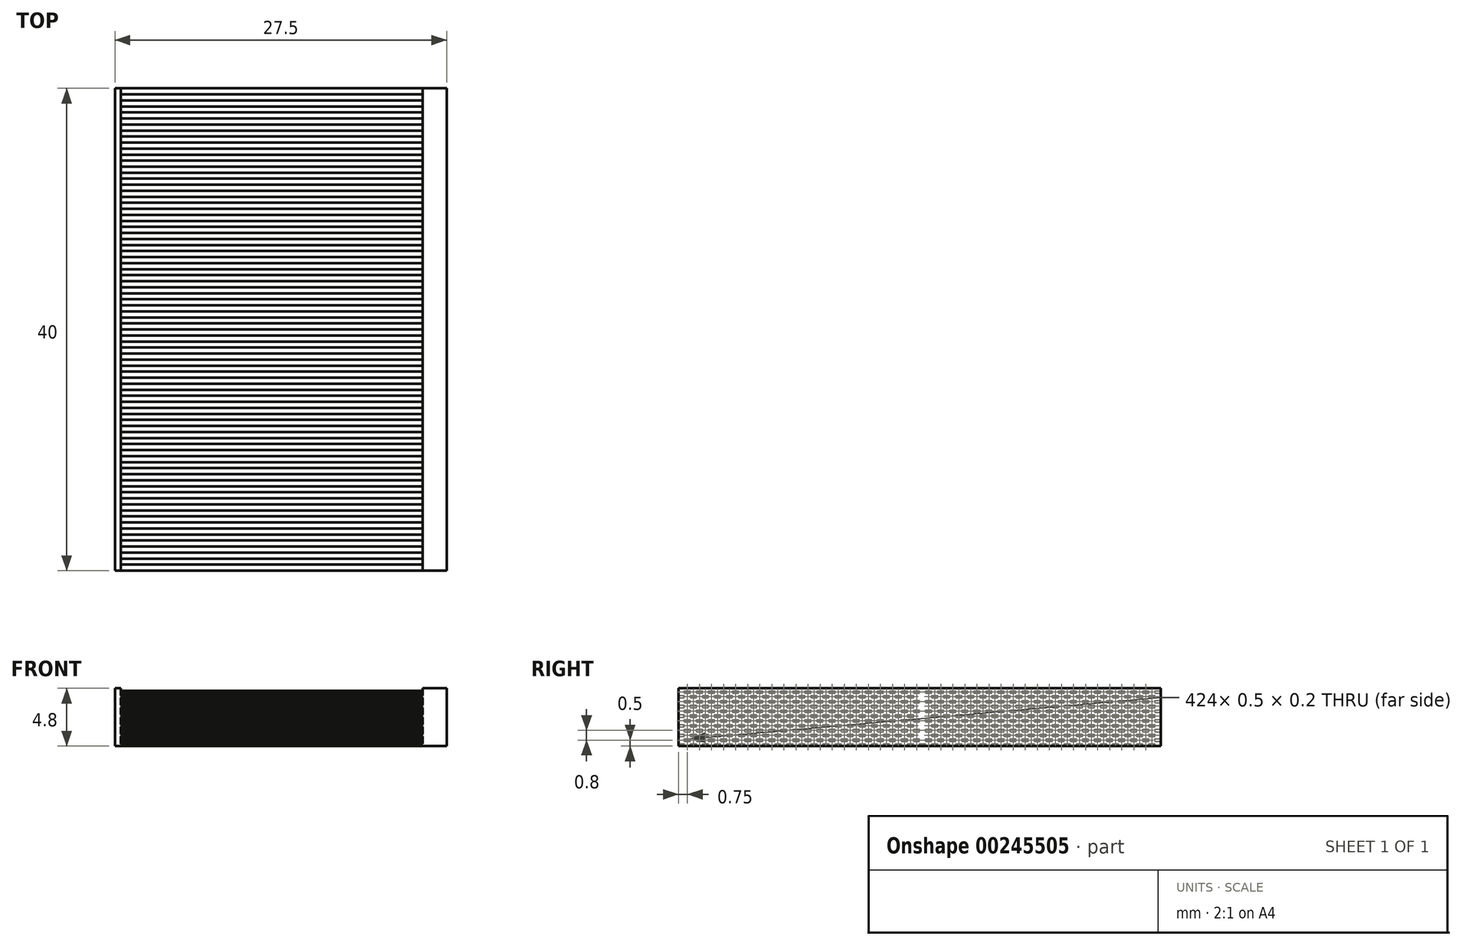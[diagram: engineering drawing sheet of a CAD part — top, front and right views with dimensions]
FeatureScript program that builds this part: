
annotation { "Feature Type Name" : "Feature", "Feature Type Description" : "" }
export const myFeature = defineFeature(function(context is Context, id is Id, definition is map)
    precondition{}
    {
        {
            var Q0;
            Q0=qCreatedBy(makeId("Right.planeOp"),FACE);
            var sketch = newSketch(context, id + "F0", { "sketchPlane" : qUnion([Q0])});
            skLineSegment(sketch, "E0.bottom", {"start": v(-20, 0) * mm, "end": v(20, 0) * mm});
            skLineSegment(sketch, "E0.top", {"start": v(-20, 4.8) * mm, "end": v(20, 4.8) * mm});
            skLineSegment(sketch, "E0.left", {"start": v(-20, 0) * mm, "end": v(-20, 4.8) * mm});
            skLineSegment(sketch, "E0.right", {"start": v(20, 0) * mm, "end": v(20, 4.8) * mm});
            skPoint(sketch, "E0.middle", {"position": v(0, 2.4) * mm});
            skSolve(sketch);
        }
        {
            var Q0;
            Q0 = qSketchRegion(id + "F0", true);
            extrude(context, id + "F1", {"entities" : qUnion([Q0]), "depth" : 0.5 * mm});
        }
        {
            var Q0;
            Q0=makeQuery(id+"F1.opExtrude","CAP_FACE",FACE,{"disambiguationData":[OSD([sQuery(id+"F0.wireOp",EDGE,"E0.bottom"),sQuery(id+"F0.wireOp",EDGE,"E0.top"),sQuery(id+"F0.wireOp",EDGE,"E0.left"),sQuery(id+"F0.wireOp",EDGE,"E0.right")])],"isStart":false});
            var sketch = newSketch(context, id + "F2", { "sketchPlane" : qUnion([Q0])});
            skLineSegment(sketch, "E1.bottom", {"start": v(-20, 0) * mm, "end": v(-19.5, 0) * mm});
            skLineSegment(sketch, "E1.top", {"start": v(-20, 0.2) * mm, "end": v(-19.5, 0.2) * mm});
            skLineSegment(sketch, "E1.left", {"start": v(-20, 0) * mm, "end": v(-20, 0.2) * mm});
            skLineSegment(sketch, "E1.right", {"start": v(-19.5, 0) * mm, "end": v(-19.5, 0.2) * mm});
            skLineSegment(sketch, "E2.1.0.0", {"start": v(-19, 0) * mm, "end": v(-19, 0.2) * mm});
            skLineSegment(sketch, "E2.1.0.1", {"start": v(-18.5, 0) * mm, "end": v(-18.5, 0.2) * mm});
            skLineSegment(sketch, "E2.1.0.2", {"start": v(-19, 0.2) * mm, "end": v(-18.5, 0.2) * mm});
            skLineSegment(sketch, "E2.1.0.3", {"start": v(-19, 0) * mm, "end": v(-18.5, 0) * mm});
            skLineSegment(sketch, "E2.2.0.0", {"start": v(-18, 0) * mm, "end": v(-18, 0.2) * mm});
            skLineSegment(sketch, "E2.2.0.1", {"start": v(-17.5, 0) * mm, "end": v(-17.5, 0.2) * mm});
            skLineSegment(sketch, "E2.2.0.2", {"start": v(-18, 0.2) * mm, "end": v(-17.5, 0.2) * mm});
            skLineSegment(sketch, "E2.2.0.3", {"start": v(-18, 0) * mm, "end": v(-17.5, 0) * mm});
            skLineSegment(sketch, "E2.3.0.0", {"start": v(-17, 0) * mm, "end": v(-17, 0.2) * mm});
            skLineSegment(sketch, "E2.3.0.1", {"start": v(-16.5, 0) * mm, "end": v(-16.5, 0.2) * mm});
            skLineSegment(sketch, "E2.3.0.2", {"start": v(-17, 0.2) * mm, "end": v(-16.5, 0.2) * mm});
            skLineSegment(sketch, "E2.3.0.3", {"start": v(-17, 0) * mm, "end": v(-16.5, 0) * mm});
            skLineSegment(sketch, "E2.4.0.0", {"start": v(-16, 0) * mm, "end": v(-16, 0.2) * mm});
            skLineSegment(sketch, "E2.4.0.1", {"start": v(-15.5, 0) * mm, "end": v(-15.5, 0.2) * mm});
            skLineSegment(sketch, "E2.4.0.2", {"start": v(-16, 0.2) * mm, "end": v(-15.5, 0.2) * mm});
            skLineSegment(sketch, "E2.4.0.3", {"start": v(-16, 0) * mm, "end": v(-15.5, 0) * mm});
            skLineSegment(sketch, "E2.5.0.0", {"start": v(-15, 0) * mm, "end": v(-15, 0.2) * mm});
            skLineSegment(sketch, "E2.5.0.1", {"start": v(-14.5, 0) * mm, "end": v(-14.5, 0.2) * mm});
            skLineSegment(sketch, "E2.5.0.2", {"start": v(-15, 0.2) * mm, "end": v(-14.5, 0.2) * mm});
            skLineSegment(sketch, "E2.5.0.3", {"start": v(-15, 0) * mm, "end": v(-14.5, 0) * mm});
            skLineSegment(sketch, "E2.6.0.0", {"start": v(-14, 0) * mm, "end": v(-14, 0.2) * mm});
            skLineSegment(sketch, "E2.6.0.1", {"start": v(-13.5, 0) * mm, "end": v(-13.5, 0.2) * mm});
            skLineSegment(sketch, "E2.6.0.2", {"start": v(-14, 0.2) * mm, "end": v(-13.5, 0.2) * mm});
            skLineSegment(sketch, "E2.6.0.3", {"start": v(-14, 0) * mm, "end": v(-13.5, 0) * mm});
            skLineSegment(sketch, "E2.7.0.0", {"start": v(-13, 0) * mm, "end": v(-13, 0.2) * mm});
            skLineSegment(sketch, "E2.7.0.1", {"start": v(-12.5, 0) * mm, "end": v(-12.5, 0.2) * mm});
            skLineSegment(sketch, "E2.7.0.2", {"start": v(-13, 0.2) * mm, "end": v(-12.5, 0.2) * mm});
            skLineSegment(sketch, "E2.7.0.3", {"start": v(-13, 0) * mm, "end": v(-12.5, 0) * mm});
            skLineSegment(sketch, "E2.8.0.0", {"start": v(-12, 0) * mm, "end": v(-12, 0.2) * mm});
            skLineSegment(sketch, "E2.8.0.1", {"start": v(-11.5, 0) * mm, "end": v(-11.5, 0.2) * mm});
            skLineSegment(sketch, "E2.8.0.2", {"start": v(-12, 0.2) * mm, "end": v(-11.5, 0.2) * mm});
            skLineSegment(sketch, "E2.8.0.3", {"start": v(-12, 0) * mm, "end": v(-11.5, 0) * mm});
            skLineSegment(sketch, "E2.9.0.0", {"start": v(-11, 0) * mm, "end": v(-11, 0.2) * mm});
            skLineSegment(sketch, "E2.9.0.1", {"start": v(-10.5, 0) * mm, "end": v(-10.5, 0.2) * mm});
            skLineSegment(sketch, "E2.9.0.2", {"start": v(-11, 0.2) * mm, "end": v(-10.5, 0.2) * mm});
            skLineSegment(sketch, "E2.9.0.3", {"start": v(-11, 0) * mm, "end": v(-10.5, 0) * mm});
            skLineSegment(sketch, "E2.10.0.0", {"start": v(-10, 0) * mm, "end": v(-10, 0.2) * mm});
            skLineSegment(sketch, "E2.10.0.1", {"start": v(-9.5, 0) * mm, "end": v(-9.5, 0.2) * mm});
            skLineSegment(sketch, "E2.10.0.2", {"start": v(-10, 0.2) * mm, "end": v(-9.5, 0.2) * mm});
            skLineSegment(sketch, "E2.10.0.3", {"start": v(-10, 0) * mm, "end": v(-9.5, 0) * mm});
            skLineSegment(sketch, "E2.11.0.0", {"start": v(-9, 0) * mm, "end": v(-9, 0.2) * mm});
            skLineSegment(sketch, "E2.11.0.1", {"start": v(-8.5, 0) * mm, "end": v(-8.5, 0.2) * mm});
            skLineSegment(sketch, "E2.11.0.2", {"start": v(-9, 0.2) * mm, "end": v(-8.5, 0.2) * mm});
            skLineSegment(sketch, "E2.11.0.3", {"start": v(-9, 0) * mm, "end": v(-8.5, 0) * mm});
            skLineSegment(sketch, "E2.12.0.0", {"start": v(-8, 0) * mm, "end": v(-8, 0.2) * mm});
            skLineSegment(sketch, "E2.12.0.1", {"start": v(-7.5, 0) * mm, "end": v(-7.5, 0.2) * mm});
            skLineSegment(sketch, "E2.12.0.2", {"start": v(-8, 0.2) * mm, "end": v(-7.5, 0.2) * mm});
            skLineSegment(sketch, "E2.12.0.3", {"start": v(-8, 0) * mm, "end": v(-7.5, 0) * mm});
            skLineSegment(sketch, "E2.13.0.0", {"start": v(-7, 0) * mm, "end": v(-7, 0.2) * mm});
            skLineSegment(sketch, "E2.13.0.1", {"start": v(-6.5, 0) * mm, "end": v(-6.5, 0.2) * mm});
            skLineSegment(sketch, "E2.13.0.2", {"start": v(-7, 0.2) * mm, "end": v(-6.5, 0.2) * mm});
            skLineSegment(sketch, "E2.13.0.3", {"start": v(-7, 0) * mm, "end": v(-6.5, 0) * mm});
            skLineSegment(sketch, "E2.14.0.0", {"start": v(-6, 0) * mm, "end": v(-6, 0.2) * mm});
            skLineSegment(sketch, "E2.14.0.1", {"start": v(-5.5, 0) * mm, "end": v(-5.5, 0.2) * mm});
            skLineSegment(sketch, "E2.14.0.2", {"start": v(-6, 0.2) * mm, "end": v(-5.5, 0.2) * mm});
            skLineSegment(sketch, "E2.14.0.3", {"start": v(-6, 0) * mm, "end": v(-5.5, 0) * mm});
            skLineSegment(sketch, "E2.15.0.0", {"start": v(-5, 0) * mm, "end": v(-5, 0.2) * mm});
            skLineSegment(sketch, "E2.15.0.1", {"start": v(-4.5, 0) * mm, "end": v(-4.5, 0.2) * mm});
            skLineSegment(sketch, "E2.15.0.2", {"start": v(-5, 0.2) * mm, "end": v(-4.5, 0.2) * mm});
            skLineSegment(sketch, "E2.15.0.3", {"start": v(-5, 0) * mm, "end": v(-4.5, 0) * mm});
            skLineSegment(sketch, "E2.16.0.0", {"start": v(-4, 0) * mm, "end": v(-4, 0.2) * mm});
            skLineSegment(sketch, "E2.16.0.1", {"start": v(-3.5, 0) * mm, "end": v(-3.5, 0.2) * mm});
            skLineSegment(sketch, "E2.16.0.2", {"start": v(-4, 0.2) * mm, "end": v(-3.5, 0.2) * mm});
            skLineSegment(sketch, "E2.16.0.3", {"start": v(-4, 0) * mm, "end": v(-3.5, 0) * mm});
            skLineSegment(sketch, "E2.17.0.0", {"start": v(-3, 0) * mm, "end": v(-3, 0.2) * mm});
            skLineSegment(sketch, "E2.17.0.1", {"start": v(-2.5, 0) * mm, "end": v(-2.5, 0.2) * mm});
            skLineSegment(sketch, "E2.17.0.2", {"start": v(-3, 0.2) * mm, "end": v(-2.5, 0.2) * mm});
            skLineSegment(sketch, "E2.17.0.3", {"start": v(-3, 0) * mm, "end": v(-2.5, 0) * mm});
            skLineSegment(sketch, "E2.18.0.0", {"start": v(-2, 0) * mm, "end": v(-2, 0.2) * mm});
            skLineSegment(sketch, "E2.18.0.1", {"start": v(-1.5, 0) * mm, "end": v(-1.5, 0.2) * mm});
            skLineSegment(sketch, "E2.18.0.2", {"start": v(-2, 0.2) * mm, "end": v(-1.5, 0.2) * mm});
            skLineSegment(sketch, "E2.18.0.3", {"start": v(-2, 0) * mm, "end": v(-1.5, 0) * mm});
            skLineSegment(sketch, "E2.19.0.0", {"start": v(-1, 0) * mm, "end": v(-1, 0.2) * mm});
            skLineSegment(sketch, "E2.19.0.1", {"start": v(-0.5, 0) * mm, "end": v(-0.5, 0.2) * mm});
            skLineSegment(sketch, "E2.19.0.2", {"start": v(-1, 0.2) * mm, "end": v(-0.5, 0.2) * mm});
            skLineSegment(sketch, "E2.19.0.3", {"start": v(-1, 0) * mm, "end": v(-0.5, 0) * mm});
            skLineSegment(sketch, "E2.direction1", {"start": v(-20, 0) * mm, "end": v(-19, 0) * mm, "construction": true});
            skLineSegment(sketch, "E3.bottom", {"start": v(-19.5, 0.4) * mm, "end": v(-19, 0.4) * mm});
            skLineSegment(sketch, "E3.top", {"start": v(-19.5, 0.6) * mm, "end": v(-19, 0.6) * mm});
            skLineSegment(sketch, "E3.left", {"start": v(-19.5, 0.4) * mm, "end": v(-19.5, 0.6) * mm});
            skLineSegment(sketch, "E3.right", {"start": v(-19, 0.4) * mm, "end": v(-19, 0.6) * mm});
            skLineSegment(sketch, "E4.1.0.0", {"start": v(-18, 0.4) * mm, "end": v(-18, 0.6) * mm});
            skLineSegment(sketch, "E4.1.0.1", {"start": v(-18.5, 0.4) * mm, "end": v(-18, 0.4) * mm});
            skLineSegment(sketch, "E4.1.0.2", {"start": v(-18.5, 0.6) * mm, "end": v(-18, 0.6) * mm});
            skLineSegment(sketch, "E4.1.0.3", {"start": v(-18.5, 0.4) * mm, "end": v(-18.5, 0.6) * mm});
            skLineSegment(sketch, "E4.2.0.0", {"start": v(-17, 0.4) * mm, "end": v(-17, 0.6) * mm});
            skLineSegment(sketch, "E4.2.0.1", {"start": v(-17.5, 0.4) * mm, "end": v(-17, 0.4) * mm});
            skLineSegment(sketch, "E4.2.0.2", {"start": v(-17.5, 0.6) * mm, "end": v(-17, 0.6) * mm});
            skLineSegment(sketch, "E4.2.0.3", {"start": v(-17.5, 0.4) * mm, "end": v(-17.5, 0.6) * mm});
            skLineSegment(sketch, "E4.3.0.0", {"start": v(-16, 0.4) * mm, "end": v(-16, 0.6) * mm});
            skLineSegment(sketch, "E4.3.0.1", {"start": v(-16.5, 0.4) * mm, "end": v(-16, 0.4) * mm});
            skLineSegment(sketch, "E4.3.0.2", {"start": v(-16.5, 0.6) * mm, "end": v(-16, 0.6) * mm});
            skLineSegment(sketch, "E4.3.0.3", {"start": v(-16.5, 0.4) * mm, "end": v(-16.5, 0.6) * mm});
            skLineSegment(sketch, "E4.4.0.0", {"start": v(-15, 0.4) * mm, "end": v(-15, 0.6) * mm});
            skLineSegment(sketch, "E4.4.0.1", {"start": v(-15.5, 0.4) * mm, "end": v(-15, 0.4) * mm});
            skLineSegment(sketch, "E4.4.0.2", {"start": v(-15.5, 0.6) * mm, "end": v(-15, 0.6) * mm});
            skLineSegment(sketch, "E4.4.0.3", {"start": v(-15.5, 0.4) * mm, "end": v(-15.5, 0.6) * mm});
            skLineSegment(sketch, "E4.5.0.0", {"start": v(-14, 0.4) * mm, "end": v(-14, 0.6) * mm});
            skLineSegment(sketch, "E4.5.0.1", {"start": v(-14.5, 0.4) * mm, "end": v(-14, 0.4) * mm});
            skLineSegment(sketch, "E4.5.0.2", {"start": v(-14.5, 0.6) * mm, "end": v(-14, 0.6) * mm});
            skLineSegment(sketch, "E4.5.0.3", {"start": v(-14.5, 0.4) * mm, "end": v(-14.5, 0.6) * mm});
            skLineSegment(sketch, "E4.6.0.0", {"start": v(-13, 0.4) * mm, "end": v(-13, 0.6) * mm});
            skLineSegment(sketch, "E4.6.0.1", {"start": v(-13.5, 0.4) * mm, "end": v(-13, 0.4) * mm});
            skLineSegment(sketch, "E4.6.0.2", {"start": v(-13.5, 0.6) * mm, "end": v(-13, 0.6) * mm});
            skLineSegment(sketch, "E4.6.0.3", {"start": v(-13.5, 0.4) * mm, "end": v(-13.5, 0.6) * mm});
            skLineSegment(sketch, "E4.7.0.0", {"start": v(-12, 0.4) * mm, "end": v(-12, 0.6) * mm});
            skLineSegment(sketch, "E4.7.0.1", {"start": v(-12.5, 0.4) * mm, "end": v(-12, 0.4) * mm});
            skLineSegment(sketch, "E4.7.0.2", {"start": v(-12.5, 0.6) * mm, "end": v(-12, 0.6) * mm});
            skLineSegment(sketch, "E4.7.0.3", {"start": v(-12.5, 0.4) * mm, "end": v(-12.5, 0.6) * mm});
            skLineSegment(sketch, "E4.8.0.0", {"start": v(-11, 0.4) * mm, "end": v(-11, 0.6) * mm});
            skLineSegment(sketch, "E4.8.0.1", {"start": v(-11.5, 0.4) * mm, "end": v(-11, 0.4) * mm});
            skLineSegment(sketch, "E4.8.0.2", {"start": v(-11.5, 0.6) * mm, "end": v(-11, 0.6) * mm});
            skLineSegment(sketch, "E4.8.0.3", {"start": v(-11.5, 0.4) * mm, "end": v(-11.5, 0.6) * mm});
            skLineSegment(sketch, "E4.9.0.0", {"start": v(-10, 0.4) * mm, "end": v(-10, 0.6) * mm});
            skLineSegment(sketch, "E4.9.0.1", {"start": v(-10.5, 0.4) * mm, "end": v(-10, 0.4) * mm});
            skLineSegment(sketch, "E4.9.0.2", {"start": v(-10.5, 0.6) * mm, "end": v(-10, 0.6) * mm});
            skLineSegment(sketch, "E4.9.0.3", {"start": v(-10.5, 0.4) * mm, "end": v(-10.5, 0.6) * mm});
            skLineSegment(sketch, "E4.10.0.0", {"start": v(-9, 0.4) * mm, "end": v(-9, 0.6) * mm});
            skLineSegment(sketch, "E4.10.0.1", {"start": v(-9.5, 0.4) * mm, "end": v(-9, 0.4) * mm});
            skLineSegment(sketch, "E4.10.0.2", {"start": v(-9.5, 0.6) * mm, "end": v(-9, 0.6) * mm});
            skLineSegment(sketch, "E4.10.0.3", {"start": v(-9.5, 0.4) * mm, "end": v(-9.5, 0.6) * mm});
            skLineSegment(sketch, "E4.11.0.0", {"start": v(-8, 0.4) * mm, "end": v(-8, 0.6) * mm});
            skLineSegment(sketch, "E4.11.0.1", {"start": v(-8.5, 0.4) * mm, "end": v(-8, 0.4) * mm});
            skLineSegment(sketch, "E4.11.0.2", {"start": v(-8.5, 0.6) * mm, "end": v(-8, 0.6) * mm});
            skLineSegment(sketch, "E4.11.0.3", {"start": v(-8.5, 0.4) * mm, "end": v(-8.5, 0.6) * mm});
            skLineSegment(sketch, "E4.12.0.0", {"start": v(-7, 0.4) * mm, "end": v(-7, 0.6) * mm});
            skLineSegment(sketch, "E4.12.0.1", {"start": v(-7.5, 0.4) * mm, "end": v(-7, 0.4) * mm});
            skLineSegment(sketch, "E4.12.0.2", {"start": v(-7.5, 0.6) * mm, "end": v(-7, 0.6) * mm});
            skLineSegment(sketch, "E4.12.0.3", {"start": v(-7.5, 0.4) * mm, "end": v(-7.5, 0.6) * mm});
            skLineSegment(sketch, "E4.13.0.0", {"start": v(-6, 0.4) * mm, "end": v(-6, 0.6) * mm});
            skLineSegment(sketch, "E4.13.0.1", {"start": v(-6.5, 0.4) * mm, "end": v(-6, 0.4) * mm});
            skLineSegment(sketch, "E4.13.0.2", {"start": v(-6.5, 0.6) * mm, "end": v(-6, 0.6) * mm});
            skLineSegment(sketch, "E4.13.0.3", {"start": v(-6.5, 0.4) * mm, "end": v(-6.5, 0.6) * mm});
            skLineSegment(sketch, "E4.14.0.0", {"start": v(-5, 0.4) * mm, "end": v(-5, 0.6) * mm});
            skLineSegment(sketch, "E4.14.0.1", {"start": v(-5.5, 0.4) * mm, "end": v(-5, 0.4) * mm});
            skLineSegment(sketch, "E4.14.0.2", {"start": v(-5.5, 0.6) * mm, "end": v(-5, 0.6) * mm});
            skLineSegment(sketch, "E4.14.0.3", {"start": v(-5.5, 0.4) * mm, "end": v(-5.5, 0.6) * mm});
            skLineSegment(sketch, "E4.15.0.0", {"start": v(-4, 0.4) * mm, "end": v(-4, 0.6) * mm});
            skLineSegment(sketch, "E4.15.0.1", {"start": v(-4.5, 0.4) * mm, "end": v(-4, 0.4) * mm});
            skLineSegment(sketch, "E4.15.0.2", {"start": v(-4.5, 0.6) * mm, "end": v(-4, 0.6) * mm});
            skLineSegment(sketch, "E4.15.0.3", {"start": v(-4.5, 0.4) * mm, "end": v(-4.5, 0.6) * mm});
            skLineSegment(sketch, "E4.16.0.0", {"start": v(-3, 0.4) * mm, "end": v(-3, 0.6) * mm});
            skLineSegment(sketch, "E4.16.0.1", {"start": v(-3.5, 0.4) * mm, "end": v(-3, 0.4) * mm});
            skLineSegment(sketch, "E4.16.0.2", {"start": v(-3.5, 0.6) * mm, "end": v(-3, 0.6) * mm});
            skLineSegment(sketch, "E4.16.0.3", {"start": v(-3.5, 0.4) * mm, "end": v(-3.5, 0.6) * mm});
            skLineSegment(sketch, "E4.17.0.0", {"start": v(-2, 0.4) * mm, "end": v(-2, 0.6) * mm});
            skLineSegment(sketch, "E4.17.0.1", {"start": v(-2.5, 0.4) * mm, "end": v(-2, 0.4) * mm});
            skLineSegment(sketch, "E4.17.0.2", {"start": v(-2.5, 0.6) * mm, "end": v(-2, 0.6) * mm});
            skLineSegment(sketch, "E4.17.0.3", {"start": v(-2.5, 0.4) * mm, "end": v(-2.5, 0.6) * mm});
            skLineSegment(sketch, "E4.18.0.0", {"start": v(-1, 0.4) * mm, "end": v(-1, 0.6) * mm});
            skLineSegment(sketch, "E4.18.0.1", {"start": v(-1.5, 0.4) * mm, "end": v(-1, 0.4) * mm});
            skLineSegment(sketch, "E4.18.0.2", {"start": v(-1.5, 0.6) * mm, "end": v(-1, 0.6) * mm});
            skLineSegment(sketch, "E4.18.0.3", {"start": v(-1.5, 0.4) * mm, "end": v(-1.5, 0.6) * mm});
            skLineSegment(sketch, "E4.19.0.0", {"start": v(0, 0.4) * mm, "end": v(0, 0.6) * mm});
            skLineSegment(sketch, "E4.19.0.1", {"start": v(-0.5, 0.4) * mm, "end": v(0, 0.4) * mm});
            skLineSegment(sketch, "E4.19.0.2", {"start": v(-0.5, 0.6) * mm, "end": v(0, 0.6) * mm});
            skLineSegment(sketch, "E4.19.0.3", {"start": v(-0.5, 0.4) * mm, "end": v(-0.5, 0.6) * mm});
            skLineSegment(sketch, "E4.direction1", {"start": v(-19.5, 0.4) * mm, "end": v(-18.5, 0.4) * mm, "construction": true});
            skLineSegment(sketch, "E5.0.1.0", {"start": v(-5, 1) * mm, "end": v(-4.5, 1) * mm});
            skLineSegment(sketch, "E5.0.1.1", {"start": v(-13.5, 1.4) * mm, "end": v(-13, 1.4) * mm});
            skLineSegment(sketch, "E5.0.1.2", {"start": v(-17, 0.8) * mm, "end": v(-16.5, 0.8) * mm});
            skLineSegment(sketch, "E5.0.1.3", {"start": v(-19.5, 1.4) * mm, "end": v(-19, 1.4) * mm});
            skLineSegment(sketch, "E5.0.1.4", {"start": v(-16.5, 1.4) * mm, "end": v(-16, 1.4) * mm});
            skLineSegment(sketch, "E5.0.1.5", {"start": v(-14.5, 1.4) * mm, "end": v(-14, 1.4) * mm});
            skLineSegment(sketch, "E5.0.1.6", {"start": v(-19, 0.8) * mm, "end": v(-18.5, 0.8) * mm});
            skLineSegment(sketch, "E5.0.1.7", {"start": v(-15, 0.8) * mm, "end": v(-14.5, 0.8) * mm});
            skLineSegment(sketch, "E5.0.1.8", {"start": v(-4.5, 1.4) * mm, "end": v(-4, 1.4) * mm});
            skLineSegment(sketch, "E5.0.1.9", {"start": v(-7.5, 1.4) * mm, "end": v(-7, 1.4) * mm});
            skLineSegment(sketch, "E5.0.1.10", {"start": v(-12.5, 1.4) * mm, "end": v(-12, 1.4) * mm});
            skLineSegment(sketch, "E5.0.1.11", {"start": v(-0.5, 1.2) * mm, "end": v(0, 1.2) * mm});
            skLineSegment(sketch, "E5.0.1.12", {"start": v(-1.5, 1.4) * mm, "end": v(-1, 1.4) * mm});
            skLineSegment(sketch, "E5.0.1.13", {"start": v(-16, 0.8) * mm, "end": v(-15.5, 0.8) * mm});
            skLineSegment(sketch, "E5.0.1.14", {"start": v(-12, 0.8) * mm, "end": v(-11.5, 0.8) * mm});
            skLineSegment(sketch, "E5.0.1.15", {"start": v(-18.5, 1.4) * mm, "end": v(-18, 1.4) * mm});
            skLineSegment(sketch, "E5.0.1.16", {"start": v(-18.5, 1.2) * mm, "end": v(-18, 1.2) * mm});
            skLineSegment(sketch, "E5.0.1.17", {"start": v(-0.5, 1.4) * mm, "end": v(0, 1.4) * mm});
            skLineSegment(sketch, "E5.0.1.18", {"start": v(-13, 0.8) * mm, "end": v(-13, 1) * mm});
            skLineSegment(sketch, "E5.0.1.19", {"start": v(-10, 1.2) * mm, "end": v(-10, 1.4) * mm});
            skLineSegment(sketch, "E5.0.1.20", {"start": v(-1, 1) * mm, "end": v(-0.5, 1) * mm});
            skLineSegment(sketch, "E5.0.1.21", {"start": v(-11, 0.8) * mm, "end": v(-11, 1) * mm});
            skLineSegment(sketch, "E5.0.1.22", {"start": v(-18.5, 0.8) * mm, "end": v(-18.5, 1) * mm});
            skLineSegment(sketch, "E5.0.1.23", {"start": v(-7, 1) * mm, "end": v(-6.5, 1) * mm});
            skLineSegment(sketch, "E5.0.1.24", {"start": v(-17.5, 1.4) * mm, "end": v(-17, 1.4) * mm});
            skLineSegment(sketch, "E5.0.1.25", {"start": v(-13, 1) * mm, "end": v(-12.5, 1) * mm});
            skLineSegment(sketch, "E5.0.1.26", {"start": v(-20, 1) * mm, "end": v(-19.5, 1) * mm});
            skLineSegment(sketch, "E5.0.1.27", {"start": v(-16.5, 1.2) * mm, "end": v(-16, 1.2) * mm});
            skLineSegment(sketch, "E5.0.1.28", {"start": v(-8.5, 1.4) * mm, "end": v(-8, 1.4) * mm});
            skLineSegment(sketch, "E5.0.1.29", {"start": v(-15, 0.8) * mm, "end": v(-15, 1) * mm});
            skLineSegment(sketch, "E5.0.1.30", {"start": v(-8.5, 1.2) * mm, "end": v(-8, 1.2) * mm});
            skLineSegment(sketch, "E5.0.1.31", {"start": v(-9.5, 1.4) * mm, "end": v(-9, 1.4) * mm});
            skLineSegment(sketch, "E5.0.1.32", {"start": v(-6.5, 1.2) * mm, "end": v(-6, 1.2) * mm});
            skLineSegment(sketch, "E5.0.1.33", {"start": v(-8, 1.2) * mm, "end": v(-8, 1.4) * mm});
            skLineSegment(sketch, "E5.0.1.34", {"start": v(-16, 1.2) * mm, "end": v(-16, 1.4) * mm});
            skLineSegment(sketch, "E5.0.1.35", {"start": v(-11.5, 1.4) * mm, "end": v(-11, 1.4) * mm});
            skLineSegment(sketch, "E5.0.1.36", {"start": v(-12.5, 1.2) * mm, "end": v(-12, 1.2) * mm});
            skLineSegment(sketch, "E5.0.1.37", {"start": v(-10, 0.8) * mm, "end": v(-9.5, 0.8) * mm});
            skLineSegment(sketch, "E5.0.1.38", {"start": v(-8, 0.8) * mm, "end": v(-7.5, 0.8) * mm});
            skLineSegment(sketch, "E5.0.1.39", {"start": v(-6, 0.8) * mm, "end": v(-5.5, 0.8) * mm});
            skLineSegment(sketch, "E5.0.1.40", {"start": v(-2, 0.8) * mm, "end": v(-1.5, 0.8) * mm});
            skLineSegment(sketch, "E5.0.1.41", {"start": v(-3.5, 1.4) * mm, "end": v(-3, 1.4) * mm});
            skLineSegment(sketch, "E5.0.1.42", {"start": v(-1, 0.8) * mm, "end": v(-1, 1) * mm});
            skLineSegment(sketch, "E5.0.1.43", {"start": v(-4, 0.8) * mm, "end": v(-3.5, 0.8) * mm});
            skLineSegment(sketch, "E5.0.1.44", {"start": v(-5, 0.8) * mm, "end": v(-5, 1) * mm});
            skLineSegment(sketch, "E5.0.1.45", {"start": v(-9, 0.8) * mm, "end": v(-9, 1) * mm});
            skLineSegment(sketch, "E5.0.1.46", {"start": v(-15.5, 1.4) * mm, "end": v(-15, 1.4) * mm});
            skLineSegment(sketch, "E5.0.1.47", {"start": v(-20, 0.8) * mm, "end": v(-20, 1) * mm});
            skLineSegment(sketch, "E5.0.1.48", {"start": v(-18, 0.8) * mm, "end": v(-17.5, 0.8) * mm});
            skLineSegment(sketch, "E5.0.1.49", {"start": v(-17, 0.8) * mm, "end": v(-17, 1) * mm});
            skLineSegment(sketch, "E5.0.1.50", {"start": v(-19, 1) * mm, "end": v(-18.5, 1) * mm});
            skLineSegment(sketch, "E5.0.1.51", {"start": v(-7, 0.8) * mm, "end": v(-7, 1) * mm});
            skLineSegment(sketch, "E5.0.1.52", {"start": v(-19.5, 0.8) * mm, "end": v(-19.5, 1) * mm});
            skLineSegment(sketch, "E5.0.1.53", {"start": v(-6, 1.2) * mm, "end": v(-6, 1.4) * mm});
            skLineSegment(sketch, "E5.0.1.54", {"start": v(-14, 1.2) * mm, "end": v(-14, 1.4) * mm});
            skLineSegment(sketch, "E5.0.1.55", {"start": v(-18, 1.2) * mm, "end": v(-18, 1.4) * mm});
            skLineSegment(sketch, "E5.0.1.56", {"start": v(-1, 0.8) * mm, "end": v(-0.5, 0.8) * mm});
            skLineSegment(sketch, "E5.0.1.57", {"start": v(-9, 0.8) * mm, "end": v(-8.5, 0.8) * mm});
            skLineSegment(sketch, "E5.0.1.58", {"start": v(-11, 1) * mm, "end": v(-10.5, 1) * mm});
            skLineSegment(sketch, "E5.0.1.59", {"start": v(-2.5, 1.4) * mm, "end": v(-2, 1.4) * mm});
            skLineSegment(sketch, "E5.0.1.60", {"start": v(-9, 1) * mm, "end": v(-8.5, 1) * mm});
            skLineSegment(sketch, "E5.0.1.61", {"start": v(-11, 0.8) * mm, "end": v(-10.5, 0.8) * mm});
            skLineSegment(sketch, "E5.0.1.62", {"start": v(-3, 0.8) * mm, "end": v(-3, 1) * mm});
            skLineSegment(sketch, "E5.0.1.63", {"start": v(0, 1.2) * mm, "end": v(0, 1.4) * mm});
            skLineSegment(sketch, "E5.0.1.64", {"start": v(-10.5, 1.4) * mm, "end": v(-10, 1.4) * mm});
            skLineSegment(sketch, "E5.0.1.65", {"start": v(-14.5, 1.2) * mm, "end": v(-14, 1.2) * mm});
            skLineSegment(sketch, "E5.0.1.66", {"start": v(-10.5, 1.2) * mm, "end": v(-10, 1.2) * mm});
            skLineSegment(sketch, "E5.0.1.67", {"start": v(-5, 0.8) * mm, "end": v(-4.5, 0.8) * mm});
            skLineSegment(sketch, "E5.0.1.68", {"start": v(-3, 1) * mm, "end": v(-2.5, 1) * mm});
            skLineSegment(sketch, "E5.0.1.69", {"start": v(-14, 0.8) * mm, "end": v(-13.5, 0.8) * mm});
            skLineSegment(sketch, "E5.0.1.70", {"start": v(-6.5, 1.4) * mm, "end": v(-6, 1.4) * mm});
            skLineSegment(sketch, "E5.0.1.71", {"start": v(-13, 0.8) * mm, "end": v(-12.5, 0.8) * mm});
            skLineSegment(sketch, "E5.0.1.72", {"start": v(-15, 1) * mm, "end": v(-14.5, 1) * mm});
            skLineSegment(sketch, "E5.0.1.73", {"start": v(-12, 1.2) * mm, "end": v(-12, 1.4) * mm});
            skLineSegment(sketch, "E5.0.1.74", {"start": v(-7, 0.8) * mm, "end": v(-6.5, 0.8) * mm});
            skLineSegment(sketch, "E5.0.1.75", {"start": v(-5.5, 1.4) * mm, "end": v(-5, 1.4) * mm});
            skLineSegment(sketch, "E5.0.1.76", {"start": v(-3, 0.8) * mm, "end": v(-2.5, 0.8) * mm});
            skLineSegment(sketch, "E5.0.1.77", {"start": v(-3.5, 1.2) * mm, "end": v(-3.5, 1.4) * mm});
            skLineSegment(sketch, "E5.0.1.78", {"start": v(-5, 1.2) * mm, "end": v(-5, 1.4) * mm});
            skLineSegment(sketch, "E5.0.1.79", {"start": v(-6, 1) * mm, "end": v(-5.5, 1) * mm});
            skLineSegment(sketch, "E5.0.1.80", {"start": v(-6.5, 1.2) * mm, "end": v(-6.5, 1.4) * mm});
            skLineSegment(sketch, "E5.0.1.81", {"start": v(-2, 1.2) * mm, "end": v(-2, 1.4) * mm});
            skLineSegment(sketch, "E5.0.1.82", {"start": v(-15, 1.2) * mm, "end": v(-15, 1.4) * mm});
            skLineSegment(sketch, "E5.0.1.83", {"start": v(-7.5, 0.8) * mm, "end": v(-7.5, 1) * mm});
            skLineSegment(sketch, "E5.0.1.84", {"start": v(-10.5, 1.2) * mm, "end": v(-10.5, 1.4) * mm});
            skLineSegment(sketch, "E5.0.1.85", {"start": v(-11.5, 1.2) * mm, "end": v(-11, 1.2) * mm});
            skLineSegment(sketch, "E5.0.1.86", {"start": v(-1.5, 1.2) * mm, "end": v(-1, 1.2) * mm});
            skLineSegment(sketch, "E5.0.1.87", {"start": v(-17.5, 0.8) * mm, "end": v(-17.5, 1) * mm});
            skLineSegment(sketch, "E5.0.1.88", {"start": v(-7.5, 1.2) * mm, "end": v(-7.5, 1.4) * mm});
            skLineSegment(sketch, "E5.0.1.89", {"start": v(-17.5, 1.2) * mm, "end": v(-17, 1.2) * mm});
            skLineSegment(sketch, "E5.0.1.90", {"start": v(-3.5, 0.8) * mm, "end": v(-3.5, 1) * mm});
            skLineSegment(sketch, "E5.0.1.91", {"start": v(-13.5, 1.2) * mm, "end": v(-13.5, 1.4) * mm});
            skLineSegment(sketch, "E5.0.1.92", {"start": v(-4, 1) * mm, "end": v(-3.5, 1) * mm});
            skLineSegment(sketch, "E5.0.1.93", {"start": v(-4.5, 0.8) * mm, "end": v(-4.5, 1) * mm});
            skLineSegment(sketch, "E5.0.1.94", {"start": v(-11.5, 0.8) * mm, "end": v(-11.5, 1) * mm});
            skLineSegment(sketch, "E5.0.1.95", {"start": v(-17.5, 1.2) * mm, "end": v(-17.5, 1.4) * mm});
            skLineSegment(sketch, "E5.0.1.96", {"start": v(-16, 0.8) * mm, "end": v(-16, 1) * mm});
            skLineSegment(sketch, "E5.0.1.97", {"start": v(-3.5, 1.2) * mm, "end": v(-3, 1.2) * mm});
            skLineSegment(sketch, "E5.0.1.98", {"start": v(-1.5, 0.8) * mm, "end": v(-1.5, 1) * mm});
            skLineSegment(sketch, "E5.0.1.99", {"start": v(-18, 0.8) * mm, "end": v(-18, 1) * mm});
            skLineSegment(sketch, "E5.0.1.100", {"start": v(-10, 0.8) * mm, "end": v(-10, 1) * mm});
            skLineSegment(sketch, "E5.0.1.101", {"start": v(-4.5, 1.2) * mm, "end": v(-4, 1.2) * mm});
            skLineSegment(sketch, "E5.0.1.102", {"start": v(-19, 0.8) * mm, "end": v(-19, 1) * mm});
            skLineSegment(sketch, "E5.0.1.103", {"start": v(-14, 1) * mm, "end": v(-13.5, 1) * mm});
            skLineSegment(sketch, "E5.0.1.104", {"start": v(-12.5, 0.8) * mm, "end": v(-12.5, 1) * mm});
            skLineSegment(sketch, "E5.0.1.105", {"start": v(-12.5, 1.2) * mm, "end": v(-12.5, 1.4) * mm});
            skLineSegment(sketch, "E5.0.1.106", {"start": v(-2, 1) * mm, "end": v(-1.5, 1) * mm});
            skLineSegment(sketch, "E5.0.1.107", {"start": v(-12, 1) * mm, "end": v(-11.5, 1) * mm});
            skLineSegment(sketch, "E5.0.1.108", {"start": v(-8.5, 0.8) * mm, "end": v(-8.5, 1) * mm});
            skLineSegment(sketch, "E5.0.1.109", {"start": v(-0.5, 0.8) * mm, "end": v(-0.5, 1) * mm});
            skLineSegment(sketch, "E5.0.1.110", {"start": v(-9.5, 1.2) * mm, "end": v(-9, 1.2) * mm});
            skLineSegment(sketch, "E5.0.1.111", {"start": v(-17, 1.2) * mm, "end": v(-17, 1.4) * mm});
            skLineSegment(sketch, "E5.0.1.112", {"start": v(-13.5, 1.2) * mm, "end": v(-13, 1.2) * mm});
            skLineSegment(sketch, "E5.0.1.113", {"start": v(-4, 0.8) * mm, "end": v(-4, 1) * mm});
            skLineSegment(sketch, "E5.0.1.114", {"start": v(-9.5, 1.2) * mm, "end": v(-9.5, 1.4) * mm});
            skLineSegment(sketch, "E5.0.1.115", {"start": v(-1.5, 1.2) * mm, "end": v(-1.5, 1.4) * mm});
            skLineSegment(sketch, "E5.0.1.116", {"start": v(-8, 1) * mm, "end": v(-7.5, 1) * mm});
            skLineSegment(sketch, "E5.0.1.117", {"start": v(-18, 1) * mm, "end": v(-17.5, 1) * mm});
            skLineSegment(sketch, "E5.0.1.118", {"start": v(-7.5, 1.2) * mm, "end": v(-7, 1.2) * mm});
            skLineSegment(sketch, "E5.0.1.119", {"start": v(-13.5, 0.8) * mm, "end": v(-13.5, 1) * mm});
            skLineSegment(sketch, "E5.0.1.120", {"start": v(-5.5, 0.8) * mm, "end": v(-5.5, 1) * mm});
            skLineSegment(sketch, "E5.0.1.121", {"start": v(-0.5, 1.2) * mm, "end": v(-0.5, 1.4) * mm});
            skLineSegment(sketch, "E5.0.1.122", {"start": v(-8.5, 1.2) * mm, "end": v(-8.5, 1.4) * mm});
            skLineSegment(sketch, "E5.0.1.123", {"start": v(-4.5, 1.2) * mm, "end": v(-4.5, 1.4) * mm});
            skLineSegment(sketch, "E5.0.1.124", {"start": v(-8, 0.8) * mm, "end": v(-8, 1) * mm});
            skLineSegment(sketch, "E5.0.1.125", {"start": v(-2.5, 1.2) * mm, "end": v(-2.5, 1.4) * mm});
            skLineSegment(sketch, "E5.0.1.126", {"start": v(-9, 1.2) * mm, "end": v(-9, 1.4) * mm});
            skLineSegment(sketch, "E5.0.1.127", {"start": v(-5.5, 1.2) * mm, "end": v(-5, 1.2) * mm});
            skLineSegment(sketch, "E5.0.1.128", {"start": v(-13, 1.2) * mm, "end": v(-13, 1.4) * mm});
            skLineSegment(sketch, "E5.0.1.129", {"start": v(-1, 1.2) * mm, "end": v(-1, 1.4) * mm});
            skLineSegment(sketch, "E5.0.1.130", {"start": v(-14, 0.8) * mm, "end": v(-14, 1) * mm});
            skLineSegment(sketch, "E5.0.1.131", {"start": v(-6.5, 0.8) * mm, "end": v(-6.5, 1) * mm});
            skLineSegment(sketch, "E5.0.1.132", {"start": v(-10.5, 0.8) * mm, "end": v(-10.5, 1) * mm});
            skLineSegment(sketch, "E5.0.1.133", {"start": v(-18.5, 1.2) * mm, "end": v(-18.5, 1.4) * mm});
            skLineSegment(sketch, "E5.0.1.134", {"start": v(-14.5, 0.8) * mm, "end": v(-14.5, 1) * mm});
            skLineSegment(sketch, "E5.0.1.135", {"start": v(-4, 1.2) * mm, "end": v(-4, 1.4) * mm});
            skLineSegment(sketch, "E5.0.1.136", {"start": v(-6, 0.8) * mm, "end": v(-6, 1) * mm});
            skLineSegment(sketch, "E5.0.1.137", {"start": v(-16.5, 0.8) * mm, "end": v(-16.5, 1) * mm});
            skLineSegment(sketch, "E5.0.1.138", {"start": v(-17, 1) * mm, "end": v(-16.5, 1) * mm});
            skLineSegment(sketch, "E5.0.1.139", {"start": v(-19, 1.2) * mm, "end": v(-19, 1.4) * mm});
            skLineSegment(sketch, "E5.0.1.140", {"start": v(-10, 1) * mm, "end": v(-9.5, 1) * mm});
            skLineSegment(sketch, "E5.0.1.141", {"start": v(-5.5, 1.2) * mm, "end": v(-5.5, 1.4) * mm});
            skLineSegment(sketch, "E5.0.1.142", {"start": v(-15.5, 1.2) * mm, "end": v(-15.5, 1.4) * mm});
            skLineSegment(sketch, "E5.0.1.143", {"start": v(-9.5, 0.8) * mm, "end": v(-9.5, 1) * mm});
            skLineSegment(sketch, "E5.0.1.144", {"start": v(-20, 0.8) * mm, "end": v(-19.5, 0.8) * mm});
            skLineSegment(sketch, "E5.0.1.145", {"start": v(-3, 1.2) * mm, "end": v(-3, 1.4) * mm});
            skLineSegment(sketch, "E5.0.1.146", {"start": v(-12, 0.8) * mm, "end": v(-12, 1) * mm});
            skLineSegment(sketch, "E5.0.1.147", {"start": v(-2, 0.8) * mm, "end": v(-2, 1) * mm});
            skLineSegment(sketch, "E5.0.1.148", {"start": v(-16, 1) * mm, "end": v(-15.5, 1) * mm});
            skLineSegment(sketch, "E5.0.1.149", {"start": v(-11, 1.2) * mm, "end": v(-11, 1.4) * mm});
            skLineSegment(sketch, "E5.0.1.150", {"start": v(-2.5, 0.8) * mm, "end": v(-2.5, 1) * mm});
            skLineSegment(sketch, "E5.0.1.151", {"start": v(-14.5, 1.2) * mm, "end": v(-14.5, 1.4) * mm});
            skLineSegment(sketch, "E5.0.1.152", {"start": v(-15.5, 1.2) * mm, "end": v(-15, 1.2) * mm});
            skLineSegment(sketch, "E5.0.1.153", {"start": v(-11.5, 1.2) * mm, "end": v(-11.5, 1.4) * mm});
            skLineSegment(sketch, "E5.0.1.154", {"start": v(-7, 1.2) * mm, "end": v(-7, 1.4) * mm});
            skLineSegment(sketch, "E5.0.1.155", {"start": v(-15.5, 0.8) * mm, "end": v(-15.5, 1) * mm});
            skLineSegment(sketch, "E5.0.1.156", {"start": v(-2.5, 1.2) * mm, "end": v(-2, 1.2) * mm});
            skLineSegment(sketch, "E5.0.1.157", {"start": v(-16.5, 1.2) * mm, "end": v(-16.5, 1.4) * mm});
            skLineSegment(sketch, "E5.0.1.158", {"start": v(-19.5, 1.2) * mm, "end": v(-19.5, 1.4) * mm});
            skLineSegment(sketch, "E5.0.1.159", {"start": v(-19.5, 1.2) * mm, "end": v(-19, 1.2) * mm});
            skLineSegment(sketch, "E5.0.2.0", {"start": v(-5, 1.8) * mm, "end": v(-4.5, 1.8) * mm});
            skLineSegment(sketch, "E5.0.2.1", {"start": v(-13.5, 2.2) * mm, "end": v(-13, 2.2) * mm});
            skLineSegment(sketch, "E5.0.2.2", {"start": v(-17, 1.6) * mm, "end": v(-16.5, 1.6) * mm});
            skLineSegment(sketch, "E5.0.2.3", {"start": v(-19.5, 2.2) * mm, "end": v(-19, 2.2) * mm});
            skLineSegment(sketch, "E5.0.2.4", {"start": v(-16.5, 2.2) * mm, "end": v(-16, 2.2) * mm});
            skLineSegment(sketch, "E5.0.2.5", {"start": v(-14.5, 2.2) * mm, "end": v(-14, 2.2) * mm});
            skLineSegment(sketch, "E5.0.2.6", {"start": v(-19, 1.6) * mm, "end": v(-18.5, 1.6) * mm});
            skLineSegment(sketch, "E5.0.2.7", {"start": v(-15, 1.6) * mm, "end": v(-14.5, 1.6) * mm});
            skLineSegment(sketch, "E5.0.2.8", {"start": v(-4.5, 2.2) * mm, "end": v(-4, 2.2) * mm});
            skLineSegment(sketch, "E5.0.2.9", {"start": v(-7.5, 2.2) * mm, "end": v(-7, 2.2) * mm});
            skLineSegment(sketch, "E5.0.2.10", {"start": v(-12.5, 2.2) * mm, "end": v(-12, 2.2) * mm});
            skLineSegment(sketch, "E5.0.2.11", {"start": v(-0.5, 2) * mm, "end": v(0, 2) * mm});
            skLineSegment(sketch, "E5.0.2.12", {"start": v(-1.5, 2.2) * mm, "end": v(-1, 2.2) * mm});
            skLineSegment(sketch, "E5.0.2.13", {"start": v(-16, 1.6) * mm, "end": v(-15.5, 1.6) * mm});
            skLineSegment(sketch, "E5.0.2.14", {"start": v(-12, 1.6) * mm, "end": v(-11.5, 1.6) * mm});
            skLineSegment(sketch, "E5.0.2.15", {"start": v(-18.5, 2.2) * mm, "end": v(-18, 2.2) * mm});
            skLineSegment(sketch, "E5.0.2.16", {"start": v(-18.5, 2) * mm, "end": v(-18, 2) * mm});
            skLineSegment(sketch, "E5.0.2.17", {"start": v(-0.5, 2.2) * mm, "end": v(0, 2.2) * mm});
            skLineSegment(sketch, "E5.0.2.18", {"start": v(-13, 1.6) * mm, "end": v(-13, 1.8) * mm});
            skLineSegment(sketch, "E5.0.2.19", {"start": v(-10, 2) * mm, "end": v(-10, 2.2) * mm});
            skLineSegment(sketch, "E5.0.2.20", {"start": v(-1, 1.8) * mm, "end": v(-0.5, 1.8) * mm});
            skLineSegment(sketch, "E5.0.2.21", {"start": v(-11, 1.6) * mm, "end": v(-11, 1.8) * mm});
            skLineSegment(sketch, "E5.0.2.22", {"start": v(-18.5, 1.6) * mm, "end": v(-18.5, 1.8) * mm});
            skLineSegment(sketch, "E5.0.2.23", {"start": v(-7, 1.8) * mm, "end": v(-6.5, 1.8) * mm});
            skLineSegment(sketch, "E5.0.2.24", {"start": v(-17.5, 2.2) * mm, "end": v(-17, 2.2) * mm});
            skLineSegment(sketch, "E5.0.2.25", {"start": v(-13, 1.8) * mm, "end": v(-12.5, 1.8) * mm});
            skLineSegment(sketch, "E5.0.2.26", {"start": v(-20, 1.8) * mm, "end": v(-19.5, 1.8) * mm});
            skLineSegment(sketch, "E5.0.2.27", {"start": v(-16.5, 2) * mm, "end": v(-16, 2) * mm});
            skLineSegment(sketch, "E5.0.2.28", {"start": v(-8.5, 2.2) * mm, "end": v(-8, 2.2) * mm});
            skLineSegment(sketch, "E5.0.2.29", {"start": v(-15, 1.6) * mm, "end": v(-15, 1.8) * mm});
            skLineSegment(sketch, "E5.0.2.30", {"start": v(-8.5, 2) * mm, "end": v(-8, 2) * mm});
            skLineSegment(sketch, "E5.0.2.31", {"start": v(-9.5, 2.2) * mm, "end": v(-9, 2.2) * mm});
            skLineSegment(sketch, "E5.0.2.32", {"start": v(-6.5, 2) * mm, "end": v(-6, 2) * mm});
            skLineSegment(sketch, "E5.0.2.33", {"start": v(-8, 2) * mm, "end": v(-8, 2.2) * mm});
            skLineSegment(sketch, "E5.0.2.34", {"start": v(-16, 2) * mm, "end": v(-16, 2.2) * mm});
            skLineSegment(sketch, "E5.0.2.35", {"start": v(-11.5, 2.2) * mm, "end": v(-11, 2.2) * mm});
            skLineSegment(sketch, "E5.0.2.36", {"start": v(-12.5, 2) * mm, "end": v(-12, 2) * mm});
            skLineSegment(sketch, "E5.0.2.37", {"start": v(-10, 1.6) * mm, "end": v(-9.5, 1.6) * mm});
            skLineSegment(sketch, "E5.0.2.38", {"start": v(-8, 1.6) * mm, "end": v(-7.5, 1.6) * mm});
            skLineSegment(sketch, "E5.0.2.39", {"start": v(-6, 1.6) * mm, "end": v(-5.5, 1.6) * mm});
            skLineSegment(sketch, "E5.0.2.40", {"start": v(-2, 1.6) * mm, "end": v(-1.5, 1.6) * mm});
            skLineSegment(sketch, "E5.0.2.41", {"start": v(-3.5, 2.2) * mm, "end": v(-3, 2.2) * mm});
            skLineSegment(sketch, "E5.0.2.42", {"start": v(-1, 1.6) * mm, "end": v(-1, 1.8) * mm});
            skLineSegment(sketch, "E5.0.2.43", {"start": v(-4, 1.6) * mm, "end": v(-3.5, 1.6) * mm});
            skLineSegment(sketch, "E5.0.2.44", {"start": v(-5, 1.6) * mm, "end": v(-5, 1.8) * mm});
            skLineSegment(sketch, "E5.0.2.45", {"start": v(-9, 1.6) * mm, "end": v(-9, 1.8) * mm});
            skLineSegment(sketch, "E5.0.2.46", {"start": v(-15.5, 2.2) * mm, "end": v(-15, 2.2) * mm});
            skLineSegment(sketch, "E5.0.2.47", {"start": v(-20, 1.6) * mm, "end": v(-20, 1.8) * mm});
            skLineSegment(sketch, "E5.0.2.48", {"start": v(-18, 1.6) * mm, "end": v(-17.5, 1.6) * mm});
            skLineSegment(sketch, "E5.0.2.49", {"start": v(-17, 1.6) * mm, "end": v(-17, 1.8) * mm});
            skLineSegment(sketch, "E5.0.2.50", {"start": v(-19, 1.8) * mm, "end": v(-18.5, 1.8) * mm});
            skLineSegment(sketch, "E5.0.2.51", {"start": v(-7, 1.6) * mm, "end": v(-7, 1.8) * mm});
            skLineSegment(sketch, "E5.0.2.52", {"start": v(-19.5, 1.6) * mm, "end": v(-19.5, 1.8) * mm});
            skLineSegment(sketch, "E5.0.2.53", {"start": v(-6, 2) * mm, "end": v(-6, 2.2) * mm});
            skLineSegment(sketch, "E5.0.2.54", {"start": v(-14, 2) * mm, "end": v(-14, 2.2) * mm});
            skLineSegment(sketch, "E5.0.2.55", {"start": v(-18, 2) * mm, "end": v(-18, 2.2) * mm});
            skLineSegment(sketch, "E5.0.2.56", {"start": v(-1, 1.6) * mm, "end": v(-0.5, 1.6) * mm});
            skLineSegment(sketch, "E5.0.2.57", {"start": v(-9, 1.6) * mm, "end": v(-8.5, 1.6) * mm});
            skLineSegment(sketch, "E5.0.2.58", {"start": v(-11, 1.8) * mm, "end": v(-10.5, 1.8) * mm});
            skLineSegment(sketch, "E5.0.2.59", {"start": v(-2.5, 2.2) * mm, "end": v(-2, 2.2) * mm});
            skLineSegment(sketch, "E5.0.2.60", {"start": v(-9, 1.8) * mm, "end": v(-8.5, 1.8) * mm});
            skLineSegment(sketch, "E5.0.2.61", {"start": v(-11, 1.6) * mm, "end": v(-10.5, 1.6) * mm});
            skLineSegment(sketch, "E5.0.2.62", {"start": v(-3, 1.6) * mm, "end": v(-3, 1.8) * mm});
            skLineSegment(sketch, "E5.0.2.63", {"start": v(0, 2) * mm, "end": v(0, 2.2) * mm});
            skLineSegment(sketch, "E5.0.2.64", {"start": v(-10.5, 2.2) * mm, "end": v(-10, 2.2) * mm});
            skLineSegment(sketch, "E5.0.2.65", {"start": v(-14.5, 2) * mm, "end": v(-14, 2) * mm});
            skLineSegment(sketch, "E5.0.2.66", {"start": v(-10.5, 2) * mm, "end": v(-10, 2) * mm});
            skLineSegment(sketch, "E5.0.2.67", {"start": v(-5, 1.6) * mm, "end": v(-4.5, 1.6) * mm});
            skLineSegment(sketch, "E5.0.2.68", {"start": v(-3, 1.8) * mm, "end": v(-2.5, 1.8) * mm});
            skLineSegment(sketch, "E5.0.2.69", {"start": v(-14, 1.6) * mm, "end": v(-13.5, 1.6) * mm});
            skLineSegment(sketch, "E5.0.2.70", {"start": v(-6.5, 2.2) * mm, "end": v(-6, 2.2) * mm});
            skLineSegment(sketch, "E5.0.2.71", {"start": v(-13, 1.6) * mm, "end": v(-12.5, 1.6) * mm});
            skLineSegment(sketch, "E5.0.2.72", {"start": v(-15, 1.8) * mm, "end": v(-14.5, 1.8) * mm});
            skLineSegment(sketch, "E5.0.2.73", {"start": v(-12, 2) * mm, "end": v(-12, 2.2) * mm});
            skLineSegment(sketch, "E5.0.2.74", {"start": v(-7, 1.6) * mm, "end": v(-6.5, 1.6) * mm});
            skLineSegment(sketch, "E5.0.2.75", {"start": v(-5.5, 2.2) * mm, "end": v(-5, 2.2) * mm});
            skLineSegment(sketch, "E5.0.2.76", {"start": v(-3, 1.6) * mm, "end": v(-2.5, 1.6) * mm});
            skLineSegment(sketch, "E5.0.2.77", {"start": v(-3.5, 2) * mm, "end": v(-3.5, 2.2) * mm});
            skLineSegment(sketch, "E5.0.2.78", {"start": v(-5, 2) * mm, "end": v(-5, 2.2) * mm});
            skLineSegment(sketch, "E5.0.2.79", {"start": v(-6, 1.8) * mm, "end": v(-5.5, 1.8) * mm});
            skLineSegment(sketch, "E5.0.2.80", {"start": v(-6.5, 2) * mm, "end": v(-6.5, 2.2) * mm});
            skLineSegment(sketch, "E5.0.2.81", {"start": v(-2, 2) * mm, "end": v(-2, 2.2) * mm});
            skLineSegment(sketch, "E5.0.2.82", {"start": v(-15, 2) * mm, "end": v(-15, 2.2) * mm});
            skLineSegment(sketch, "E5.0.2.83", {"start": v(-7.5, 1.6) * mm, "end": v(-7.5, 1.8) * mm});
            skLineSegment(sketch, "E5.0.2.84", {"start": v(-10.5, 2) * mm, "end": v(-10.5, 2.2) * mm});
            skLineSegment(sketch, "E5.0.2.85", {"start": v(-11.5, 2) * mm, "end": v(-11, 2) * mm});
            skLineSegment(sketch, "E5.0.2.86", {"start": v(-1.5, 2) * mm, "end": v(-1, 2) * mm});
            skLineSegment(sketch, "E5.0.2.87", {"start": v(-17.5, 1.6) * mm, "end": v(-17.5, 1.8) * mm});
            skLineSegment(sketch, "E5.0.2.88", {"start": v(-7.5, 2) * mm, "end": v(-7.5, 2.2) * mm});
            skLineSegment(sketch, "E5.0.2.89", {"start": v(-17.5, 2) * mm, "end": v(-17, 2) * mm});
            skLineSegment(sketch, "E5.0.2.90", {"start": v(-3.5, 1.6) * mm, "end": v(-3.5, 1.8) * mm});
            skLineSegment(sketch, "E5.0.2.91", {"start": v(-13.5, 2) * mm, "end": v(-13.5, 2.2) * mm});
            skLineSegment(sketch, "E5.0.2.92", {"start": v(-4, 1.8) * mm, "end": v(-3.5, 1.8) * mm});
            skLineSegment(sketch, "E5.0.2.93", {"start": v(-4.5, 1.6) * mm, "end": v(-4.5, 1.8) * mm});
            skLineSegment(sketch, "E5.0.2.94", {"start": v(-11.5, 1.6) * mm, "end": v(-11.5, 1.8) * mm});
            skLineSegment(sketch, "E5.0.2.95", {"start": v(-17.5, 2) * mm, "end": v(-17.5, 2.2) * mm});
            skLineSegment(sketch, "E5.0.2.96", {"start": v(-16, 1.6) * mm, "end": v(-16, 1.8) * mm});
            skLineSegment(sketch, "E5.0.2.97", {"start": v(-3.5, 2) * mm, "end": v(-3, 2) * mm});
            skLineSegment(sketch, "E5.0.2.98", {"start": v(-1.5, 1.6) * mm, "end": v(-1.5, 1.8) * mm});
            skLineSegment(sketch, "E5.0.2.99", {"start": v(-18, 1.6) * mm, "end": v(-18, 1.8) * mm});
            skLineSegment(sketch, "E5.0.2.100", {"start": v(-10, 1.6) * mm, "end": v(-10, 1.8) * mm});
            skLineSegment(sketch, "E5.0.2.101", {"start": v(-4.5, 2) * mm, "end": v(-4, 2) * mm});
            skLineSegment(sketch, "E5.0.2.102", {"start": v(-19, 1.6) * mm, "end": v(-19, 1.8) * mm});
            skLineSegment(sketch, "E5.0.2.103", {"start": v(-14, 1.8) * mm, "end": v(-13.5, 1.8) * mm});
            skLineSegment(sketch, "E5.0.2.104", {"start": v(-12.5, 1.6) * mm, "end": v(-12.5, 1.8) * mm});
            skLineSegment(sketch, "E5.0.2.105", {"start": v(-12.5, 2) * mm, "end": v(-12.5, 2.2) * mm});
            skLineSegment(sketch, "E5.0.2.106", {"start": v(-2, 1.8) * mm, "end": v(-1.5, 1.8) * mm});
            skLineSegment(sketch, "E5.0.2.107", {"start": v(-12, 1.8) * mm, "end": v(-11.5, 1.8) * mm});
            skLineSegment(sketch, "E5.0.2.108", {"start": v(-8.5, 1.6) * mm, "end": v(-8.5, 1.8) * mm});
            skLineSegment(sketch, "E5.0.2.109", {"start": v(-0.5, 1.6) * mm, "end": v(-0.5, 1.8) * mm});
            skLineSegment(sketch, "E5.0.2.110", {"start": v(-9.5, 2) * mm, "end": v(-9, 2) * mm});
            skLineSegment(sketch, "E5.0.2.111", {"start": v(-17, 2) * mm, "end": v(-17, 2.2) * mm});
            skLineSegment(sketch, "E5.0.2.112", {"start": v(-13.5, 2) * mm, "end": v(-13, 2) * mm});
            skLineSegment(sketch, "E5.0.2.113", {"start": v(-4, 1.6) * mm, "end": v(-4, 1.8) * mm});
            skLineSegment(sketch, "E5.0.2.114", {"start": v(-9.5, 2) * mm, "end": v(-9.5, 2.2) * mm});
            skLineSegment(sketch, "E5.0.2.115", {"start": v(-1.5, 2) * mm, "end": v(-1.5, 2.2) * mm});
            skLineSegment(sketch, "E5.0.2.116", {"start": v(-8, 1.8) * mm, "end": v(-7.5, 1.8) * mm});
            skLineSegment(sketch, "E5.0.2.117", {"start": v(-18, 1.8) * mm, "end": v(-17.5, 1.8) * mm});
            skLineSegment(sketch, "E5.0.2.118", {"start": v(-7.5, 2) * mm, "end": v(-7, 2) * mm});
            skLineSegment(sketch, "E5.0.2.119", {"start": v(-13.5, 1.6) * mm, "end": v(-13.5, 1.8) * mm});
            skLineSegment(sketch, "E5.0.2.120", {"start": v(-5.5, 1.6) * mm, "end": v(-5.5, 1.8) * mm});
            skLineSegment(sketch, "E5.0.2.121", {"start": v(-0.5, 2) * mm, "end": v(-0.5, 2.2) * mm});
            skLineSegment(sketch, "E5.0.2.122", {"start": v(-8.5, 2) * mm, "end": v(-8.5, 2.2) * mm});
            skLineSegment(sketch, "E5.0.2.123", {"start": v(-4.5, 2) * mm, "end": v(-4.5, 2.2) * mm});
            skLineSegment(sketch, "E5.0.2.124", {"start": v(-8, 1.6) * mm, "end": v(-8, 1.8) * mm});
            skLineSegment(sketch, "E5.0.2.125", {"start": v(-2.5, 2) * mm, "end": v(-2.5, 2.2) * mm});
            skLineSegment(sketch, "E5.0.2.126", {"start": v(-9, 2) * mm, "end": v(-9, 2.2) * mm});
            skLineSegment(sketch, "E5.0.2.127", {"start": v(-5.5, 2) * mm, "end": v(-5, 2) * mm});
            skLineSegment(sketch, "E5.0.2.128", {"start": v(-13, 2) * mm, "end": v(-13, 2.2) * mm});
            skLineSegment(sketch, "E5.0.2.129", {"start": v(-1, 2) * mm, "end": v(-1, 2.2) * mm});
            skLineSegment(sketch, "E5.0.2.130", {"start": v(-14, 1.6) * mm, "end": v(-14, 1.8) * mm});
            skLineSegment(sketch, "E5.0.2.131", {"start": v(-6.5, 1.6) * mm, "end": v(-6.5, 1.8) * mm});
            skLineSegment(sketch, "E5.0.2.132", {"start": v(-10.5, 1.6) * mm, "end": v(-10.5, 1.8) * mm});
            skLineSegment(sketch, "E5.0.2.133", {"start": v(-18.5, 2) * mm, "end": v(-18.5, 2.2) * mm});
            skLineSegment(sketch, "E5.0.2.134", {"start": v(-14.5, 1.6) * mm, "end": v(-14.5, 1.8) * mm});
            skLineSegment(sketch, "E5.0.2.135", {"start": v(-4, 2) * mm, "end": v(-4, 2.2) * mm});
            skLineSegment(sketch, "E5.0.2.136", {"start": v(-6, 1.6) * mm, "end": v(-6, 1.8) * mm});
            skLineSegment(sketch, "E5.0.2.137", {"start": v(-16.5, 1.6) * mm, "end": v(-16.5, 1.8) * mm});
            skLineSegment(sketch, "E5.0.2.138", {"start": v(-17, 1.8) * mm, "end": v(-16.5, 1.8) * mm});
            skLineSegment(sketch, "E5.0.2.139", {"start": v(-19, 2) * mm, "end": v(-19, 2.2) * mm});
            skLineSegment(sketch, "E5.0.2.140", {"start": v(-10, 1.8) * mm, "end": v(-9.5, 1.8) * mm});
            skLineSegment(sketch, "E5.0.2.141", {"start": v(-5.5, 2) * mm, "end": v(-5.5, 2.2) * mm});
            skLineSegment(sketch, "E5.0.2.142", {"start": v(-15.5, 2) * mm, "end": v(-15.5, 2.2) * mm});
            skLineSegment(sketch, "E5.0.2.143", {"start": v(-9.5, 1.6) * mm, "end": v(-9.5, 1.8) * mm});
            skLineSegment(sketch, "E5.0.2.144", {"start": v(-20, 1.6) * mm, "end": v(-19.5, 1.6) * mm});
            skLineSegment(sketch, "E5.0.2.145", {"start": v(-3, 2) * mm, "end": v(-3, 2.2) * mm});
            skLineSegment(sketch, "E5.0.2.146", {"start": v(-12, 1.6) * mm, "end": v(-12, 1.8) * mm});
            skLineSegment(sketch, "E5.0.2.147", {"start": v(-2, 1.6) * mm, "end": v(-2, 1.8) * mm});
            skLineSegment(sketch, "E5.0.2.148", {"start": v(-16, 1.8) * mm, "end": v(-15.5, 1.8) * mm});
            skLineSegment(sketch, "E5.0.2.149", {"start": v(-11, 2) * mm, "end": v(-11, 2.2) * mm});
            skLineSegment(sketch, "E5.0.2.150", {"start": v(-2.5, 1.6) * mm, "end": v(-2.5, 1.8) * mm});
            skLineSegment(sketch, "E5.0.2.151", {"start": v(-14.5, 2) * mm, "end": v(-14.5, 2.2) * mm});
            skLineSegment(sketch, "E5.0.2.152", {"start": v(-15.5, 2) * mm, "end": v(-15, 2) * mm});
            skLineSegment(sketch, "E5.0.2.153", {"start": v(-11.5, 2) * mm, "end": v(-11.5, 2.2) * mm});
            skLineSegment(sketch, "E5.0.2.154", {"start": v(-7, 2) * mm, "end": v(-7, 2.2) * mm});
            skLineSegment(sketch, "E5.0.2.155", {"start": v(-15.5, 1.6) * mm, "end": v(-15.5, 1.8) * mm});
            skLineSegment(sketch, "E5.0.2.156", {"start": v(-2.5, 2) * mm, "end": v(-2, 2) * mm});
            skLineSegment(sketch, "E5.0.2.157", {"start": v(-16.5, 2) * mm, "end": v(-16.5, 2.2) * mm});
            skLineSegment(sketch, "E5.0.2.158", {"start": v(-19.5, 2) * mm, "end": v(-19.5, 2.2) * mm});
            skLineSegment(sketch, "E5.0.2.159", {"start": v(-19.5, 2) * mm, "end": v(-19, 2) * mm});
            skLineSegment(sketch, "E5.0.3.0", {"start": v(-5, 2.6) * mm, "end": v(-4.5, 2.6) * mm});
            skLineSegment(sketch, "E5.0.3.1", {"start": v(-13.5, 3) * mm, "end": v(-13, 3) * mm});
            skLineSegment(sketch, "E5.0.3.2", {"start": v(-17, 2.4) * mm, "end": v(-16.5, 2.4) * mm});
            skLineSegment(sketch, "E5.0.3.3", {"start": v(-19.5, 3) * mm, "end": v(-19, 3) * mm});
            skLineSegment(sketch, "E5.0.3.4", {"start": v(-16.5, 3) * mm, "end": v(-16, 3) * mm});
            skLineSegment(sketch, "E5.0.3.5", {"start": v(-14.5, 3) * mm, "end": v(-14, 3) * mm});
            skLineSegment(sketch, "E5.0.3.6", {"start": v(-19, 2.4) * mm, "end": v(-18.5, 2.4) * mm});
            skLineSegment(sketch, "E5.0.3.7", {"start": v(-15, 2.4) * mm, "end": v(-14.5, 2.4) * mm});
            skLineSegment(sketch, "E5.0.3.8", {"start": v(-4.5, 3) * mm, "end": v(-4, 3) * mm});
            skLineSegment(sketch, "E5.0.3.9", {"start": v(-7.5, 3) * mm, "end": v(-7, 3) * mm});
            skLineSegment(sketch, "E5.0.3.10", {"start": v(-12.5, 3) * mm, "end": v(-12, 3) * mm});
            skLineSegment(sketch, "E5.0.3.11", {"start": v(-0.5, 2.8) * mm, "end": v(0, 2.8) * mm});
            skLineSegment(sketch, "E5.0.3.12", {"start": v(-1.5, 3) * mm, "end": v(-1, 3) * mm});
            skLineSegment(sketch, "E5.0.3.13", {"start": v(-16, 2.4) * mm, "end": v(-15.5, 2.4) * mm});
            skLineSegment(sketch, "E5.0.3.14", {"start": v(-12, 2.4) * mm, "end": v(-11.5, 2.4) * mm});
            skLineSegment(sketch, "E5.0.3.15", {"start": v(-18.5, 3) * mm, "end": v(-18, 3) * mm});
            skLineSegment(sketch, "E5.0.3.16", {"start": v(-18.5, 2.8) * mm, "end": v(-18, 2.8) * mm});
            skLineSegment(sketch, "E5.0.3.17", {"start": v(-0.5, 3) * mm, "end": v(0, 3) * mm});
            skLineSegment(sketch, "E5.0.3.18", {"start": v(-13, 2.4) * mm, "end": v(-13, 2.6) * mm});
            skLineSegment(sketch, "E5.0.3.19", {"start": v(-10, 2.8) * mm, "end": v(-10, 3) * mm});
            skLineSegment(sketch, "E5.0.3.20", {"start": v(-1, 2.6) * mm, "end": v(-0.5, 2.6) * mm});
            skLineSegment(sketch, "E5.0.3.21", {"start": v(-11, 2.4) * mm, "end": v(-11, 2.6) * mm});
            skLineSegment(sketch, "E5.0.3.22", {"start": v(-18.5, 2.4) * mm, "end": v(-18.5, 2.6) * mm});
            skLineSegment(sketch, "E5.0.3.23", {"start": v(-7, 2.6) * mm, "end": v(-6.5, 2.6) * mm});
            skLineSegment(sketch, "E5.0.3.24", {"start": v(-17.5, 3) * mm, "end": v(-17, 3) * mm});
            skLineSegment(sketch, "E5.0.3.25", {"start": v(-13, 2.6) * mm, "end": v(-12.5, 2.6) * mm});
            skLineSegment(sketch, "E5.0.3.26", {"start": v(-20, 2.6) * mm, "end": v(-19.5, 2.6) * mm});
            skLineSegment(sketch, "E5.0.3.27", {"start": v(-16.5, 2.8) * mm, "end": v(-16, 2.8) * mm});
            skLineSegment(sketch, "E5.0.3.28", {"start": v(-8.5, 3) * mm, "end": v(-8, 3) * mm});
            skLineSegment(sketch, "E5.0.3.29", {"start": v(-15, 2.4) * mm, "end": v(-15, 2.6) * mm});
            skLineSegment(sketch, "E5.0.3.30", {"start": v(-8.5, 2.8) * mm, "end": v(-8, 2.8) * mm});
            skLineSegment(sketch, "E5.0.3.31", {"start": v(-9.5, 3) * mm, "end": v(-9, 3) * mm});
            skLineSegment(sketch, "E5.0.3.32", {"start": v(-6.5, 2.8) * mm, "end": v(-6, 2.8) * mm});
            skLineSegment(sketch, "E5.0.3.33", {"start": v(-8, 2.8) * mm, "end": v(-8, 3) * mm});
            skLineSegment(sketch, "E5.0.3.34", {"start": v(-16, 2.8) * mm, "end": v(-16, 3) * mm});
            skLineSegment(sketch, "E5.0.3.35", {"start": v(-11.5, 3) * mm, "end": v(-11, 3) * mm});
            skLineSegment(sketch, "E5.0.3.36", {"start": v(-12.5, 2.8) * mm, "end": v(-12, 2.8) * mm});
            skLineSegment(sketch, "E5.0.3.37", {"start": v(-10, 2.4) * mm, "end": v(-9.5, 2.4) * mm});
            skLineSegment(sketch, "E5.0.3.38", {"start": v(-8, 2.4) * mm, "end": v(-7.5, 2.4) * mm});
            skLineSegment(sketch, "E5.0.3.39", {"start": v(-6, 2.4) * mm, "end": v(-5.5, 2.4) * mm});
            skLineSegment(sketch, "E5.0.3.40", {"start": v(-2, 2.4) * mm, "end": v(-1.5, 2.4) * mm});
            skLineSegment(sketch, "E5.0.3.41", {"start": v(-3.5, 3) * mm, "end": v(-3, 3) * mm});
            skLineSegment(sketch, "E5.0.3.42", {"start": v(-1, 2.4) * mm, "end": v(-1, 2.6) * mm});
            skLineSegment(sketch, "E5.0.3.43", {"start": v(-4, 2.4) * mm, "end": v(-3.5, 2.4) * mm});
            skLineSegment(sketch, "E5.0.3.44", {"start": v(-5, 2.4) * mm, "end": v(-5, 2.6) * mm});
            skLineSegment(sketch, "E5.0.3.45", {"start": v(-9, 2.4) * mm, "end": v(-9, 2.6) * mm});
            skLineSegment(sketch, "E5.0.3.46", {"start": v(-15.5, 3) * mm, "end": v(-15, 3) * mm});
            skLineSegment(sketch, "E5.0.3.47", {"start": v(-20, 2.4) * mm, "end": v(-20, 2.6) * mm});
            skLineSegment(sketch, "E5.0.3.48", {"start": v(-18, 2.4) * mm, "end": v(-17.5, 2.4) * mm});
            skLineSegment(sketch, "E5.0.3.49", {"start": v(-17, 2.4) * mm, "end": v(-17, 2.6) * mm});
            skLineSegment(sketch, "E5.0.3.50", {"start": v(-19, 2.6) * mm, "end": v(-18.5, 2.6) * mm});
            skLineSegment(sketch, "E5.0.3.51", {"start": v(-7, 2.4) * mm, "end": v(-7, 2.6) * mm});
            skLineSegment(sketch, "E5.0.3.52", {"start": v(-19.5, 2.4) * mm, "end": v(-19.5, 2.6) * mm});
            skLineSegment(sketch, "E5.0.3.53", {"start": v(-6, 2.8) * mm, "end": v(-6, 3) * mm});
            skLineSegment(sketch, "E5.0.3.54", {"start": v(-14, 2.8) * mm, "end": v(-14, 3) * mm});
            skLineSegment(sketch, "E5.0.3.55", {"start": v(-18, 2.8) * mm, "end": v(-18, 3) * mm});
            skLineSegment(sketch, "E5.0.3.56", {"start": v(-1, 2.4) * mm, "end": v(-0.5, 2.4) * mm});
            skLineSegment(sketch, "E5.0.3.57", {"start": v(-9, 2.4) * mm, "end": v(-8.5, 2.4) * mm});
            skLineSegment(sketch, "E5.0.3.58", {"start": v(-11, 2.6) * mm, "end": v(-10.5, 2.6) * mm});
            skLineSegment(sketch, "E5.0.3.59", {"start": v(-2.5, 3) * mm, "end": v(-2, 3) * mm});
            skLineSegment(sketch, "E5.0.3.60", {"start": v(-9, 2.6) * mm, "end": v(-8.5, 2.6) * mm});
            skLineSegment(sketch, "E5.0.3.61", {"start": v(-11, 2.4) * mm, "end": v(-10.5, 2.4) * mm});
            skLineSegment(sketch, "E5.0.3.62", {"start": v(-3, 2.4) * mm, "end": v(-3, 2.6) * mm});
            skLineSegment(sketch, "E5.0.3.63", {"start": v(0, 2.8) * mm, "end": v(0, 3) * mm});
            skLineSegment(sketch, "E5.0.3.64", {"start": v(-10.5, 3) * mm, "end": v(-10, 3) * mm});
            skLineSegment(sketch, "E5.0.3.65", {"start": v(-14.5, 2.8) * mm, "end": v(-14, 2.8) * mm});
            skLineSegment(sketch, "E5.0.3.66", {"start": v(-10.5, 2.8) * mm, "end": v(-10, 2.8) * mm});
            skLineSegment(sketch, "E5.0.3.67", {"start": v(-5, 2.4) * mm, "end": v(-4.5, 2.4) * mm});
            skLineSegment(sketch, "E5.0.3.68", {"start": v(-3, 2.6) * mm, "end": v(-2.5, 2.6) * mm});
            skLineSegment(sketch, "E5.0.3.69", {"start": v(-14, 2.4) * mm, "end": v(-13.5, 2.4) * mm});
            skLineSegment(sketch, "E5.0.3.70", {"start": v(-6.5, 3) * mm, "end": v(-6, 3) * mm});
            skLineSegment(sketch, "E5.0.3.71", {"start": v(-13, 2.4) * mm, "end": v(-12.5, 2.4) * mm});
            skLineSegment(sketch, "E5.0.3.72", {"start": v(-15, 2.6) * mm, "end": v(-14.5, 2.6) * mm});
            skLineSegment(sketch, "E5.0.3.73", {"start": v(-12, 2.8) * mm, "end": v(-12, 3) * mm});
            skLineSegment(sketch, "E5.0.3.74", {"start": v(-7, 2.4) * mm, "end": v(-6.5, 2.4) * mm});
            skLineSegment(sketch, "E5.0.3.75", {"start": v(-5.5, 3) * mm, "end": v(-5, 3) * mm});
            skLineSegment(sketch, "E5.0.3.76", {"start": v(-3, 2.4) * mm, "end": v(-2.5, 2.4) * mm});
            skLineSegment(sketch, "E5.0.3.77", {"start": v(-3.5, 2.8) * mm, "end": v(-3.5, 3) * mm});
            skLineSegment(sketch, "E5.0.3.78", {"start": v(-5, 2.8) * mm, "end": v(-5, 3) * mm});
            skLineSegment(sketch, "E5.0.3.79", {"start": v(-6, 2.6) * mm, "end": v(-5.5, 2.6) * mm});
            skLineSegment(sketch, "E5.0.3.80", {"start": v(-6.5, 2.8) * mm, "end": v(-6.5, 3) * mm});
            skLineSegment(sketch, "E5.0.3.81", {"start": v(-2, 2.8) * mm, "end": v(-2, 3) * mm});
            skLineSegment(sketch, "E5.0.3.82", {"start": v(-15, 2.8) * mm, "end": v(-15, 3) * mm});
            skLineSegment(sketch, "E5.0.3.83", {"start": v(-7.5, 2.4) * mm, "end": v(-7.5, 2.6) * mm});
            skLineSegment(sketch, "E5.0.3.84", {"start": v(-10.5, 2.8) * mm, "end": v(-10.5, 3) * mm});
            skLineSegment(sketch, "E5.0.3.85", {"start": v(-11.5, 2.8) * mm, "end": v(-11, 2.8) * mm});
            skLineSegment(sketch, "E5.0.3.86", {"start": v(-1.5, 2.8) * mm, "end": v(-1, 2.8) * mm});
            skLineSegment(sketch, "E5.0.3.87", {"start": v(-17.5, 2.4) * mm, "end": v(-17.5, 2.6) * mm});
            skLineSegment(sketch, "E5.0.3.88", {"start": v(-7.5, 2.8) * mm, "end": v(-7.5, 3) * mm});
            skLineSegment(sketch, "E5.0.3.89", {"start": v(-17.5, 2.8) * mm, "end": v(-17, 2.8) * mm});
            skLineSegment(sketch, "E5.0.3.90", {"start": v(-3.5, 2.4) * mm, "end": v(-3.5, 2.6) * mm});
            skLineSegment(sketch, "E5.0.3.91", {"start": v(-13.5, 2.8) * mm, "end": v(-13.5, 3) * mm});
            skLineSegment(sketch, "E5.0.3.92", {"start": v(-4, 2.6) * mm, "end": v(-3.5, 2.6) * mm});
            skLineSegment(sketch, "E5.0.3.93", {"start": v(-4.5, 2.4) * mm, "end": v(-4.5, 2.6) * mm});
            skLineSegment(sketch, "E5.0.3.94", {"start": v(-11.5, 2.4) * mm, "end": v(-11.5, 2.6) * mm});
            skLineSegment(sketch, "E5.0.3.95", {"start": v(-17.5, 2.8) * mm, "end": v(-17.5, 3) * mm});
            skLineSegment(sketch, "E5.0.3.96", {"start": v(-16, 2.4) * mm, "end": v(-16, 2.6) * mm});
            skLineSegment(sketch, "E5.0.3.97", {"start": v(-3.5, 2.8) * mm, "end": v(-3, 2.8) * mm});
            skLineSegment(sketch, "E5.0.3.98", {"start": v(-1.5, 2.4) * mm, "end": v(-1.5, 2.6) * mm});
            skLineSegment(sketch, "E5.0.3.99", {"start": v(-18, 2.4) * mm, "end": v(-18, 2.6) * mm});
            skLineSegment(sketch, "E5.0.3.100", {"start": v(-10, 2.4) * mm, "end": v(-10, 2.6) * mm});
            skLineSegment(sketch, "E5.0.3.101", {"start": v(-4.5, 2.8) * mm, "end": v(-4, 2.8) * mm});
            skLineSegment(sketch, "E5.0.3.102", {"start": v(-19, 2.4) * mm, "end": v(-19, 2.6) * mm});
            skLineSegment(sketch, "E5.0.3.103", {"start": v(-14, 2.6) * mm, "end": v(-13.5, 2.6) * mm});
            skLineSegment(sketch, "E5.0.3.104", {"start": v(-12.5, 2.4) * mm, "end": v(-12.5, 2.6) * mm});
            skLineSegment(sketch, "E5.0.3.105", {"start": v(-12.5, 2.8) * mm, "end": v(-12.5, 3) * mm});
            skLineSegment(sketch, "E5.0.3.106", {"start": v(-2, 2.6) * mm, "end": v(-1.5, 2.6) * mm});
            skLineSegment(sketch, "E5.0.3.107", {"start": v(-12, 2.6) * mm, "end": v(-11.5, 2.6) * mm});
            skLineSegment(sketch, "E5.0.3.108", {"start": v(-8.5, 2.4) * mm, "end": v(-8.5, 2.6) * mm});
            skLineSegment(sketch, "E5.0.3.109", {"start": v(-0.5, 2.4) * mm, "end": v(-0.5, 2.6) * mm});
            skLineSegment(sketch, "E5.0.3.110", {"start": v(-9.5, 2.8) * mm, "end": v(-9, 2.8) * mm});
            skLineSegment(sketch, "E5.0.3.111", {"start": v(-17, 2.8) * mm, "end": v(-17, 3) * mm});
            skLineSegment(sketch, "E5.0.3.112", {"start": v(-13.5, 2.8) * mm, "end": v(-13, 2.8) * mm});
            skLineSegment(sketch, "E5.0.3.113", {"start": v(-4, 2.4) * mm, "end": v(-4, 2.6) * mm});
            skLineSegment(sketch, "E5.0.3.114", {"start": v(-9.5, 2.8) * mm, "end": v(-9.5, 3) * mm});
            skLineSegment(sketch, "E5.0.3.115", {"start": v(-1.5, 2.8) * mm, "end": v(-1.5, 3) * mm});
            skLineSegment(sketch, "E5.0.3.116", {"start": v(-8, 2.6) * mm, "end": v(-7.5, 2.6) * mm});
            skLineSegment(sketch, "E5.0.3.117", {"start": v(-18, 2.6) * mm, "end": v(-17.5, 2.6) * mm});
            skLineSegment(sketch, "E5.0.3.118", {"start": v(-7.5, 2.8) * mm, "end": v(-7, 2.8) * mm});
            skLineSegment(sketch, "E5.0.3.119", {"start": v(-13.5, 2.4) * mm, "end": v(-13.5, 2.6) * mm});
            skLineSegment(sketch, "E5.0.3.120", {"start": v(-5.5, 2.4) * mm, "end": v(-5.5, 2.6) * mm});
            skLineSegment(sketch, "E5.0.3.121", {"start": v(-0.5, 2.8) * mm, "end": v(-0.5, 3) * mm});
            skLineSegment(sketch, "E5.0.3.122", {"start": v(-8.5, 2.8) * mm, "end": v(-8.5, 3) * mm});
            skLineSegment(sketch, "E5.0.3.123", {"start": v(-4.5, 2.8) * mm, "end": v(-4.5, 3) * mm});
            skLineSegment(sketch, "E5.0.3.124", {"start": v(-8, 2.4) * mm, "end": v(-8, 2.6) * mm});
            skLineSegment(sketch, "E5.0.3.125", {"start": v(-2.5, 2.8) * mm, "end": v(-2.5, 3) * mm});
            skLineSegment(sketch, "E5.0.3.126", {"start": v(-9, 2.8) * mm, "end": v(-9, 3) * mm});
            skLineSegment(sketch, "E5.0.3.127", {"start": v(-5.5, 2.8) * mm, "end": v(-5, 2.8) * mm});
            skLineSegment(sketch, "E5.0.3.128", {"start": v(-13, 2.8) * mm, "end": v(-13, 3) * mm});
            skLineSegment(sketch, "E5.0.3.129", {"start": v(-1, 2.8) * mm, "end": v(-1, 3) * mm});
            skLineSegment(sketch, "E5.0.3.130", {"start": v(-14, 2.4) * mm, "end": v(-14, 2.6) * mm});
            skLineSegment(sketch, "E5.0.3.131", {"start": v(-6.5, 2.4) * mm, "end": v(-6.5, 2.6) * mm});
            skLineSegment(sketch, "E5.0.3.132", {"start": v(-10.5, 2.4) * mm, "end": v(-10.5, 2.6) * mm});
            skLineSegment(sketch, "E5.0.3.133", {"start": v(-18.5, 2.8) * mm, "end": v(-18.5, 3) * mm});
            skLineSegment(sketch, "E5.0.3.134", {"start": v(-14.5, 2.4) * mm, "end": v(-14.5, 2.6) * mm});
            skLineSegment(sketch, "E5.0.3.135", {"start": v(-4, 2.8) * mm, "end": v(-4, 3) * mm});
            skLineSegment(sketch, "E5.0.3.136", {"start": v(-6, 2.4) * mm, "end": v(-6, 2.6) * mm});
            skLineSegment(sketch, "E5.0.3.137", {"start": v(-16.5, 2.4) * mm, "end": v(-16.5, 2.6) * mm});
            skLineSegment(sketch, "E5.0.3.138", {"start": v(-17, 2.6) * mm, "end": v(-16.5, 2.6) * mm});
            skLineSegment(sketch, "E5.0.3.139", {"start": v(-19, 2.8) * mm, "end": v(-19, 3) * mm});
            skLineSegment(sketch, "E5.0.3.140", {"start": v(-10, 2.6) * mm, "end": v(-9.5, 2.6) * mm});
            skLineSegment(sketch, "E5.0.3.141", {"start": v(-5.5, 2.8) * mm, "end": v(-5.5, 3) * mm});
            skLineSegment(sketch, "E5.0.3.142", {"start": v(-15.5, 2.8) * mm, "end": v(-15.5, 3) * mm});
            skLineSegment(sketch, "E5.0.3.143", {"start": v(-9.5, 2.4) * mm, "end": v(-9.5, 2.6) * mm});
            skLineSegment(sketch, "E5.0.3.144", {"start": v(-20, 2.4) * mm, "end": v(-19.5, 2.4) * mm});
            skLineSegment(sketch, "E5.0.3.145", {"start": v(-3, 2.8) * mm, "end": v(-3, 3) * mm});
            skLineSegment(sketch, "E5.0.3.146", {"start": v(-12, 2.4) * mm, "end": v(-12, 2.6) * mm});
            skLineSegment(sketch, "E5.0.3.147", {"start": v(-2, 2.4) * mm, "end": v(-2, 2.6) * mm});
            skLineSegment(sketch, "E5.0.3.148", {"start": v(-16, 2.6) * mm, "end": v(-15.5, 2.6) * mm});
            skLineSegment(sketch, "E5.0.3.149", {"start": v(-11, 2.8) * mm, "end": v(-11, 3) * mm});
            skLineSegment(sketch, "E5.0.3.150", {"start": v(-2.5, 2.4) * mm, "end": v(-2.5, 2.6) * mm});
            skLineSegment(sketch, "E5.0.3.151", {"start": v(-14.5, 2.8) * mm, "end": v(-14.5, 3) * mm});
            skLineSegment(sketch, "E5.0.3.152", {"start": v(-15.5, 2.8) * mm, "end": v(-15, 2.8) * mm});
            skLineSegment(sketch, "E5.0.3.153", {"start": v(-11.5, 2.8) * mm, "end": v(-11.5, 3) * mm});
            skLineSegment(sketch, "E5.0.3.154", {"start": v(-7, 2.8) * mm, "end": v(-7, 3) * mm});
            skLineSegment(sketch, "E5.0.3.155", {"start": v(-15.5, 2.4) * mm, "end": v(-15.5, 2.6) * mm});
            skLineSegment(sketch, "E5.0.3.156", {"start": v(-2.5, 2.8) * mm, "end": v(-2, 2.8) * mm});
            skLineSegment(sketch, "E5.0.3.157", {"start": v(-16.5, 2.8) * mm, "end": v(-16.5, 3) * mm});
            skLineSegment(sketch, "E5.0.3.158", {"start": v(-19.5, 2.8) * mm, "end": v(-19.5, 3) * mm});
            skLineSegment(sketch, "E5.0.3.159", {"start": v(-19.5, 2.8) * mm, "end": v(-19, 2.8) * mm});
            skLineSegment(sketch, "E5.0.4.0", {"start": v(-5, 3.4) * mm, "end": v(-4.5, 3.4) * mm});
            skLineSegment(sketch, "E5.0.4.1", {"start": v(-13.5, 3.8) * mm, "end": v(-13, 3.8) * mm});
            skLineSegment(sketch, "E5.0.4.2", {"start": v(-17, 3.2) * mm, "end": v(-16.5, 3.2) * mm});
            skLineSegment(sketch, "E5.0.4.3", {"start": v(-19.5, 3.8) * mm, "end": v(-19, 3.8) * mm});
            skLineSegment(sketch, "E5.0.4.4", {"start": v(-16.5, 3.8) * mm, "end": v(-16, 3.8) * mm});
            skLineSegment(sketch, "E5.0.4.5", {"start": v(-14.5, 3.8) * mm, "end": v(-14, 3.8) * mm});
            skLineSegment(sketch, "E5.0.4.6", {"start": v(-19, 3.2) * mm, "end": v(-18.5, 3.2) * mm});
            skLineSegment(sketch, "E5.0.4.7", {"start": v(-15, 3.2) * mm, "end": v(-14.5, 3.2) * mm});
            skLineSegment(sketch, "E5.0.4.8", {"start": v(-4.5, 3.8) * mm, "end": v(-4, 3.8) * mm});
            skLineSegment(sketch, "E5.0.4.9", {"start": v(-7.5, 3.8) * mm, "end": v(-7, 3.8) * mm});
            skLineSegment(sketch, "E5.0.4.10", {"start": v(-12.5, 3.8) * mm, "end": v(-12, 3.8) * mm});
            skLineSegment(sketch, "E5.0.4.11", {"start": v(-0.5, 3.6) * mm, "end": v(0, 3.6) * mm});
            skLineSegment(sketch, "E5.0.4.12", {"start": v(-1.5, 3.8) * mm, "end": v(-1, 3.8) * mm});
            skLineSegment(sketch, "E5.0.4.13", {"start": v(-16, 3.2) * mm, "end": v(-15.5, 3.2) * mm});
            skLineSegment(sketch, "E5.0.4.14", {"start": v(-12, 3.2) * mm, "end": v(-11.5, 3.2) * mm});
            skLineSegment(sketch, "E5.0.4.15", {"start": v(-18.5, 3.8) * mm, "end": v(-18, 3.8) * mm});
            skLineSegment(sketch, "E5.0.4.16", {"start": v(-18.5, 3.6) * mm, "end": v(-18, 3.6) * mm});
            skLineSegment(sketch, "E5.0.4.17", {"start": v(-0.5, 3.8) * mm, "end": v(0, 3.8) * mm});
            skLineSegment(sketch, "E5.0.4.18", {"start": v(-13, 3.2) * mm, "end": v(-13, 3.4) * mm});
            skLineSegment(sketch, "E5.0.4.19", {"start": v(-10, 3.6) * mm, "end": v(-10, 3.8) * mm});
            skLineSegment(sketch, "E5.0.4.20", {"start": v(-1, 3.4) * mm, "end": v(-0.5, 3.4) * mm});
            skLineSegment(sketch, "E5.0.4.21", {"start": v(-11, 3.2) * mm, "end": v(-11, 3.4) * mm});
            skLineSegment(sketch, "E5.0.4.22", {"start": v(-18.5, 3.2) * mm, "end": v(-18.5, 3.4) * mm});
            skLineSegment(sketch, "E5.0.4.23", {"start": v(-7, 3.4) * mm, "end": v(-6.5, 3.4) * mm});
            skLineSegment(sketch, "E5.0.4.24", {"start": v(-17.5, 3.8) * mm, "end": v(-17, 3.8) * mm});
            skLineSegment(sketch, "E5.0.4.25", {"start": v(-13, 3.4) * mm, "end": v(-12.5, 3.4) * mm});
            skLineSegment(sketch, "E5.0.4.26", {"start": v(-20, 3.4) * mm, "end": v(-19.5, 3.4) * mm});
            skLineSegment(sketch, "E5.0.4.27", {"start": v(-16.5, 3.6) * mm, "end": v(-16, 3.6) * mm});
            skLineSegment(sketch, "E5.0.4.28", {"start": v(-8.5, 3.8) * mm, "end": v(-8, 3.8) * mm});
            skLineSegment(sketch, "E5.0.4.29", {"start": v(-15, 3.2) * mm, "end": v(-15, 3.4) * mm});
            skLineSegment(sketch, "E5.0.4.30", {"start": v(-8.5, 3.6) * mm, "end": v(-8, 3.6) * mm});
            skLineSegment(sketch, "E5.0.4.31", {"start": v(-9.5, 3.8) * mm, "end": v(-9, 3.8) * mm});
            skLineSegment(sketch, "E5.0.4.32", {"start": v(-6.5, 3.6) * mm, "end": v(-6, 3.6) * mm});
            skLineSegment(sketch, "E5.0.4.33", {"start": v(-8, 3.6) * mm, "end": v(-8, 3.8) * mm});
            skLineSegment(sketch, "E5.0.4.34", {"start": v(-16, 3.6) * mm, "end": v(-16, 3.8) * mm});
            skLineSegment(sketch, "E5.0.4.35", {"start": v(-11.5, 3.8) * mm, "end": v(-11, 3.8) * mm});
            skLineSegment(sketch, "E5.0.4.36", {"start": v(-12.5, 3.6) * mm, "end": v(-12, 3.6) * mm});
            skLineSegment(sketch, "E5.0.4.37", {"start": v(-10, 3.2) * mm, "end": v(-9.5, 3.2) * mm});
            skLineSegment(sketch, "E5.0.4.38", {"start": v(-8, 3.2) * mm, "end": v(-7.5, 3.2) * mm});
            skLineSegment(sketch, "E5.0.4.39", {"start": v(-6, 3.2) * mm, "end": v(-5.5, 3.2) * mm});
            skLineSegment(sketch, "E5.0.4.40", {"start": v(-2, 3.2) * mm, "end": v(-1.5, 3.2) * mm});
            skLineSegment(sketch, "E5.0.4.41", {"start": v(-3.5, 3.8) * mm, "end": v(-3, 3.8) * mm});
            skLineSegment(sketch, "E5.0.4.42", {"start": v(-1, 3.2) * mm, "end": v(-1, 3.4) * mm});
            skLineSegment(sketch, "E5.0.4.43", {"start": v(-4, 3.2) * mm, "end": v(-3.5, 3.2) * mm});
            skLineSegment(sketch, "E5.0.4.44", {"start": v(-5, 3.2) * mm, "end": v(-5, 3.4) * mm});
            skLineSegment(sketch, "E5.0.4.45", {"start": v(-9, 3.2) * mm, "end": v(-9, 3.4) * mm});
            skLineSegment(sketch, "E5.0.4.46", {"start": v(-15.5, 3.8) * mm, "end": v(-15, 3.8) * mm});
            skLineSegment(sketch, "E5.0.4.47", {"start": v(-20, 3.2) * mm, "end": v(-20, 3.4) * mm});
            skLineSegment(sketch, "E5.0.4.48", {"start": v(-18, 3.2) * mm, "end": v(-17.5, 3.2) * mm});
            skLineSegment(sketch, "E5.0.4.49", {"start": v(-17, 3.2) * mm, "end": v(-17, 3.4) * mm});
            skLineSegment(sketch, "E5.0.4.50", {"start": v(-19, 3.4) * mm, "end": v(-18.5, 3.4) * mm});
            skLineSegment(sketch, "E5.0.4.51", {"start": v(-7, 3.2) * mm, "end": v(-7, 3.4) * mm});
            skLineSegment(sketch, "E5.0.4.52", {"start": v(-19.5, 3.2) * mm, "end": v(-19.5, 3.4) * mm});
            skLineSegment(sketch, "E5.0.4.53", {"start": v(-6, 3.6) * mm, "end": v(-6, 3.8) * mm});
            skLineSegment(sketch, "E5.0.4.54", {"start": v(-14, 3.6) * mm, "end": v(-14, 3.8) * mm});
            skLineSegment(sketch, "E5.0.4.55", {"start": v(-18, 3.6) * mm, "end": v(-18, 3.8) * mm});
            skLineSegment(sketch, "E5.0.4.56", {"start": v(-1, 3.2) * mm, "end": v(-0.5, 3.2) * mm});
            skLineSegment(sketch, "E5.0.4.57", {"start": v(-9, 3.2) * mm, "end": v(-8.5, 3.2) * mm});
            skLineSegment(sketch, "E5.0.4.58", {"start": v(-11, 3.4) * mm, "end": v(-10.5, 3.4) * mm});
            skLineSegment(sketch, "E5.0.4.59", {"start": v(-2.5, 3.8) * mm, "end": v(-2, 3.8) * mm});
            skLineSegment(sketch, "E5.0.4.60", {"start": v(-9, 3.4) * mm, "end": v(-8.5, 3.4) * mm});
            skLineSegment(sketch, "E5.0.4.61", {"start": v(-11, 3.2) * mm, "end": v(-10.5, 3.2) * mm});
            skLineSegment(sketch, "E5.0.4.62", {"start": v(-3, 3.2) * mm, "end": v(-3, 3.4) * mm});
            skLineSegment(sketch, "E5.0.4.63", {"start": v(0, 3.6) * mm, "end": v(0, 3.8) * mm});
            skLineSegment(sketch, "E5.0.4.64", {"start": v(-10.5, 3.8) * mm, "end": v(-10, 3.8) * mm});
            skLineSegment(sketch, "E5.0.4.65", {"start": v(-14.5, 3.6) * mm, "end": v(-14, 3.6) * mm});
            skLineSegment(sketch, "E5.0.4.66", {"start": v(-10.5, 3.6) * mm, "end": v(-10, 3.6) * mm});
            skLineSegment(sketch, "E5.0.4.67", {"start": v(-5, 3.2) * mm, "end": v(-4.5, 3.2) * mm});
            skLineSegment(sketch, "E5.0.4.68", {"start": v(-3, 3.4) * mm, "end": v(-2.5, 3.4) * mm});
            skLineSegment(sketch, "E5.0.4.69", {"start": v(-14, 3.2) * mm, "end": v(-13.5, 3.2) * mm});
            skLineSegment(sketch, "E5.0.4.70", {"start": v(-6.5, 3.8) * mm, "end": v(-6, 3.8) * mm});
            skLineSegment(sketch, "E5.0.4.71", {"start": v(-13, 3.2) * mm, "end": v(-12.5, 3.2) * mm});
            skLineSegment(sketch, "E5.0.4.72", {"start": v(-15, 3.4) * mm, "end": v(-14.5, 3.4) * mm});
            skLineSegment(sketch, "E5.0.4.73", {"start": v(-12, 3.6) * mm, "end": v(-12, 3.8) * mm});
            skLineSegment(sketch, "E5.0.4.74", {"start": v(-7, 3.2) * mm, "end": v(-6.5, 3.2) * mm});
            skLineSegment(sketch, "E5.0.4.75", {"start": v(-5.5, 3.8) * mm, "end": v(-5, 3.8) * mm});
            skLineSegment(sketch, "E5.0.4.76", {"start": v(-3, 3.2) * mm, "end": v(-2.5, 3.2) * mm});
            skLineSegment(sketch, "E5.0.4.77", {"start": v(-3.5, 3.6) * mm, "end": v(-3.5, 3.8) * mm});
            skLineSegment(sketch, "E5.0.4.78", {"start": v(-5, 3.6) * mm, "end": v(-5, 3.8) * mm});
            skLineSegment(sketch, "E5.0.4.79", {"start": v(-6, 3.4) * mm, "end": v(-5.5, 3.4) * mm});
            skLineSegment(sketch, "E5.0.4.80", {"start": v(-6.5, 3.6) * mm, "end": v(-6.5, 3.8) * mm});
            skLineSegment(sketch, "E5.0.4.81", {"start": v(-2, 3.6) * mm, "end": v(-2, 3.8) * mm});
            skLineSegment(sketch, "E5.0.4.82", {"start": v(-15, 3.6) * mm, "end": v(-15, 3.8) * mm});
            skLineSegment(sketch, "E5.0.4.83", {"start": v(-7.5, 3.2) * mm, "end": v(-7.5, 3.4) * mm});
            skLineSegment(sketch, "E5.0.4.84", {"start": v(-10.5, 3.6) * mm, "end": v(-10.5, 3.8) * mm});
            skLineSegment(sketch, "E5.0.4.85", {"start": v(-11.5, 3.6) * mm, "end": v(-11, 3.6) * mm});
            skLineSegment(sketch, "E5.0.4.86", {"start": v(-1.5, 3.6) * mm, "end": v(-1, 3.6) * mm});
            skLineSegment(sketch, "E5.0.4.87", {"start": v(-17.5, 3.2) * mm, "end": v(-17.5, 3.4) * mm});
            skLineSegment(sketch, "E5.0.4.88", {"start": v(-7.5, 3.6) * mm, "end": v(-7.5, 3.8) * mm});
            skLineSegment(sketch, "E5.0.4.89", {"start": v(-17.5, 3.6) * mm, "end": v(-17, 3.6) * mm});
            skLineSegment(sketch, "E5.0.4.90", {"start": v(-3.5, 3.2) * mm, "end": v(-3.5, 3.4) * mm});
            skLineSegment(sketch, "E5.0.4.91", {"start": v(-13.5, 3.6) * mm, "end": v(-13.5, 3.8) * mm});
            skLineSegment(sketch, "E5.0.4.92", {"start": v(-4, 3.4) * mm, "end": v(-3.5, 3.4) * mm});
            skLineSegment(sketch, "E5.0.4.93", {"start": v(-4.5, 3.2) * mm, "end": v(-4.5, 3.4) * mm});
            skLineSegment(sketch, "E5.0.4.94", {"start": v(-11.5, 3.2) * mm, "end": v(-11.5, 3.4) * mm});
            skLineSegment(sketch, "E5.0.4.95", {"start": v(-17.5, 3.6) * mm, "end": v(-17.5, 3.8) * mm});
            skLineSegment(sketch, "E5.0.4.96", {"start": v(-16, 3.2) * mm, "end": v(-16, 3.4) * mm});
            skLineSegment(sketch, "E5.0.4.97", {"start": v(-3.5, 3.6) * mm, "end": v(-3, 3.6) * mm});
            skLineSegment(sketch, "E5.0.4.98", {"start": v(-1.5, 3.2) * mm, "end": v(-1.5, 3.4) * mm});
            skLineSegment(sketch, "E5.0.4.99", {"start": v(-18, 3.2) * mm, "end": v(-18, 3.4) * mm});
            skLineSegment(sketch, "E5.0.4.100", {"start": v(-10, 3.2) * mm, "end": v(-10, 3.4) * mm});
            skLineSegment(sketch, "E5.0.4.101", {"start": v(-4.5, 3.6) * mm, "end": v(-4, 3.6) * mm});
            skLineSegment(sketch, "E5.0.4.102", {"start": v(-19, 3.2) * mm, "end": v(-19, 3.4) * mm});
            skLineSegment(sketch, "E5.0.4.103", {"start": v(-14, 3.4) * mm, "end": v(-13.5, 3.4) * mm});
            skLineSegment(sketch, "E5.0.4.104", {"start": v(-12.5, 3.2) * mm, "end": v(-12.5, 3.4) * mm});
            skLineSegment(sketch, "E5.0.4.105", {"start": v(-12.5, 3.6) * mm, "end": v(-12.5, 3.8) * mm});
            skLineSegment(sketch, "E5.0.4.106", {"start": v(-2, 3.4) * mm, "end": v(-1.5, 3.4) * mm});
            skLineSegment(sketch, "E5.0.4.107", {"start": v(-12, 3.4) * mm, "end": v(-11.5, 3.4) * mm});
            skLineSegment(sketch, "E5.0.4.108", {"start": v(-8.5, 3.2) * mm, "end": v(-8.5, 3.4) * mm});
            skLineSegment(sketch, "E5.0.4.109", {"start": v(-0.5, 3.2) * mm, "end": v(-0.5, 3.4) * mm});
            skLineSegment(sketch, "E5.0.4.110", {"start": v(-9.5, 3.6) * mm, "end": v(-9, 3.6) * mm});
            skLineSegment(sketch, "E5.0.4.111", {"start": v(-17, 3.6) * mm, "end": v(-17, 3.8) * mm});
            skLineSegment(sketch, "E5.0.4.112", {"start": v(-13.5, 3.6) * mm, "end": v(-13, 3.6) * mm});
            skLineSegment(sketch, "E5.0.4.113", {"start": v(-4, 3.2) * mm, "end": v(-4, 3.4) * mm});
            skLineSegment(sketch, "E5.0.4.114", {"start": v(-9.5, 3.6) * mm, "end": v(-9.5, 3.8) * mm});
            skLineSegment(sketch, "E5.0.4.115", {"start": v(-1.5, 3.6) * mm, "end": v(-1.5, 3.8) * mm});
            skLineSegment(sketch, "E5.0.4.116", {"start": v(-8, 3.4) * mm, "end": v(-7.5, 3.4) * mm});
            skLineSegment(sketch, "E5.0.4.117", {"start": v(-18, 3.4) * mm, "end": v(-17.5, 3.4) * mm});
            skLineSegment(sketch, "E5.0.4.118", {"start": v(-7.5, 3.6) * mm, "end": v(-7, 3.6) * mm});
            skLineSegment(sketch, "E5.0.4.119", {"start": v(-13.5, 3.2) * mm, "end": v(-13.5, 3.4) * mm});
            skLineSegment(sketch, "E5.0.4.120", {"start": v(-5.5, 3.2) * mm, "end": v(-5.5, 3.4) * mm});
            skLineSegment(sketch, "E5.0.4.121", {"start": v(-0.5, 3.6) * mm, "end": v(-0.5, 3.8) * mm});
            skLineSegment(sketch, "E5.0.4.122", {"start": v(-8.5, 3.6) * mm, "end": v(-8.5, 3.8) * mm});
            skLineSegment(sketch, "E5.0.4.123", {"start": v(-4.5, 3.6) * mm, "end": v(-4.5, 3.8) * mm});
            skLineSegment(sketch, "E5.0.4.124", {"start": v(-8, 3.2) * mm, "end": v(-8, 3.4) * mm});
            skLineSegment(sketch, "E5.0.4.125", {"start": v(-2.5, 3.6) * mm, "end": v(-2.5, 3.8) * mm});
            skLineSegment(sketch, "E5.0.4.126", {"start": v(-9, 3.6) * mm, "end": v(-9, 3.8) * mm});
            skLineSegment(sketch, "E5.0.4.127", {"start": v(-5.5, 3.6) * mm, "end": v(-5, 3.6) * mm});
            skLineSegment(sketch, "E5.0.4.128", {"start": v(-13, 3.6) * mm, "end": v(-13, 3.8) * mm});
            skLineSegment(sketch, "E5.0.4.129", {"start": v(-1, 3.6) * mm, "end": v(-1, 3.8) * mm});
            skLineSegment(sketch, "E5.0.4.130", {"start": v(-14, 3.2) * mm, "end": v(-14, 3.4) * mm});
            skLineSegment(sketch, "E5.0.4.131", {"start": v(-6.5, 3.2) * mm, "end": v(-6.5, 3.4) * mm});
            skLineSegment(sketch, "E5.0.4.132", {"start": v(-10.5, 3.2) * mm, "end": v(-10.5, 3.4) * mm});
            skLineSegment(sketch, "E5.0.4.133", {"start": v(-18.5, 3.6) * mm, "end": v(-18.5, 3.8) * mm});
            skLineSegment(sketch, "E5.0.4.134", {"start": v(-14.5, 3.2) * mm, "end": v(-14.5, 3.4) * mm});
            skLineSegment(sketch, "E5.0.4.135", {"start": v(-4, 3.6) * mm, "end": v(-4, 3.8) * mm});
            skLineSegment(sketch, "E5.0.4.136", {"start": v(-6, 3.2) * mm, "end": v(-6, 3.4) * mm});
            skLineSegment(sketch, "E5.0.4.137", {"start": v(-16.5, 3.2) * mm, "end": v(-16.5, 3.4) * mm});
            skLineSegment(sketch, "E5.0.4.138", {"start": v(-17, 3.4) * mm, "end": v(-16.5, 3.4) * mm});
            skLineSegment(sketch, "E5.0.4.139", {"start": v(-19, 3.6) * mm, "end": v(-19, 3.8) * mm});
            skLineSegment(sketch, "E5.0.4.140", {"start": v(-10, 3.4) * mm, "end": v(-9.5, 3.4) * mm});
            skLineSegment(sketch, "E5.0.4.141", {"start": v(-5.5, 3.6) * mm, "end": v(-5.5, 3.8) * mm});
            skLineSegment(sketch, "E5.0.4.142", {"start": v(-15.5, 3.6) * mm, "end": v(-15.5, 3.8) * mm});
            skLineSegment(sketch, "E5.0.4.143", {"start": v(-9.5, 3.2) * mm, "end": v(-9.5, 3.4) * mm});
            skLineSegment(sketch, "E5.0.4.144", {"start": v(-20, 3.2) * mm, "end": v(-19.5, 3.2) * mm});
            skLineSegment(sketch, "E5.0.4.145", {"start": v(-3, 3.6) * mm, "end": v(-3, 3.8) * mm});
            skLineSegment(sketch, "E5.0.4.146", {"start": v(-12, 3.2) * mm, "end": v(-12, 3.4) * mm});
            skLineSegment(sketch, "E5.0.4.147", {"start": v(-2, 3.2) * mm, "end": v(-2, 3.4) * mm});
            skLineSegment(sketch, "E5.0.4.148", {"start": v(-16, 3.4) * mm, "end": v(-15.5, 3.4) * mm});
            skLineSegment(sketch, "E5.0.4.149", {"start": v(-11, 3.6) * mm, "end": v(-11, 3.8) * mm});
            skLineSegment(sketch, "E5.0.4.150", {"start": v(-2.5, 3.2) * mm, "end": v(-2.5, 3.4) * mm});
            skLineSegment(sketch, "E5.0.4.151", {"start": v(-14.5, 3.6) * mm, "end": v(-14.5, 3.8) * mm});
            skLineSegment(sketch, "E5.0.4.152", {"start": v(-15.5, 3.6) * mm, "end": v(-15, 3.6) * mm});
            skLineSegment(sketch, "E5.0.4.153", {"start": v(-11.5, 3.6) * mm, "end": v(-11.5, 3.8) * mm});
            skLineSegment(sketch, "E5.0.4.154", {"start": v(-7, 3.6) * mm, "end": v(-7, 3.8) * mm});
            skLineSegment(sketch, "E5.0.4.155", {"start": v(-15.5, 3.2) * mm, "end": v(-15.5, 3.4) * mm});
            skLineSegment(sketch, "E5.0.4.156", {"start": v(-2.5, 3.6) * mm, "end": v(-2, 3.6) * mm});
            skLineSegment(sketch, "E5.0.4.157", {"start": v(-16.5, 3.6) * mm, "end": v(-16.5, 3.8) * mm});
            skLineSegment(sketch, "E5.0.4.158", {"start": v(-19.5, 3.6) * mm, "end": v(-19.5, 3.8) * mm});
            skLineSegment(sketch, "E5.0.4.159", {"start": v(-19.5, 3.6) * mm, "end": v(-19, 3.6) * mm});
            skLineSegment(sketch, "E5.0.5.0", {"start": v(-5, 4.2) * mm, "end": v(-4.5, 4.2) * mm});
            skLineSegment(sketch, "E5.0.5.1", {"start": v(-13.5, 4.6) * mm, "end": v(-13, 4.6) * mm});
            skLineSegment(sketch, "E5.0.5.2", {"start": v(-17, 4) * mm, "end": v(-16.5, 4) * mm});
            skLineSegment(sketch, "E5.0.5.3", {"start": v(-19.5, 4.6) * mm, "end": v(-19, 4.6) * mm});
            skLineSegment(sketch, "E5.0.5.4", {"start": v(-16.5, 4.6) * mm, "end": v(-16, 4.6) * mm});
            skLineSegment(sketch, "E5.0.5.5", {"start": v(-14.5, 4.6) * mm, "end": v(-14, 4.6) * mm});
            skLineSegment(sketch, "E5.0.5.6", {"start": v(-19, 4) * mm, "end": v(-18.5, 4) * mm});
            skLineSegment(sketch, "E5.0.5.7", {"start": v(-15, 4) * mm, "end": v(-14.5, 4) * mm});
            skLineSegment(sketch, "E5.0.5.8", {"start": v(-4.5, 4.6) * mm, "end": v(-4, 4.6) * mm});
            skLineSegment(sketch, "E5.0.5.9", {"start": v(-7.5, 4.6) * mm, "end": v(-7, 4.6) * mm});
            skLineSegment(sketch, "E5.0.5.10", {"start": v(-12.5, 4.6) * mm, "end": v(-12, 4.6) * mm});
            skLineSegment(sketch, "E5.0.5.11", {"start": v(-0.5, 4.4) * mm, "end": v(0, 4.4) * mm});
            skLineSegment(sketch, "E5.0.5.12", {"start": v(-1.5, 4.6) * mm, "end": v(-1, 4.6) * mm});
            skLineSegment(sketch, "E5.0.5.13", {"start": v(-16, 4) * mm, "end": v(-15.5, 4) * mm});
            skLineSegment(sketch, "E5.0.5.14", {"start": v(-12, 4) * mm, "end": v(-11.5, 4) * mm});
            skLineSegment(sketch, "E5.0.5.15", {"start": v(-18.5, 4.6) * mm, "end": v(-18, 4.6) * mm});
            skLineSegment(sketch, "E5.0.5.16", {"start": v(-18.5, 4.4) * mm, "end": v(-18, 4.4) * mm});
            skLineSegment(sketch, "E5.0.5.17", {"start": v(-0.5, 4.6) * mm, "end": v(0, 4.6) * mm});
            skLineSegment(sketch, "E5.0.5.18", {"start": v(-13, 4) * mm, "end": v(-13, 4.2) * mm});
            skLineSegment(sketch, "E5.0.5.19", {"start": v(-10, 4.4) * mm, "end": v(-10, 4.6) * mm});
            skLineSegment(sketch, "E5.0.5.20", {"start": v(-1, 4.2) * mm, "end": v(-0.5, 4.2) * mm});
            skLineSegment(sketch, "E5.0.5.21", {"start": v(-11, 4) * mm, "end": v(-11, 4.2) * mm});
            skLineSegment(sketch, "E5.0.5.22", {"start": v(-18.5, 4) * mm, "end": v(-18.5, 4.2) * mm});
            skLineSegment(sketch, "E5.0.5.23", {"start": v(-7, 4.2) * mm, "end": v(-6.5, 4.2) * mm});
            skLineSegment(sketch, "E5.0.5.24", {"start": v(-17.5, 4.6) * mm, "end": v(-17, 4.6) * mm});
            skLineSegment(sketch, "E5.0.5.25", {"start": v(-13, 4.2) * mm, "end": v(-12.5, 4.2) * mm});
            skLineSegment(sketch, "E5.0.5.26", {"start": v(-20, 4.2) * mm, "end": v(-19.5, 4.2) * mm});
            skLineSegment(sketch, "E5.0.5.27", {"start": v(-16.5, 4.4) * mm, "end": v(-16, 4.4) * mm});
            skLineSegment(sketch, "E5.0.5.28", {"start": v(-8.5, 4.6) * mm, "end": v(-8, 4.6) * mm});
            skLineSegment(sketch, "E5.0.5.29", {"start": v(-15, 4) * mm, "end": v(-15, 4.2) * mm});
            skLineSegment(sketch, "E5.0.5.30", {"start": v(-8.5, 4.4) * mm, "end": v(-8, 4.4) * mm});
            skLineSegment(sketch, "E5.0.5.31", {"start": v(-9.5, 4.6) * mm, "end": v(-9, 4.6) * mm});
            skLineSegment(sketch, "E5.0.5.32", {"start": v(-6.5, 4.4) * mm, "end": v(-6, 4.4) * mm});
            skLineSegment(sketch, "E5.0.5.33", {"start": v(-8, 4.4) * mm, "end": v(-8, 4.6) * mm});
            skLineSegment(sketch, "E5.0.5.34", {"start": v(-16, 4.4) * mm, "end": v(-16, 4.6) * mm});
            skLineSegment(sketch, "E5.0.5.35", {"start": v(-11.5, 4.6) * mm, "end": v(-11, 4.6) * mm});
            skLineSegment(sketch, "E5.0.5.36", {"start": v(-12.5, 4.4) * mm, "end": v(-12, 4.4) * mm});
            skLineSegment(sketch, "E5.0.5.37", {"start": v(-10, 4) * mm, "end": v(-9.5, 4) * mm});
            skLineSegment(sketch, "E5.0.5.38", {"start": v(-8, 4) * mm, "end": v(-7.5, 4) * mm});
            skLineSegment(sketch, "E5.0.5.39", {"start": v(-6, 4) * mm, "end": v(-5.5, 4) * mm});
            skLineSegment(sketch, "E5.0.5.40", {"start": v(-2, 4) * mm, "end": v(-1.5, 4) * mm});
            skLineSegment(sketch, "E5.0.5.41", {"start": v(-3.5, 4.6) * mm, "end": v(-3, 4.6) * mm});
            skLineSegment(sketch, "E5.0.5.42", {"start": v(-1, 4) * mm, "end": v(-1, 4.2) * mm});
            skLineSegment(sketch, "E5.0.5.43", {"start": v(-4, 4) * mm, "end": v(-3.5, 4) * mm});
            skLineSegment(sketch, "E5.0.5.44", {"start": v(-5, 4) * mm, "end": v(-5, 4.2) * mm});
            skLineSegment(sketch, "E5.0.5.45", {"start": v(-9, 4) * mm, "end": v(-9, 4.2) * mm});
            skLineSegment(sketch, "E5.0.5.46", {"start": v(-15.5, 4.6) * mm, "end": v(-15, 4.6) * mm});
            skLineSegment(sketch, "E5.0.5.47", {"start": v(-20, 4) * mm, "end": v(-20, 4.2) * mm});
            skLineSegment(sketch, "E5.0.5.48", {"start": v(-18, 4) * mm, "end": v(-17.5, 4) * mm});
            skLineSegment(sketch, "E5.0.5.49", {"start": v(-17, 4) * mm, "end": v(-17, 4.2) * mm});
            skLineSegment(sketch, "E5.0.5.50", {"start": v(-19, 4.2) * mm, "end": v(-18.5, 4.2) * mm});
            skLineSegment(sketch, "E5.0.5.51", {"start": v(-7, 4) * mm, "end": v(-7, 4.2) * mm});
            skLineSegment(sketch, "E5.0.5.52", {"start": v(-19.5, 4) * mm, "end": v(-19.5, 4.2) * mm});
            skLineSegment(sketch, "E5.0.5.53", {"start": v(-6, 4.4) * mm, "end": v(-6, 4.6) * mm});
            skLineSegment(sketch, "E5.0.5.54", {"start": v(-14, 4.4) * mm, "end": v(-14, 4.6) * mm});
            skLineSegment(sketch, "E5.0.5.55", {"start": v(-18, 4.4) * mm, "end": v(-18, 4.6) * mm});
            skLineSegment(sketch, "E5.0.5.56", {"start": v(-1, 4) * mm, "end": v(-0.5, 4) * mm});
            skLineSegment(sketch, "E5.0.5.57", {"start": v(-9, 4) * mm, "end": v(-8.5, 4) * mm});
            skLineSegment(sketch, "E5.0.5.58", {"start": v(-11, 4.2) * mm, "end": v(-10.5, 4.2) * mm});
            skLineSegment(sketch, "E5.0.5.59", {"start": v(-2.5, 4.6) * mm, "end": v(-2, 4.6) * mm});
            skLineSegment(sketch, "E5.0.5.60", {"start": v(-9, 4.2) * mm, "end": v(-8.5, 4.2) * mm});
            skLineSegment(sketch, "E5.0.5.61", {"start": v(-11, 4) * mm, "end": v(-10.5, 4) * mm});
            skLineSegment(sketch, "E5.0.5.62", {"start": v(-3, 4) * mm, "end": v(-3, 4.2) * mm});
            skLineSegment(sketch, "E5.0.5.63", {"start": v(0, 4.4) * mm, "end": v(0, 4.6) * mm});
            skLineSegment(sketch, "E5.0.5.64", {"start": v(-10.5, 4.6) * mm, "end": v(-10, 4.6) * mm});
            skLineSegment(sketch, "E5.0.5.65", {"start": v(-14.5, 4.4) * mm, "end": v(-14, 4.4) * mm});
            skLineSegment(sketch, "E5.0.5.66", {"start": v(-10.5, 4.4) * mm, "end": v(-10, 4.4) * mm});
            skLineSegment(sketch, "E5.0.5.67", {"start": v(-5, 4) * mm, "end": v(-4.5, 4) * mm});
            skLineSegment(sketch, "E5.0.5.68", {"start": v(-3, 4.2) * mm, "end": v(-2.5, 4.2) * mm});
            skLineSegment(sketch, "E5.0.5.69", {"start": v(-14, 4) * mm, "end": v(-13.5, 4) * mm});
            skLineSegment(sketch, "E5.0.5.70", {"start": v(-6.5, 4.6) * mm, "end": v(-6, 4.6) * mm});
            skLineSegment(sketch, "E5.0.5.71", {"start": v(-13, 4) * mm, "end": v(-12.5, 4) * mm});
            skLineSegment(sketch, "E5.0.5.72", {"start": v(-15, 4.2) * mm, "end": v(-14.5, 4.2) * mm});
            skLineSegment(sketch, "E5.0.5.73", {"start": v(-12, 4.4) * mm, "end": v(-12, 4.6) * mm});
            skLineSegment(sketch, "E5.0.5.74", {"start": v(-7, 4) * mm, "end": v(-6.5, 4) * mm});
            skLineSegment(sketch, "E5.0.5.75", {"start": v(-5.5, 4.6) * mm, "end": v(-5, 4.6) * mm});
            skLineSegment(sketch, "E5.0.5.76", {"start": v(-3, 4) * mm, "end": v(-2.5, 4) * mm});
            skLineSegment(sketch, "E5.0.5.77", {"start": v(-3.5, 4.4) * mm, "end": v(-3.5, 4.6) * mm});
            skLineSegment(sketch, "E5.0.5.78", {"start": v(-5, 4.4) * mm, "end": v(-5, 4.6) * mm});
            skLineSegment(sketch, "E5.0.5.79", {"start": v(-6, 4.2) * mm, "end": v(-5.5, 4.2) * mm});
            skLineSegment(sketch, "E5.0.5.80", {"start": v(-6.5, 4.4) * mm, "end": v(-6.5, 4.6) * mm});
            skLineSegment(sketch, "E5.0.5.81", {"start": v(-2, 4.4) * mm, "end": v(-2, 4.6) * mm});
            skLineSegment(sketch, "E5.0.5.82", {"start": v(-15, 4.4) * mm, "end": v(-15, 4.6) * mm});
            skLineSegment(sketch, "E5.0.5.83", {"start": v(-7.5, 4) * mm, "end": v(-7.5, 4.2) * mm});
            skLineSegment(sketch, "E5.0.5.84", {"start": v(-10.5, 4.4) * mm, "end": v(-10.5, 4.6) * mm});
            skLineSegment(sketch, "E5.0.5.85", {"start": v(-11.5, 4.4) * mm, "end": v(-11, 4.4) * mm});
            skLineSegment(sketch, "E5.0.5.86", {"start": v(-1.5, 4.4) * mm, "end": v(-1, 4.4) * mm});
            skLineSegment(sketch, "E5.0.5.87", {"start": v(-17.5, 4) * mm, "end": v(-17.5, 4.2) * mm});
            skLineSegment(sketch, "E5.0.5.88", {"start": v(-7.5, 4.4) * mm, "end": v(-7.5, 4.6) * mm});
            skLineSegment(sketch, "E5.0.5.89", {"start": v(-17.5, 4.4) * mm, "end": v(-17, 4.4) * mm});
            skLineSegment(sketch, "E5.0.5.90", {"start": v(-3.5, 4) * mm, "end": v(-3.5, 4.2) * mm});
            skLineSegment(sketch, "E5.0.5.91", {"start": v(-13.5, 4.4) * mm, "end": v(-13.5, 4.6) * mm});
            skLineSegment(sketch, "E5.0.5.92", {"start": v(-4, 4.2) * mm, "end": v(-3.5, 4.2) * mm});
            skLineSegment(sketch, "E5.0.5.93", {"start": v(-4.5, 4) * mm, "end": v(-4.5, 4.2) * mm});
            skLineSegment(sketch, "E5.0.5.94", {"start": v(-11.5, 4) * mm, "end": v(-11.5, 4.2) * mm});
            skLineSegment(sketch, "E5.0.5.95", {"start": v(-17.5, 4.4) * mm, "end": v(-17.5, 4.6) * mm});
            skLineSegment(sketch, "E5.0.5.96", {"start": v(-16, 4) * mm, "end": v(-16, 4.2) * mm});
            skLineSegment(sketch, "E5.0.5.97", {"start": v(-3.5, 4.4) * mm, "end": v(-3, 4.4) * mm});
            skLineSegment(sketch, "E5.0.5.98", {"start": v(-1.5, 4) * mm, "end": v(-1.5, 4.2) * mm});
            skLineSegment(sketch, "E5.0.5.99", {"start": v(-18, 4) * mm, "end": v(-18, 4.2) * mm});
            skLineSegment(sketch, "E5.0.5.100", {"start": v(-10, 4) * mm, "end": v(-10, 4.2) * mm});
            skLineSegment(sketch, "E5.0.5.101", {"start": v(-4.5, 4.4) * mm, "end": v(-4, 4.4) * mm});
            skLineSegment(sketch, "E5.0.5.102", {"start": v(-19, 4) * mm, "end": v(-19, 4.2) * mm});
            skLineSegment(sketch, "E5.0.5.103", {"start": v(-14, 4.2) * mm, "end": v(-13.5, 4.2) * mm});
            skLineSegment(sketch, "E5.0.5.104", {"start": v(-12.5, 4) * mm, "end": v(-12.5, 4.2) * mm});
            skLineSegment(sketch, "E5.0.5.105", {"start": v(-12.5, 4.4) * mm, "end": v(-12.5, 4.6) * mm});
            skLineSegment(sketch, "E5.0.5.106", {"start": v(-2, 4.2) * mm, "end": v(-1.5, 4.2) * mm});
            skLineSegment(sketch, "E5.0.5.107", {"start": v(-12, 4.2) * mm, "end": v(-11.5, 4.2) * mm});
            skLineSegment(sketch, "E5.0.5.108", {"start": v(-8.5, 4) * mm, "end": v(-8.5, 4.2) * mm});
            skLineSegment(sketch, "E5.0.5.109", {"start": v(-0.5, 4) * mm, "end": v(-0.5, 4.2) * mm});
            skLineSegment(sketch, "E5.0.5.110", {"start": v(-9.5, 4.4) * mm, "end": v(-9, 4.4) * mm});
            skLineSegment(sketch, "E5.0.5.111", {"start": v(-17, 4.4) * mm, "end": v(-17, 4.6) * mm});
            skLineSegment(sketch, "E5.0.5.112", {"start": v(-13.5, 4.4) * mm, "end": v(-13, 4.4) * mm});
            skLineSegment(sketch, "E5.0.5.113", {"start": v(-4, 4) * mm, "end": v(-4, 4.2) * mm});
            skLineSegment(sketch, "E5.0.5.114", {"start": v(-9.5, 4.4) * mm, "end": v(-9.5, 4.6) * mm});
            skLineSegment(sketch, "E5.0.5.115", {"start": v(-1.5, 4.4) * mm, "end": v(-1.5, 4.6) * mm});
            skLineSegment(sketch, "E5.0.5.116", {"start": v(-8, 4.2) * mm, "end": v(-7.5, 4.2) * mm});
            skLineSegment(sketch, "E5.0.5.117", {"start": v(-18, 4.2) * mm, "end": v(-17.5, 4.2) * mm});
            skLineSegment(sketch, "E5.0.5.118", {"start": v(-7.5, 4.4) * mm, "end": v(-7, 4.4) * mm});
            skLineSegment(sketch, "E5.0.5.119", {"start": v(-13.5, 4) * mm, "end": v(-13.5, 4.2) * mm});
            skLineSegment(sketch, "E5.0.5.120", {"start": v(-5.5, 4) * mm, "end": v(-5.5, 4.2) * mm});
            skLineSegment(sketch, "E5.0.5.121", {"start": v(-0.5, 4.4) * mm, "end": v(-0.5, 4.6) * mm});
            skLineSegment(sketch, "E5.0.5.122", {"start": v(-8.5, 4.4) * mm, "end": v(-8.5, 4.6) * mm});
            skLineSegment(sketch, "E5.0.5.123", {"start": v(-4.5, 4.4) * mm, "end": v(-4.5, 4.6) * mm});
            skLineSegment(sketch, "E5.0.5.124", {"start": v(-8, 4) * mm, "end": v(-8, 4.2) * mm});
            skLineSegment(sketch, "E5.0.5.125", {"start": v(-2.5, 4.4) * mm, "end": v(-2.5, 4.6) * mm});
            skLineSegment(sketch, "E5.0.5.126", {"start": v(-9, 4.4) * mm, "end": v(-9, 4.6) * mm});
            skLineSegment(sketch, "E5.0.5.127", {"start": v(-5.5, 4.4) * mm, "end": v(-5, 4.4) * mm});
            skLineSegment(sketch, "E5.0.5.128", {"start": v(-13, 4.4) * mm, "end": v(-13, 4.6) * mm});
            skLineSegment(sketch, "E5.0.5.129", {"start": v(-1, 4.4) * mm, "end": v(-1, 4.6) * mm});
            skLineSegment(sketch, "E5.0.5.130", {"start": v(-14, 4) * mm, "end": v(-14, 4.2) * mm});
            skLineSegment(sketch, "E5.0.5.131", {"start": v(-6.5, 4) * mm, "end": v(-6.5, 4.2) * mm});
            skLineSegment(sketch, "E5.0.5.132", {"start": v(-10.5, 4) * mm, "end": v(-10.5, 4.2) * mm});
            skLineSegment(sketch, "E5.0.5.133", {"start": v(-18.5, 4.4) * mm, "end": v(-18.5, 4.6) * mm});
            skLineSegment(sketch, "E5.0.5.134", {"start": v(-14.5, 4) * mm, "end": v(-14.5, 4.2) * mm});
            skLineSegment(sketch, "E5.0.5.135", {"start": v(-4, 4.4) * mm, "end": v(-4, 4.6) * mm});
            skLineSegment(sketch, "E5.0.5.136", {"start": v(-6, 4) * mm, "end": v(-6, 4.2) * mm});
            skLineSegment(sketch, "E5.0.5.137", {"start": v(-16.5, 4) * mm, "end": v(-16.5, 4.2) * mm});
            skLineSegment(sketch, "E5.0.5.138", {"start": v(-17, 4.2) * mm, "end": v(-16.5, 4.2) * mm});
            skLineSegment(sketch, "E5.0.5.139", {"start": v(-19, 4.4) * mm, "end": v(-19, 4.6) * mm});
            skLineSegment(sketch, "E5.0.5.140", {"start": v(-10, 4.2) * mm, "end": v(-9.5, 4.2) * mm});
            skLineSegment(sketch, "E5.0.5.141", {"start": v(-5.5, 4.4) * mm, "end": v(-5.5, 4.6) * mm});
            skLineSegment(sketch, "E5.0.5.142", {"start": v(-15.5, 4.4) * mm, "end": v(-15.5, 4.6) * mm});
            skLineSegment(sketch, "E5.0.5.143", {"start": v(-9.5, 4) * mm, "end": v(-9.5, 4.2) * mm});
            skLineSegment(sketch, "E5.0.5.144", {"start": v(-20, 4) * mm, "end": v(-19.5, 4) * mm});
            skLineSegment(sketch, "E5.0.5.145", {"start": v(-3, 4.4) * mm, "end": v(-3, 4.6) * mm});
            skLineSegment(sketch, "E5.0.5.146", {"start": v(-12, 4) * mm, "end": v(-12, 4.2) * mm});
            skLineSegment(sketch, "E5.0.5.147", {"start": v(-2, 4) * mm, "end": v(-2, 4.2) * mm});
            skLineSegment(sketch, "E5.0.5.148", {"start": v(-16, 4.2) * mm, "end": v(-15.5, 4.2) * mm});
            skLineSegment(sketch, "E5.0.5.149", {"start": v(-11, 4.4) * mm, "end": v(-11, 4.6) * mm});
            skLineSegment(sketch, "E5.0.5.150", {"start": v(-2.5, 4) * mm, "end": v(-2.5, 4.2) * mm});
            skLineSegment(sketch, "E5.0.5.151", {"start": v(-14.5, 4.4) * mm, "end": v(-14.5, 4.6) * mm});
            skLineSegment(sketch, "E5.0.5.152", {"start": v(-15.5, 4.4) * mm, "end": v(-15, 4.4) * mm});
            skLineSegment(sketch, "E5.0.5.153", {"start": v(-11.5, 4.4) * mm, "end": v(-11.5, 4.6) * mm});
            skLineSegment(sketch, "E5.0.5.154", {"start": v(-7, 4.4) * mm, "end": v(-7, 4.6) * mm});
            skLineSegment(sketch, "E5.0.5.155", {"start": v(-15.5, 4) * mm, "end": v(-15.5, 4.2) * mm});
            skLineSegment(sketch, "E5.0.5.156", {"start": v(-2.5, 4.4) * mm, "end": v(-2, 4.4) * mm});
            skLineSegment(sketch, "E5.0.5.157", {"start": v(-16.5, 4.4) * mm, "end": v(-16.5, 4.6) * mm});
            skLineSegment(sketch, "E5.0.5.158", {"start": v(-19.5, 4.4) * mm, "end": v(-19.5, 4.6) * mm});
            skLineSegment(sketch, "E5.0.5.159", {"start": v(-19.5, 4.4) * mm, "end": v(-19, 4.4) * mm});
            skLineSegment(sketch, "E5.direction1", {"start": v(-20, 0) * mm, "end": v(15.75, 0) * mm, "construction": true});
            skLineSegment(sketch, "E5.direction2", {"start": v(-20, 0) * mm, "end": v(-20, 0.8) * mm, "construction": true});
            skLineSegment(sketch, "E6.0.20.0", {"start": v(0, 0) * mm, "end": v(0, 0.2) * mm});
            skLineSegment(sketch, "E6.3.20.0", {"start": v(0.5, 0) * mm, "end": v(0.5, 0.2) * mm});
            skLineSegment(sketch, "E6.6.20.0", {"start": v(0, 0.2) * mm, "end": v(0.5, 0.2) * mm});
            skLineSegment(sketch, "E6.9.20.0", {"start": v(0, 0) * mm, "end": v(0.5, 0) * mm});
            skLineSegment(sketch, "E6.0.21.0", {"start": v(1, 0) * mm, "end": v(1, 0.2) * mm});
            skLineSegment(sketch, "E6.3.21.0", {"start": v(1.5, 0) * mm, "end": v(1.5, 0.2) * mm});
            skLineSegment(sketch, "E6.6.21.0", {"start": v(1, 0.2) * mm, "end": v(1.5, 0.2) * mm});
            skLineSegment(sketch, "E6.9.21.0", {"start": v(1, 0) * mm, "end": v(1.5, 0) * mm});
            skLineSegment(sketch, "E6.0.22.0", {"start": v(2, 0) * mm, "end": v(2, 0.2) * mm});
            skLineSegment(sketch, "E6.3.22.0", {"start": v(2.5, 0) * mm, "end": v(2.5, 0.2) * mm});
            skLineSegment(sketch, "E6.6.22.0", {"start": v(2, 0.2) * mm, "end": v(2.5, 0.2) * mm});
            skLineSegment(sketch, "E6.9.22.0", {"start": v(2, 0) * mm, "end": v(2.5, 0) * mm});
            skLineSegment(sketch, "E6.0.23.0", {"start": v(3, 0) * mm, "end": v(3, 0.2) * mm});
            skLineSegment(sketch, "E6.3.23.0", {"start": v(3.5, 0) * mm, "end": v(3.5, 0.2) * mm});
            skLineSegment(sketch, "E6.6.23.0", {"start": v(3, 0.2) * mm, "end": v(3.5, 0.2) * mm});
            skLineSegment(sketch, "E6.9.23.0", {"start": v(3, 0) * mm, "end": v(3.5, 0) * mm});
            skLineSegment(sketch, "E6.0.24.0", {"start": v(4, 0) * mm, "end": v(4, 0.2) * mm});
            skLineSegment(sketch, "E6.3.24.0", {"start": v(4.5, 0) * mm, "end": v(4.5, 0.2) * mm});
            skLineSegment(sketch, "E6.6.24.0", {"start": v(4, 0.2) * mm, "end": v(4.5, 0.2) * mm});
            skLineSegment(sketch, "E6.9.24.0", {"start": v(4, 0) * mm, "end": v(4.5, 0) * mm});
            skLineSegment(sketch, "E6.0.25.0", {"start": v(5, 0) * mm, "end": v(5, 0.2) * mm});
            skLineSegment(sketch, "E6.3.25.0", {"start": v(5.5, 0) * mm, "end": v(5.5, 0.2) * mm});
            skLineSegment(sketch, "E6.6.25.0", {"start": v(5, 0.2) * mm, "end": v(5.5, 0.2) * mm});
            skLineSegment(sketch, "E6.9.25.0", {"start": v(5, 0) * mm, "end": v(5.5, 0) * mm});
            skLineSegment(sketch, "E6.0.26.0", {"start": v(6, 0) * mm, "end": v(6, 0.2) * mm});
            skLineSegment(sketch, "E6.3.26.0", {"start": v(6.5, 0) * mm, "end": v(6.5, 0.2) * mm});
            skLineSegment(sketch, "E6.6.26.0", {"start": v(6, 0.2) * mm, "end": v(6.5, 0.2) * mm});
            skLineSegment(sketch, "E6.9.26.0", {"start": v(6, 0) * mm, "end": v(6.5, 0) * mm});
            skLineSegment(sketch, "E6.0.27.0", {"start": v(7, 0) * mm, "end": v(7, 0.2) * mm});
            skLineSegment(sketch, "E6.3.27.0", {"start": v(7.5, 0) * mm, "end": v(7.5, 0.2) * mm});
            skLineSegment(sketch, "E6.6.27.0", {"start": v(7, 0.2) * mm, "end": v(7.5, 0.2) * mm});
            skLineSegment(sketch, "E6.9.27.0", {"start": v(7, 0) * mm, "end": v(7.5, 0) * mm});
            skLineSegment(sketch, "E6.0.28.0", {"start": v(8, 0) * mm, "end": v(8, 0.2) * mm});
            skLineSegment(sketch, "E6.3.28.0", {"start": v(8.5, 0) * mm, "end": v(8.5, 0.2) * mm});
            skLineSegment(sketch, "E6.6.28.0", {"start": v(8, 0.2) * mm, "end": v(8.5, 0.2) * mm});
            skLineSegment(sketch, "E6.9.28.0", {"start": v(8, 0) * mm, "end": v(8.5, 0) * mm});
            skLineSegment(sketch, "E6.0.29.0", {"start": v(9, 0) * mm, "end": v(9, 0.2) * mm});
            skLineSegment(sketch, "E6.3.29.0", {"start": v(9.5, 0) * mm, "end": v(9.5, 0.2) * mm});
            skLineSegment(sketch, "E6.6.29.0", {"start": v(9, 0.2) * mm, "end": v(9.5, 0.2) * mm});
            skLineSegment(sketch, "E6.9.29.0", {"start": v(9, 0) * mm, "end": v(9.5, 0) * mm});
            skLineSegment(sketch, "E6.0.30.0", {"start": v(10, 0) * mm, "end": v(10, 0.2) * mm});
            skLineSegment(sketch, "E6.3.30.0", {"start": v(10.5, 0) * mm, "end": v(10.5, 0.2) * mm});
            skLineSegment(sketch, "E6.6.30.0", {"start": v(10, 0.2) * mm, "end": v(10.5, 0.2) * mm});
            skLineSegment(sketch, "E6.9.30.0", {"start": v(10, 0) * mm, "end": v(10.5, 0) * mm});
            skLineSegment(sketch, "E6.0.31.0", {"start": v(11, 0) * mm, "end": v(11, 0.2) * mm});
            skLineSegment(sketch, "E6.3.31.0", {"start": v(11.5, 0) * mm, "end": v(11.5, 0.2) * mm});
            skLineSegment(sketch, "E6.6.31.0", {"start": v(11, 0.2) * mm, "end": v(11.5, 0.2) * mm});
            skLineSegment(sketch, "E6.9.31.0", {"start": v(11, 0) * mm, "end": v(11.5, 0) * mm});
            skLineSegment(sketch, "E6.0.32.0", {"start": v(12, 0) * mm, "end": v(12, 0.2) * mm});
            skLineSegment(sketch, "E6.3.32.0", {"start": v(12.5, 0) * mm, "end": v(12.5, 0.2) * mm});
            skLineSegment(sketch, "E6.6.32.0", {"start": v(12, 0.2) * mm, "end": v(12.5, 0.2) * mm});
            skLineSegment(sketch, "E6.9.32.0", {"start": v(12, 0) * mm, "end": v(12.5, 0) * mm});
            skLineSegment(sketch, "E6.0.33.0", {"start": v(13, 0) * mm, "end": v(13, 0.2) * mm});
            skLineSegment(sketch, "E6.3.33.0", {"start": v(13.5, 0) * mm, "end": v(13.5, 0.2) * mm});
            skLineSegment(sketch, "E6.6.33.0", {"start": v(13, 0.2) * mm, "end": v(13.5, 0.2) * mm});
            skLineSegment(sketch, "E6.9.33.0", {"start": v(13, 0) * mm, "end": v(13.5, 0) * mm});
            skLineSegment(sketch, "E6.0.34.0", {"start": v(14, 0) * mm, "end": v(14, 0.2) * mm});
            skLineSegment(sketch, "E6.3.34.0", {"start": v(14.5, 0) * mm, "end": v(14.5, 0.2) * mm});
            skLineSegment(sketch, "E6.6.34.0", {"start": v(14, 0.2) * mm, "end": v(14.5, 0.2) * mm});
            skLineSegment(sketch, "E6.9.34.0", {"start": v(14, 0) * mm, "end": v(14.5, 0) * mm});
            skLineSegment(sketch, "E6.0.35.0", {"start": v(15, 0) * mm, "end": v(15, 0.2) * mm});
            skLineSegment(sketch, "E6.3.35.0", {"start": v(15.5, 0) * mm, "end": v(15.5, 0.2) * mm});
            skLineSegment(sketch, "E6.6.35.0", {"start": v(15, 0.2) * mm, "end": v(15.5, 0.2) * mm});
            skLineSegment(sketch, "E6.9.35.0", {"start": v(15, 0) * mm, "end": v(15.5, 0) * mm});
            skLineSegment(sketch, "E6.0.36.0", {"start": v(16, 0) * mm, "end": v(16, 0.2) * mm});
            skLineSegment(sketch, "E6.3.36.0", {"start": v(16.5, 0) * mm, "end": v(16.5, 0.2) * mm});
            skLineSegment(sketch, "E6.6.36.0", {"start": v(16, 0.2) * mm, "end": v(16.5, 0.2) * mm});
            skLineSegment(sketch, "E6.9.36.0", {"start": v(16, 0) * mm, "end": v(16.5, 0) * mm});
            skLineSegment(sketch, "E6.0.37.0", {"start": v(17, 0) * mm, "end": v(17, 0.2) * mm});
            skLineSegment(sketch, "E6.3.37.0", {"start": v(17.5, 0) * mm, "end": v(17.5, 0.2) * mm});
            skLineSegment(sketch, "E6.6.37.0", {"start": v(17, 0.2) * mm, "end": v(17.5, 0.2) * mm});
            skLineSegment(sketch, "E6.9.37.0", {"start": v(17, 0) * mm, "end": v(17.5, 0) * mm});
            skLineSegment(sketch, "E6.0.38.0", {"start": v(18, 0) * mm, "end": v(18, 0.2) * mm});
            skLineSegment(sketch, "E6.3.38.0", {"start": v(18.5, 0) * mm, "end": v(18.5, 0.2) * mm});
            skLineSegment(sketch, "E6.6.38.0", {"start": v(18, 0.2) * mm, "end": v(18.5, 0.2) * mm});
            skLineSegment(sketch, "E6.9.38.0", {"start": v(18, 0) * mm, "end": v(18.5, 0) * mm});
            skLineSegment(sketch, "E6.0.39.0", {"start": v(19, 0) * mm, "end": v(19, 0.2) * mm});
            skLineSegment(sketch, "E6.3.39.0", {"start": v(19.5, 0) * mm, "end": v(19.5, 0.2) * mm});
            skLineSegment(sketch, "E6.6.39.0", {"start": v(19, 0.2) * mm, "end": v(19.5, 0.2) * mm});
            skLineSegment(sketch, "E6.9.39.0", {"start": v(19, 0) * mm, "end": v(19.5, 0) * mm});
            skLineSegment(sketch, "E7.0.20.0", {"start": v(1, 0.4) * mm, "end": v(1, 0.6) * mm});
            skLineSegment(sketch, "E7.3.20.0", {"start": v(0.5, 0.4) * mm, "end": v(1, 0.4) * mm});
            skLineSegment(sketch, "E7.6.20.0", {"start": v(0.5, 0.6) * mm, "end": v(1, 0.6) * mm});
            skLineSegment(sketch, "E7.9.20.0", {"start": v(0.5, 0.4) * mm, "end": v(0.5, 0.6) * mm});
            skLineSegment(sketch, "E7.0.21.0", {"start": v(2, 0.4) * mm, "end": v(2, 0.6) * mm});
            skLineSegment(sketch, "E7.3.21.0", {"start": v(1.5, 0.4) * mm, "end": v(2, 0.4) * mm});
            skLineSegment(sketch, "E7.6.21.0", {"start": v(1.5, 0.6) * mm, "end": v(2, 0.6) * mm});
            skLineSegment(sketch, "E7.9.21.0", {"start": v(1.5, 0.4) * mm, "end": v(1.5, 0.6) * mm});
            skLineSegment(sketch, "E7.0.22.0", {"start": v(3, 0.4) * mm, "end": v(3, 0.6) * mm});
            skLineSegment(sketch, "E7.3.22.0", {"start": v(2.5, 0.4) * mm, "end": v(3, 0.4) * mm});
            skLineSegment(sketch, "E7.6.22.0", {"start": v(2.5, 0.6) * mm, "end": v(3, 0.6) * mm});
            skLineSegment(sketch, "E7.9.22.0", {"start": v(2.5, 0.4) * mm, "end": v(2.5, 0.6) * mm});
            skLineSegment(sketch, "E7.0.23.0", {"start": v(4, 0.4) * mm, "end": v(4, 0.6) * mm});
            skLineSegment(sketch, "E7.3.23.0", {"start": v(3.5, 0.4) * mm, "end": v(4, 0.4) * mm});
            skLineSegment(sketch, "E7.6.23.0", {"start": v(3.5, 0.6) * mm, "end": v(4, 0.6) * mm});
            skLineSegment(sketch, "E7.9.23.0", {"start": v(3.5, 0.4) * mm, "end": v(3.5, 0.6) * mm});
            skLineSegment(sketch, "E7.0.24.0", {"start": v(5, 0.4) * mm, "end": v(5, 0.6) * mm});
            skLineSegment(sketch, "E7.3.24.0", {"start": v(4.5, 0.4) * mm, "end": v(5, 0.4) * mm});
            skLineSegment(sketch, "E7.6.24.0", {"start": v(4.5, 0.6) * mm, "end": v(5, 0.6) * mm});
            skLineSegment(sketch, "E7.9.24.0", {"start": v(4.5, 0.4) * mm, "end": v(4.5, 0.6) * mm});
            skLineSegment(sketch, "E7.0.25.0", {"start": v(6, 0.4) * mm, "end": v(6, 0.6) * mm});
            skLineSegment(sketch, "E7.3.25.0", {"start": v(5.5, 0.4) * mm, "end": v(6, 0.4) * mm});
            skLineSegment(sketch, "E7.6.25.0", {"start": v(5.5, 0.6) * mm, "end": v(6, 0.6) * mm});
            skLineSegment(sketch, "E7.9.25.0", {"start": v(5.5, 0.4) * mm, "end": v(5.5, 0.6) * mm});
            skLineSegment(sketch, "E7.0.26.0", {"start": v(7, 0.4) * mm, "end": v(7, 0.6) * mm});
            skLineSegment(sketch, "E7.3.26.0", {"start": v(6.5, 0.4) * mm, "end": v(7, 0.4) * mm});
            skLineSegment(sketch, "E7.6.26.0", {"start": v(6.5, 0.6) * mm, "end": v(7, 0.6) * mm});
            skLineSegment(sketch, "E7.9.26.0", {"start": v(6.5, 0.4) * mm, "end": v(6.5, 0.6) * mm});
            skLineSegment(sketch, "E7.0.27.0", {"start": v(8, 0.4) * mm, "end": v(8, 0.6) * mm});
            skLineSegment(sketch, "E7.3.27.0", {"start": v(7.5, 0.4) * mm, "end": v(8, 0.4) * mm});
            skLineSegment(sketch, "E7.6.27.0", {"start": v(7.5, 0.6) * mm, "end": v(8, 0.6) * mm});
            skLineSegment(sketch, "E7.9.27.0", {"start": v(7.5, 0.4) * mm, "end": v(7.5, 0.6) * mm});
            skLineSegment(sketch, "E7.0.28.0", {"start": v(9, 0.4) * mm, "end": v(9, 0.6) * mm});
            skLineSegment(sketch, "E7.3.28.0", {"start": v(8.5, 0.4) * mm, "end": v(9, 0.4) * mm});
            skLineSegment(sketch, "E7.6.28.0", {"start": v(8.5, 0.6) * mm, "end": v(9, 0.6) * mm});
            skLineSegment(sketch, "E7.9.28.0", {"start": v(8.5, 0.4) * mm, "end": v(8.5, 0.6) * mm});
            skLineSegment(sketch, "E7.0.29.0", {"start": v(10, 0.4) * mm, "end": v(10, 0.6) * mm});
            skLineSegment(sketch, "E7.3.29.0", {"start": v(9.5, 0.4) * mm, "end": v(10, 0.4) * mm});
            skLineSegment(sketch, "E7.6.29.0", {"start": v(9.5, 0.6) * mm, "end": v(10, 0.6) * mm});
            skLineSegment(sketch, "E7.9.29.0", {"start": v(9.5, 0.4) * mm, "end": v(9.5, 0.6) * mm});
            skLineSegment(sketch, "E7.0.30.0", {"start": v(11, 0.4) * mm, "end": v(11, 0.6) * mm});
            skLineSegment(sketch, "E7.3.30.0", {"start": v(10.5, 0.4) * mm, "end": v(11, 0.4) * mm});
            skLineSegment(sketch, "E7.6.30.0", {"start": v(10.5, 0.6) * mm, "end": v(11, 0.6) * mm});
            skLineSegment(sketch, "E7.9.30.0", {"start": v(10.5, 0.4) * mm, "end": v(10.5, 0.6) * mm});
            skLineSegment(sketch, "E7.0.31.0", {"start": v(12, 0.4) * mm, "end": v(12, 0.6) * mm});
            skLineSegment(sketch, "E7.3.31.0", {"start": v(11.5, 0.4) * mm, "end": v(12, 0.4) * mm});
            skLineSegment(sketch, "E7.6.31.0", {"start": v(11.5, 0.6) * mm, "end": v(12, 0.6) * mm});
            skLineSegment(sketch, "E7.9.31.0", {"start": v(11.5, 0.4) * mm, "end": v(11.5, 0.6) * mm});
            skLineSegment(sketch, "E7.0.32.0", {"start": v(13, 0.4) * mm, "end": v(13, 0.6) * mm});
            skLineSegment(sketch, "E7.3.32.0", {"start": v(12.5, 0.4) * mm, "end": v(13, 0.4) * mm});
            skLineSegment(sketch, "E7.6.32.0", {"start": v(12.5, 0.6) * mm, "end": v(13, 0.6) * mm});
            skLineSegment(sketch, "E7.9.32.0", {"start": v(12.5, 0.4) * mm, "end": v(12.5, 0.6) * mm});
            skLineSegment(sketch, "E7.0.33.0", {"start": v(14, 0.4) * mm, "end": v(14, 0.6) * mm});
            skLineSegment(sketch, "E7.3.33.0", {"start": v(13.5, 0.4) * mm, "end": v(14, 0.4) * mm});
            skLineSegment(sketch, "E7.6.33.0", {"start": v(13.5, 0.6) * mm, "end": v(14, 0.6) * mm});
            skLineSegment(sketch, "E7.9.33.0", {"start": v(13.5, 0.4) * mm, "end": v(13.5, 0.6) * mm});
            skLineSegment(sketch, "E7.0.34.0", {"start": v(15, 0.4) * mm, "end": v(15, 0.6) * mm});
            skLineSegment(sketch, "E7.3.34.0", {"start": v(14.5, 0.4) * mm, "end": v(15, 0.4) * mm});
            skLineSegment(sketch, "E7.6.34.0", {"start": v(14.5, 0.6) * mm, "end": v(15, 0.6) * mm});
            skLineSegment(sketch, "E7.9.34.0", {"start": v(14.5, 0.4) * mm, "end": v(14.5, 0.6) * mm});
            skLineSegment(sketch, "E7.0.35.0", {"start": v(16, 0.4) * mm, "end": v(16, 0.6) * mm});
            skLineSegment(sketch, "E7.3.35.0", {"start": v(15.5, 0.4) * mm, "end": v(16, 0.4) * mm});
            skLineSegment(sketch, "E7.6.35.0", {"start": v(15.5, 0.6) * mm, "end": v(16, 0.6) * mm});
            skLineSegment(sketch, "E7.9.35.0", {"start": v(15.5, 0.4) * mm, "end": v(15.5, 0.6) * mm});
            skLineSegment(sketch, "E7.0.36.0", {"start": v(17, 0.4) * mm, "end": v(17, 0.6) * mm});
            skLineSegment(sketch, "E7.3.36.0", {"start": v(16.5, 0.4) * mm, "end": v(17, 0.4) * mm});
            skLineSegment(sketch, "E7.6.36.0", {"start": v(16.5, 0.6) * mm, "end": v(17, 0.6) * mm});
            skLineSegment(sketch, "E7.9.36.0", {"start": v(16.5, 0.4) * mm, "end": v(16.5, 0.6) * mm});
            skLineSegment(sketch, "E7.0.37.0", {"start": v(18, 0.4) * mm, "end": v(18, 0.6) * mm});
            skLineSegment(sketch, "E7.3.37.0", {"start": v(17.5, 0.4) * mm, "end": v(18, 0.4) * mm});
            skLineSegment(sketch, "E7.6.37.0", {"start": v(17.5, 0.6) * mm, "end": v(18, 0.6) * mm});
            skLineSegment(sketch, "E7.9.37.0", {"start": v(17.5, 0.4) * mm, "end": v(17.5, 0.6) * mm});
            skLineSegment(sketch, "E7.0.38.0", {"start": v(19, 0.4) * mm, "end": v(19, 0.6) * mm});
            skLineSegment(sketch, "E7.3.38.0", {"start": v(18.5, 0.4) * mm, "end": v(19, 0.4) * mm});
            skLineSegment(sketch, "E7.6.38.0", {"start": v(18.5, 0.6) * mm, "end": v(19, 0.6) * mm});
            skLineSegment(sketch, "E7.9.38.0", {"start": v(18.5, 0.4) * mm, "end": v(18.5, 0.6) * mm});
            skLineSegment(sketch, "E7.0.39.0", {"start": v(20, 0.4) * mm, "end": v(20, 0.6) * mm});
            skLineSegment(sketch, "E7.3.39.0", {"start": v(19.5, 0.4) * mm, "end": v(20, 0.4) * mm});
            skLineSegment(sketch, "E7.6.39.0", {"start": v(19.5, 0.6) * mm, "end": v(20, 0.6) * mm});
            skLineSegment(sketch, "E7.9.39.0", {"start": v(19.5, 0.4) * mm, "end": v(19.5, 0.6) * mm});
            skLineSegment(sketch, "E8.0.1.0", {"start": v(3, 1) * mm, "end": v(3.5, 1) * mm});
            skLineSegment(sketch, "E8.0.1.1", {"start": v(1, 1) * mm, "end": v(1.5, 1) * mm});
            skLineSegment(sketch, "E8.0.1.2", {"start": v(17, 1.2) * mm, "end": v(17, 1.4) * mm});
            skLineSegment(sketch, "E8.0.1.3", {"start": v(13, 1.2) * mm, "end": v(13, 1.4) * mm});
            skLineSegment(sketch, "E8.0.1.4", {"start": v(4.5, 0.8) * mm, "end": v(4.5, 1) * mm});
            skLineSegment(sketch, "E8.0.1.5", {"start": v(10.5, 1.2) * mm, "end": v(11, 1.2) * mm});
            skLineSegment(sketch, "E8.0.1.6", {"start": v(1, 1.2) * mm, "end": v(1, 1.4) * mm});
            skLineSegment(sketch, "E8.0.1.7", {"start": v(4.5, 1.4) * mm, "end": v(5, 1.4) * mm});
            skLineSegment(sketch, "E8.0.1.8", {"start": v(7, 1) * mm, "end": v(7.5, 1) * mm});
            skLineSegment(sketch, "E8.0.1.9", {"start": v(0.5, 1.2) * mm, "end": v(1, 1.2) * mm});
            skLineSegment(sketch, "E8.0.1.10", {"start": v(6.5, 0.8) * mm, "end": v(6.5, 1) * mm});
            skLineSegment(sketch, "E8.0.1.11", {"start": v(2.5, 0.8) * mm, "end": v(2.5, 1) * mm});
            skLineSegment(sketch, "E8.0.1.12", {"start": v(17, 0.8) * mm, "end": v(17.5, 0.8) * mm});
            skLineSegment(sketch, "E8.0.1.13", {"start": v(18, 0.8) * mm, "end": v(18.5, 0.8) * mm});
            skLineSegment(sketch, "E8.0.1.14", {"start": v(8.5, 1.4) * mm, "end": v(9, 1.4) * mm});
            skLineSegment(sketch, "E8.0.1.15", {"start": v(7, 0.8) * mm, "end": v(7, 1) * mm});
            skLineSegment(sketch, "E8.0.1.16", {"start": v(8, 1) * mm, "end": v(8.5, 1) * mm});
            skLineSegment(sketch, "E8.0.1.17", {"start": v(12, 1) * mm, "end": v(12.5, 1) * mm});
            skLineSegment(sketch, "E8.0.1.18", {"start": v(12, 0.8) * mm, "end": v(12.5, 0.8) * mm});
            skLineSegment(sketch, "E8.0.1.19", {"start": v(18, 1) * mm, "end": v(18.5, 1) * mm});
            skLineSegment(sketch, "E8.0.1.20", {"start": v(10.5, 1.4) * mm, "end": v(11, 1.4) * mm});
            skLineSegment(sketch, "E8.0.1.21", {"start": v(8.5, 1.2) * mm, "end": v(8.5, 1.4) * mm});
            skLineSegment(sketch, "E8.0.1.22", {"start": v(13, 0.8) * mm, "end": v(13.5, 0.8) * mm});
            skLineSegment(sketch, "E8.0.1.23", {"start": v(14.5, 1.2) * mm, "end": v(15, 1.2) * mm});
            skLineSegment(sketch, "E8.0.1.24", {"start": v(7, 1.2) * mm, "end": v(7, 1.4) * mm});
            skLineSegment(sketch, "E8.0.1.25", {"start": v(1, 0.8) * mm, "end": v(1.5, 0.8) * mm});
            skLineSegment(sketch, "E8.0.1.26", {"start": v(5, 1) * mm, "end": v(5.5, 1) * mm});
            skLineSegment(sketch, "E8.0.1.27", {"start": v(18.5, 1.4) * mm, "end": v(19, 1.4) * mm});
            skLineSegment(sketch, "E8.0.1.28", {"start": v(9, 1.2) * mm, "end": v(9, 1.4) * mm});
            skLineSegment(sketch, "E8.0.1.29", {"start": v(2, 1) * mm, "end": v(2.5, 1) * mm});
            skLineSegment(sketch, "E8.0.1.30", {"start": v(10, 1) * mm, "end": v(10.5, 1) * mm});
            skLineSegment(sketch, "E8.0.1.31", {"start": v(14.5, 1.4) * mm, "end": v(15, 1.4) * mm});
            skLineSegment(sketch, "E8.0.1.32", {"start": v(9, 0.8) * mm, "end": v(9.5, 0.8) * mm});
            skLineSegment(sketch, "E8.0.1.33", {"start": v(20, 1.2) * mm, "end": v(20, 1.4) * mm});
            skLineSegment(sketch, "E8.0.1.34", {"start": v(12.5, 1.2) * mm, "end": v(12.5, 1.4) * mm});
            skLineSegment(sketch, "E8.0.1.35", {"start": v(4.5, 1.2) * mm, "end": v(5, 1.2) * mm});
            skLineSegment(sketch, "E8.0.1.36", {"start": v(8, 0.8) * mm, "end": v(8.5, 0.8) * mm});
            skLineSegment(sketch, "E8.0.1.37", {"start": v(12.5, 0.8) * mm, "end": v(12.5, 1) * mm});
            skLineSegment(sketch, "E8.0.1.38", {"start": v(10, 0.8) * mm, "end": v(10.5, 0.8) * mm});
            skLineSegment(sketch, "E8.0.1.39", {"start": v(18.5, 1.2) * mm, "end": v(18.5, 1.4) * mm});
            skLineSegment(sketch, "E8.0.1.40", {"start": v(18.5, 1.2) * mm, "end": v(19, 1.2) * mm});
            skLineSegment(sketch, "E8.0.1.41", {"start": v(0.5, 1.4) * mm, "end": v(1, 1.4) * mm});
            skLineSegment(sketch, "E8.0.1.42", {"start": v(14, 1) * mm, "end": v(14.5, 1) * mm});
            skLineSegment(sketch, "E8.0.1.43", {"start": v(8.5, 0.8) * mm, "end": v(8.5, 1) * mm});
            skLineSegment(sketch, "E8.0.1.44", {"start": v(2.5, 1.4) * mm, "end": v(3, 1.4) * mm});
            skLineSegment(sketch, "E8.0.1.45", {"start": v(16.5, 1.4) * mm, "end": v(17, 1.4) * mm});
            skLineSegment(sketch, "E8.0.1.46", {"start": v(2, 0.8) * mm, "end": v(2.5, 0.8) * mm});
            skLineSegment(sketch, "E8.0.1.47", {"start": v(7, 0.8) * mm, "end": v(7.5, 0.8) * mm});
            skLineSegment(sketch, "E8.0.1.48", {"start": v(3, 0.8) * mm, "end": v(3, 1) * mm});
            skLineSegment(sketch, "E8.0.1.49", {"start": v(16.5, 1.2) * mm, "end": v(17, 1.2) * mm});
            skLineSegment(sketch, "E8.0.1.50", {"start": v(11, 0.8) * mm, "end": v(11.5, 0.8) * mm});
            skLineSegment(sketch, "E8.0.1.51", {"start": v(4, 0.8) * mm, "end": v(4.5, 0.8) * mm});
            skLineSegment(sketch, "E8.0.1.52", {"start": v(16, 0.8) * mm, "end": v(16.5, 0.8) * mm});
            skLineSegment(sketch, "E8.0.1.53", {"start": v(18.5, 0.8) * mm, "end": v(18.5, 1) * mm});
            skLineSegment(sketch, "E8.0.1.54", {"start": v(3, 1.2) * mm, "end": v(3, 1.4) * mm});
            skLineSegment(sketch, "E8.0.1.55", {"start": v(16.5, 1.2) * mm, "end": v(16.5, 1.4) * mm});
            skLineSegment(sketch, "E8.0.1.56", {"start": v(14.5, 0.8) * mm, "end": v(14.5, 1) * mm});
            skLineSegment(sketch, "E8.0.1.57", {"start": v(4.5, 1.2) * mm, "end": v(4.5, 1.4) * mm});
            skLineSegment(sketch, "E8.0.1.58", {"start": v(16, 1) * mm, "end": v(16.5, 1) * mm});
            skLineSegment(sketch, "E8.0.1.59", {"start": v(8.5, 1.2) * mm, "end": v(9, 1.2) * mm});
            skLineSegment(sketch, "E8.0.1.60", {"start": v(5, 0.8) * mm, "end": v(5.5, 0.8) * mm});
            skLineSegment(sketch, "E8.0.1.61", {"start": v(3, 0.8) * mm, "end": v(3.5, 0.8) * mm});
            skLineSegment(sketch, "E8.0.1.62", {"start": v(9, 0.8) * mm, "end": v(9, 1) * mm});
            skLineSegment(sketch, "E8.0.1.63", {"start": v(9, 1) * mm, "end": v(9.5, 1) * mm});
            skLineSegment(sketch, "E8.0.1.64", {"start": v(4, 1) * mm, "end": v(4.5, 1) * mm});
            skLineSegment(sketch, "E8.0.1.65", {"start": v(19.5, 1.2) * mm, "end": v(20, 1.2) * mm});
            skLineSegment(sketch, "E8.0.1.66", {"start": v(6.5, 1.2) * mm, "end": v(7, 1.2) * mm});
            skLineSegment(sketch, "E8.0.1.67", {"start": v(6, 1) * mm, "end": v(6.5, 1) * mm});
            skLineSegment(sketch, "E8.0.1.68", {"start": v(6, 0.8) * mm, "end": v(6.5, 0.8) * mm});
            skLineSegment(sketch, "E8.0.1.69", {"start": v(5, 0.8) * mm, "end": v(5, 1) * mm});
            skLineSegment(sketch, "E8.0.1.70", {"start": v(19.5, 0.8) * mm, "end": v(19.5, 1) * mm});
            skLineSegment(sketch, "E8.0.1.72", {"start": v(16.5, 0.8) * mm, "end": v(16.5, 1) * mm});
            skLineSegment(sketch, "E8.0.1.73", {"start": v(12.5, 1.4) * mm, "end": v(13, 1.4) * mm});
            skLineSegment(sketch, "E8.0.1.74", {"start": v(6.5, 1.4) * mm, "end": v(7, 1.4) * mm});
            skLineSegment(sketch, "E8.0.1.75", {"start": v(2.5, 1.2) * mm, "end": v(3, 1.2) * mm});
            skLineSegment(sketch, "E8.0.1.76", {"start": v(12.5, 1.2) * mm, "end": v(13, 1.2) * mm});
            skLineSegment(sketch, "E8.0.1.77", {"start": v(5, 1.2) * mm, "end": v(5, 1.4) * mm});
            skLineSegment(sketch, "E8.0.1.78", {"start": v(14, 0.8) * mm, "end": v(14.5, 0.8) * mm});
            skLineSegment(sketch, "E8.0.1.79", {"start": v(0.5, 1.2) * mm, "end": v(0.5, 1.4) * mm});
            skLineSegment(sketch, "E8.0.1.80", {"start": v(10.5, 0.8) * mm, "end": v(10.5, 1) * mm});
            skLineSegment(sketch, "E8.0.1.81", {"start": v(1, 0.8) * mm, "end": v(1, 1) * mm});
            skLineSegment(sketch, "E8.0.1.82", {"start": v(17, 1) * mm, "end": v(17.5, 1) * mm});
            skLineSegment(sketch, "E8.0.1.83", {"start": v(19, 1.2) * mm, "end": v(19, 1.4) * mm});
            skLineSegment(sketch, "E8.0.1.84", {"start": v(1.5, 0.8) * mm, "end": v(1.5, 1) * mm});
            skLineSegment(sketch, "E8.0.1.85", {"start": v(19, 1) * mm, "end": v(19.5, 1) * mm});
            skLineSegment(sketch, "E8.0.1.86", {"start": v(11, 1) * mm, "end": v(11.5, 1) * mm});
            skLineSegment(sketch, "E8.0.1.87", {"start": v(15.5, 0.8) * mm, "end": v(15.5, 1) * mm});
            skLineSegment(sketch, "E8.0.1.88", {"start": v(3.5, 0.8) * mm, "end": v(3.5, 1) * mm});
            skLineSegment(sketch, "E8.0.1.89", {"start": v(19.5, 1.4) * mm, "end": v(20, 1.4) * mm});
            skLineSegment(sketch, "E8.0.1.90", {"start": v(15, 0.8) * mm, "end": v(15, 1) * mm});
            skLineSegment(sketch, "E8.0.1.91", {"start": v(19, 0.8) * mm, "end": v(19, 1) * mm});
            skLineSegment(sketch, "E8.0.1.92", {"start": v(16, 0.8) * mm, "end": v(16, 1) * mm});
            skLineSegment(sketch, "E8.0.1.93", {"start": v(6.5, 1.2) * mm, "end": v(6.5, 1.4) * mm});
            skLineSegment(sketch, "E8.0.1.94", {"start": v(5.5, 0.8) * mm, "end": v(5.5, 1) * mm});
            skLineSegment(sketch, "E8.0.1.95", {"start": v(14.5, 1.2) * mm, "end": v(14.5, 1.4) * mm});
            skLineSegment(sketch, "E8.0.1.96", {"start": v(18, 0.8) * mm, "end": v(18, 1) * mm});
            skLineSegment(sketch, "E8.0.1.97", {"start": v(19, 0.8) * mm, "end": v(19.5, 0.8) * mm});
            skLineSegment(sketch, "E8.0.1.98", {"start": v(10.5, 1.2) * mm, "end": v(10.5, 1.4) * mm});
            skLineSegment(sketch, "E8.0.1.99", {"start": v(7.5, 0.8) * mm, "end": v(7.5, 1) * mm});
            skLineSegment(sketch, "E8.0.1.100", {"start": v(9.5, 0.8) * mm, "end": v(9.5, 1) * mm});
            skLineSegment(sketch, "E8.0.1.101", {"start": v(17.5, 0.8) * mm, "end": v(17.5, 1) * mm});
            skLineSegment(sketch, "E8.0.1.102", {"start": v(17, 0.8) * mm, "end": v(17, 1) * mm});
            skLineSegment(sketch, "E8.0.1.103", {"start": v(11, 1.2) * mm, "end": v(11, 1.4) * mm});
            skLineSegment(sketch, "E8.0.1.104", {"start": v(15, 0.8) * mm, "end": v(15.5, 0.8) * mm});
            skLineSegment(sketch, "E8.0.1.105", {"start": v(11.5, 0.8) * mm, "end": v(11.5, 1) * mm});
            skLineSegment(sketch, "E8.0.1.106", {"start": v(1.5, 1.2) * mm, "end": v(1.5, 1.4) * mm});
            skLineSegment(sketch, "E8.0.1.107", {"start": v(2.5, 1.2) * mm, "end": v(2.5, 1.4) * mm});
            skLineSegment(sketch, "E8.0.1.108", {"start": v(15, 1.2) * mm, "end": v(15, 1.4) * mm});
            skLineSegment(sketch, "E8.0.1.109", {"start": v(13, 0.8) * mm, "end": v(13, 1) * mm});
            skLineSegment(sketch, "E8.0.1.110", {"start": v(13, 1) * mm, "end": v(13.5, 1) * mm});
            skLineSegment(sketch, "E8.0.1.111", {"start": v(13.5, 0.8) * mm, "end": v(13.5, 1) * mm});
            skLineSegment(sketch, "E8.0.1.112", {"start": v(11, 0.8) * mm, "end": v(11, 1) * mm});
            skLineSegment(sketch, "E8.0.1.113", {"start": v(7.5, 1.4) * mm, "end": v(8, 1.4) * mm});
            skLineSegment(sketch, "E8.0.1.114", {"start": v(8, 1.2) * mm, "end": v(8, 1.4) * mm});
            skLineSegment(sketch, "E8.0.1.115", {"start": v(17.5, 1.2) * mm, "end": v(17.5, 1.4) * mm});
            skLineSegment(sketch, "E8.0.1.116", {"start": v(17.5, 1.4) * mm, "end": v(18, 1.4) * mm});
            skLineSegment(sketch, "E8.0.1.117", {"start": v(18, 1.2) * mm, "end": v(18, 1.4) * mm});
            skLineSegment(sketch, "E8.0.1.118", {"start": v(17.5, 1.2) * mm, "end": v(18, 1.2) * mm});
            skLineSegment(sketch, "E8.0.1.119", {"start": v(5.5, 1.2) * mm, "end": v(5.5, 1.4) * mm});
            skLineSegment(sketch, "E8.0.1.120", {"start": v(13.5, 1.2) * mm, "end": v(13.5, 1.4) * mm});
            skLineSegment(sketch, "E8.0.1.121", {"start": v(9.5, 1.2) * mm, "end": v(10, 1.2) * mm});
            skLineSegment(sketch, "E8.0.1.122", {"start": v(3.5, 1.2) * mm, "end": v(4, 1.2) * mm});
            skLineSegment(sketch, "E8.0.1.123", {"start": v(7.5, 1.2) * mm, "end": v(7.5, 1.4) * mm});
            skLineSegment(sketch, "E8.0.1.124", {"start": v(9.5, 1.4) * mm, "end": v(10, 1.4) * mm});
            skLineSegment(sketch, "E8.0.1.125", {"start": v(15.5, 1.2) * mm, "end": v(16, 1.2) * mm});
            skLineSegment(sketch, "E8.0.1.126", {"start": v(15.5, 1.2) * mm, "end": v(15.5, 1.4) * mm});
            skLineSegment(sketch, "E8.0.1.127", {"start": v(16, 1.2) * mm, "end": v(16, 1.4) * mm});
            skLineSegment(sketch, "E8.0.1.128", {"start": v(11.5, 1.2) * mm, "end": v(11.5, 1.4) * mm});
            skLineSegment(sketch, "E8.0.1.129", {"start": v(2, 1.2) * mm, "end": v(2, 1.4) * mm});
            skLineSegment(sketch, "E8.0.1.130", {"start": v(1.5, 1.2) * mm, "end": v(2, 1.2) * mm});
            skLineSegment(sketch, "E8.0.1.131", {"start": v(7.5, 1.2) * mm, "end": v(8, 1.2) * mm});
            skLineSegment(sketch, "E8.0.1.132", {"start": v(10, 0.8) * mm, "end": v(10, 1) * mm});
            skLineSegment(sketch, "E8.0.1.133", {"start": v(8, 0.8) * mm, "end": v(8, 1) * mm});
            skLineSegment(sketch, "E8.0.1.134", {"start": v(19.5, 1.2) * mm, "end": v(19.5, 1.4) * mm});
            skLineSegment(sketch, "E8.0.1.135", {"start": v(6, 1.2) * mm, "end": v(6, 1.4) * mm});
            skLineSegment(sketch, "E8.0.1.136", {"start": v(12, 0.8) * mm, "end": v(12, 1) * mm});
            skLineSegment(sketch, "E8.0.1.137", {"start": v(9.5, 1.2) * mm, "end": v(9.5, 1.4) * mm});
            skLineSegment(sketch, "E8.0.1.138", {"start": v(3.5, 1.2) * mm, "end": v(3.5, 1.4) * mm});
            skLineSegment(sketch, "E8.0.1.139", {"start": v(15.5, 1.4) * mm, "end": v(16, 1.4) * mm});
            skLineSegment(sketch, "E8.0.1.140", {"start": v(4, 0.8) * mm, "end": v(4, 1) * mm});
            skLineSegment(sketch, "E8.0.1.141", {"start": v(2, 0.8) * mm, "end": v(2, 1) * mm});
            skLineSegment(sketch, "E8.0.1.142", {"start": v(13.5, 1.4) * mm, "end": v(14, 1.4) * mm});
            skLineSegment(sketch, "E8.0.1.143", {"start": v(11.5, 1.4) * mm, "end": v(12, 1.4) * mm});
            skLineSegment(sketch, "E8.0.1.144", {"start": v(5.5, 1.4) * mm, "end": v(6, 1.4) * mm});
            skLineSegment(sketch, "E8.0.1.145", {"start": v(14, 0.8) * mm, "end": v(14, 1) * mm});
            skLineSegment(sketch, "E8.0.1.146", {"start": v(15, 1) * mm, "end": v(15.5, 1) * mm});
            skLineSegment(sketch, "E8.0.1.147", {"start": v(4, 1.2) * mm, "end": v(4, 1.4) * mm});
            skLineSegment(sketch, "E8.0.1.148", {"start": v(1.5, 1.4) * mm, "end": v(2, 1.4) * mm});
            skLineSegment(sketch, "E8.0.1.149", {"start": v(11.5, 1.2) * mm, "end": v(12, 1.2) * mm});
            skLineSegment(sketch, "E8.0.1.150", {"start": v(6, 0.8) * mm, "end": v(6, 1) * mm});
            skLineSegment(sketch, "E8.0.1.151", {"start": v(12, 1.2) * mm, "end": v(12, 1.4) * mm});
            skLineSegment(sketch, "E8.0.1.152", {"start": v(13.5, 1.2) * mm, "end": v(14, 1.2) * mm});
            skLineSegment(sketch, "E8.0.1.153", {"start": v(5.5, 1.2) * mm, "end": v(6, 1.2) * mm});
            skLineSegment(sketch, "E8.0.1.154", {"start": v(10, 1.2) * mm, "end": v(10, 1.4) * mm});
            skLineSegment(sketch, "E8.0.1.155", {"start": v(3.5, 1.4) * mm, "end": v(4, 1.4) * mm});
            skLineSegment(sketch, "E8.0.1.156", {"start": v(14, 1.2) * mm, "end": v(14, 1.4) * mm});
            skLineSegment(sketch, "E8.0.2.0", {"start": v(3, 1.8) * mm, "end": v(3.5, 1.8) * mm});
            skLineSegment(sketch, "E8.0.2.1", {"start": v(1, 1.8) * mm, "end": v(1.5, 1.8) * mm});
            skLineSegment(sketch, "E8.0.2.2", {"start": v(17, 2) * mm, "end": v(17, 2.2) * mm});
            skLineSegment(sketch, "E8.0.2.3", {"start": v(13, 2) * mm, "end": v(13, 2.2) * mm});
            skLineSegment(sketch, "E8.0.2.4", {"start": v(4.5, 1.6) * mm, "end": v(4.5, 1.8) * mm});
            skLineSegment(sketch, "E8.0.2.5", {"start": v(10.5, 2) * mm, "end": v(11, 2) * mm});
            skLineSegment(sketch, "E8.0.2.6", {"start": v(1, 2) * mm, "end": v(1, 2.2) * mm});
            skLineSegment(sketch, "E8.0.2.7", {"start": v(4.5, 2.2) * mm, "end": v(5, 2.2) * mm});
            skLineSegment(sketch, "E8.0.2.8", {"start": v(7, 1.8) * mm, "end": v(7.5, 1.8) * mm});
            skLineSegment(sketch, "E8.0.2.9", {"start": v(0.5, 2) * mm, "end": v(1, 2) * mm});
            skLineSegment(sketch, "E8.0.2.10", {"start": v(6.5, 1.6) * mm, "end": v(6.5, 1.8) * mm});
            skLineSegment(sketch, "E8.0.2.11", {"start": v(2.5, 1.6) * mm, "end": v(2.5, 1.8) * mm});
            skLineSegment(sketch, "E8.0.2.12", {"start": v(17, 1.6) * mm, "end": v(17.5, 1.6) * mm});
            skLineSegment(sketch, "E8.0.2.13", {"start": v(18, 1.6) * mm, "end": v(18.5, 1.6) * mm});
            skLineSegment(sketch, "E8.0.2.14", {"start": v(8.5, 2.2) * mm, "end": v(9, 2.2) * mm});
            skLineSegment(sketch, "E8.0.2.15", {"start": v(7, 1.6) * mm, "end": v(7, 1.8) * mm});
            skLineSegment(sketch, "E8.0.2.16", {"start": v(8, 1.8) * mm, "end": v(8.5, 1.8) * mm});
            skLineSegment(sketch, "E8.0.2.17", {"start": v(12, 1.8) * mm, "end": v(12.5, 1.8) * mm});
            skLineSegment(sketch, "E8.0.2.18", {"start": v(12, 1.6) * mm, "end": v(12.5, 1.6) * mm});
            skLineSegment(sketch, "E8.0.2.19", {"start": v(18, 1.8) * mm, "end": v(18.5, 1.8) * mm});
            skLineSegment(sketch, "E8.0.2.20", {"start": v(10.5, 2.2) * mm, "end": v(11, 2.2) * mm});
            skLineSegment(sketch, "E8.0.2.21", {"start": v(8.5, 2) * mm, "end": v(8.5, 2.2) * mm});
            skLineSegment(sketch, "E8.0.2.22", {"start": v(13, 1.6) * mm, "end": v(13.5, 1.6) * mm});
            skLineSegment(sketch, "E8.0.2.23", {"start": v(14.5, 2) * mm, "end": v(15, 2) * mm});
            skLineSegment(sketch, "E8.0.2.24", {"start": v(7, 2) * mm, "end": v(7, 2.2) * mm});
            skLineSegment(sketch, "E8.0.2.25", {"start": v(1, 1.6) * mm, "end": v(1.5, 1.6) * mm});
            skLineSegment(sketch, "E8.0.2.26", {"start": v(5, 1.8) * mm, "end": v(5.5, 1.8) * mm});
            skLineSegment(sketch, "E8.0.2.27", {"start": v(18.5, 2.2) * mm, "end": v(19, 2.2) * mm});
            skLineSegment(sketch, "E8.0.2.28", {"start": v(9, 2) * mm, "end": v(9, 2.2) * mm});
            skLineSegment(sketch, "E8.0.2.29", {"start": v(2, 1.8) * mm, "end": v(2.5, 1.8) * mm});
            skLineSegment(sketch, "E8.0.2.30", {"start": v(10, 1.8) * mm, "end": v(10.5, 1.8) * mm});
            skLineSegment(sketch, "E8.0.2.31", {"start": v(14.5, 2.2) * mm, "end": v(15, 2.2) * mm});
            skLineSegment(sketch, "E8.0.2.32", {"start": v(9, 1.6) * mm, "end": v(9.5, 1.6) * mm});
            skLineSegment(sketch, "E8.0.2.33", {"start": v(20, 2) * mm, "end": v(20, 2.2) * mm});
            skLineSegment(sketch, "E8.0.2.34", {"start": v(12.5, 2) * mm, "end": v(12.5, 2.2) * mm});
            skLineSegment(sketch, "E8.0.2.35", {"start": v(4.5, 2) * mm, "end": v(5, 2) * mm});
            skLineSegment(sketch, "E8.0.2.36", {"start": v(8, 1.6) * mm, "end": v(8.5, 1.6) * mm});
            skLineSegment(sketch, "E8.0.2.37", {"start": v(12.5, 1.6) * mm, "end": v(12.5, 1.8) * mm});
            skLineSegment(sketch, "E8.0.2.38", {"start": v(10, 1.6) * mm, "end": v(10.5, 1.6) * mm});
            skLineSegment(sketch, "E8.0.2.39", {"start": v(18.5, 2) * mm, "end": v(18.5, 2.2) * mm});
            skLineSegment(sketch, "E8.0.2.40", {"start": v(18.5, 2) * mm, "end": v(19, 2) * mm});
            skLineSegment(sketch, "E8.0.2.41", {"start": v(0.5, 2.2) * mm, "end": v(1, 2.2) * mm});
            skLineSegment(sketch, "E8.0.2.42", {"start": v(14, 1.8) * mm, "end": v(14.5, 1.8) * mm});
            skLineSegment(sketch, "E8.0.2.43", {"start": v(8.5, 1.6) * mm, "end": v(8.5, 1.8) * mm});
            skLineSegment(sketch, "E8.0.2.44", {"start": v(2.5, 2.2) * mm, "end": v(3, 2.2) * mm});
            skLineSegment(sketch, "E8.0.2.45", {"start": v(16.5, 2.2) * mm, "end": v(17, 2.2) * mm});
            skLineSegment(sketch, "E8.0.2.46", {"start": v(2, 1.6) * mm, "end": v(2.5, 1.6) * mm});
            skLineSegment(sketch, "E8.0.2.47", {"start": v(7, 1.6) * mm, "end": v(7.5, 1.6) * mm});
            skLineSegment(sketch, "E8.0.2.48", {"start": v(3, 1.6) * mm, "end": v(3, 1.8) * mm});
            skLineSegment(sketch, "E8.0.2.49", {"start": v(16.5, 2) * mm, "end": v(17, 2) * mm});
            skLineSegment(sketch, "E8.0.2.50", {"start": v(11, 1.6) * mm, "end": v(11.5, 1.6) * mm});
            skLineSegment(sketch, "E8.0.2.51", {"start": v(4, 1.6) * mm, "end": v(4.5, 1.6) * mm});
            skLineSegment(sketch, "E8.0.2.52", {"start": v(16, 1.6) * mm, "end": v(16.5, 1.6) * mm});
            skLineSegment(sketch, "E8.0.2.53", {"start": v(18.5, 1.6) * mm, "end": v(18.5, 1.8) * mm});
            skLineSegment(sketch, "E8.0.2.54", {"start": v(3, 2) * mm, "end": v(3, 2.2) * mm});
            skLineSegment(sketch, "E8.0.2.55", {"start": v(16.5, 2) * mm, "end": v(16.5, 2.2) * mm});
            skLineSegment(sketch, "E8.0.2.56", {"start": v(14.5, 1.6) * mm, "end": v(14.5, 1.8) * mm});
            skLineSegment(sketch, "E8.0.2.57", {"start": v(4.5, 2) * mm, "end": v(4.5, 2.2) * mm});
            skLineSegment(sketch, "E8.0.2.58", {"start": v(16, 1.8) * mm, "end": v(16.5, 1.8) * mm});
            skLineSegment(sketch, "E8.0.2.59", {"start": v(8.5, 2) * mm, "end": v(9, 2) * mm});
            skLineSegment(sketch, "E8.0.2.60", {"start": v(5, 1.6) * mm, "end": v(5.5, 1.6) * mm});
            skLineSegment(sketch, "E8.0.2.61", {"start": v(3, 1.6) * mm, "end": v(3.5, 1.6) * mm});
            skLineSegment(sketch, "E8.0.2.62", {"start": v(9, 1.6) * mm, "end": v(9, 1.8) * mm});
            skLineSegment(sketch, "E8.0.2.63", {"start": v(9, 1.8) * mm, "end": v(9.5, 1.8) * mm});
            skLineSegment(sketch, "E8.0.2.64", {"start": v(4, 1.8) * mm, "end": v(4.5, 1.8) * mm});
            skLineSegment(sketch, "E8.0.2.65", {"start": v(19.5, 2) * mm, "end": v(20, 2) * mm});
            skLineSegment(sketch, "E8.0.2.66", {"start": v(6.5, 2) * mm, "end": v(7, 2) * mm});
            skLineSegment(sketch, "E8.0.2.67", {"start": v(6, 1.8) * mm, "end": v(6.5, 1.8) * mm});
            skLineSegment(sketch, "E8.0.2.68", {"start": v(6, 1.6) * mm, "end": v(6.5, 1.6) * mm});
            skLineSegment(sketch, "E8.0.2.69", {"start": v(5, 1.6) * mm, "end": v(5, 1.8) * mm});
            skLineSegment(sketch, "E8.0.2.70", {"start": v(19.5, 1.6) * mm, "end": v(19.5, 1.8) * mm});
            skLineSegment(sketch, "E8.0.2.72", {"start": v(16.5, 1.6) * mm, "end": v(16.5, 1.8) * mm});
            skLineSegment(sketch, "E8.0.2.73", {"start": v(12.5, 2.2) * mm, "end": v(13, 2.2) * mm});
            skLineSegment(sketch, "E8.0.2.74", {"start": v(6.5, 2.2) * mm, "end": v(7, 2.2) * mm});
            skLineSegment(sketch, "E8.0.2.75", {"start": v(2.5, 2) * mm, "end": v(3, 2) * mm});
            skLineSegment(sketch, "E8.0.2.76", {"start": v(12.5, 2) * mm, "end": v(13, 2) * mm});
            skLineSegment(sketch, "E8.0.2.77", {"start": v(5, 2) * mm, "end": v(5, 2.2) * mm});
            skLineSegment(sketch, "E8.0.2.78", {"start": v(14, 1.6) * mm, "end": v(14.5, 1.6) * mm});
            skLineSegment(sketch, "E8.0.2.79", {"start": v(0.5, 2) * mm, "end": v(0.5, 2.2) * mm});
            skLineSegment(sketch, "E8.0.2.80", {"start": v(10.5, 1.6) * mm, "end": v(10.5, 1.8) * mm});
            skLineSegment(sketch, "E8.0.2.81", {"start": v(1, 1.6) * mm, "end": v(1, 1.8) * mm});
            skLineSegment(sketch, "E8.0.2.82", {"start": v(17, 1.8) * mm, "end": v(17.5, 1.8) * mm});
            skLineSegment(sketch, "E8.0.2.83", {"start": v(19, 2) * mm, "end": v(19, 2.2) * mm});
            skLineSegment(sketch, "E8.0.2.84", {"start": v(1.5, 1.6) * mm, "end": v(1.5, 1.8) * mm});
            skLineSegment(sketch, "E8.0.2.85", {"start": v(19, 1.8) * mm, "end": v(19.5, 1.8) * mm});
            skLineSegment(sketch, "E8.0.2.86", {"start": v(11, 1.8) * mm, "end": v(11.5, 1.8) * mm});
            skLineSegment(sketch, "E8.0.2.87", {"start": v(15.5, 1.6) * mm, "end": v(15.5, 1.8) * mm});
            skLineSegment(sketch, "E8.0.2.88", {"start": v(3.5, 1.6) * mm, "end": v(3.5, 1.8) * mm});
            skLineSegment(sketch, "E8.0.2.89", {"start": v(19.5, 2.2) * mm, "end": v(20, 2.2) * mm});
            skLineSegment(sketch, "E8.0.2.90", {"start": v(15, 1.6) * mm, "end": v(15, 1.8) * mm});
            skLineSegment(sketch, "E8.0.2.91", {"start": v(19, 1.6) * mm, "end": v(19, 1.8) * mm});
            skLineSegment(sketch, "E8.0.2.92", {"start": v(16, 1.6) * mm, "end": v(16, 1.8) * mm});
            skLineSegment(sketch, "E8.0.2.93", {"start": v(6.5, 2) * mm, "end": v(6.5, 2.2) * mm});
            skLineSegment(sketch, "E8.0.2.94", {"start": v(5.5, 1.6) * mm, "end": v(5.5, 1.8) * mm});
            skLineSegment(sketch, "E8.0.2.95", {"start": v(14.5, 2) * mm, "end": v(14.5, 2.2) * mm});
            skLineSegment(sketch, "E8.0.2.96", {"start": v(18, 1.6) * mm, "end": v(18, 1.8) * mm});
            skLineSegment(sketch, "E8.0.2.97", {"start": v(19, 1.6) * mm, "end": v(19.5, 1.6) * mm});
            skLineSegment(sketch, "E8.0.2.98", {"start": v(10.5, 2) * mm, "end": v(10.5, 2.2) * mm});
            skLineSegment(sketch, "E8.0.2.99", {"start": v(7.5, 1.6) * mm, "end": v(7.5, 1.8) * mm});
            skLineSegment(sketch, "E8.0.2.100", {"start": v(9.5, 1.6) * mm, "end": v(9.5, 1.8) * mm});
            skLineSegment(sketch, "E8.0.2.101", {"start": v(17.5, 1.6) * mm, "end": v(17.5, 1.8) * mm});
            skLineSegment(sketch, "E8.0.2.102", {"start": v(17, 1.6) * mm, "end": v(17, 1.8) * mm});
            skLineSegment(sketch, "E8.0.2.103", {"start": v(11, 2) * mm, "end": v(11, 2.2) * mm});
            skLineSegment(sketch, "E8.0.2.104", {"start": v(15, 1.6) * mm, "end": v(15.5, 1.6) * mm});
            skLineSegment(sketch, "E8.0.2.105", {"start": v(11.5, 1.6) * mm, "end": v(11.5, 1.8) * mm});
            skLineSegment(sketch, "E8.0.2.106", {"start": v(1.5, 2) * mm, "end": v(1.5, 2.2) * mm});
            skLineSegment(sketch, "E8.0.2.107", {"start": v(2.5, 2) * mm, "end": v(2.5, 2.2) * mm});
            skLineSegment(sketch, "E8.0.2.108", {"start": v(15, 2) * mm, "end": v(15, 2.2) * mm});
            skLineSegment(sketch, "E8.0.2.109", {"start": v(13, 1.6) * mm, "end": v(13, 1.8) * mm});
            skLineSegment(sketch, "E8.0.2.110", {"start": v(13, 1.8) * mm, "end": v(13.5, 1.8) * mm});
            skLineSegment(sketch, "E8.0.2.111", {"start": v(13.5, 1.6) * mm, "end": v(13.5, 1.8) * mm});
            skLineSegment(sketch, "E8.0.2.112", {"start": v(11, 1.6) * mm, "end": v(11, 1.8) * mm});
            skLineSegment(sketch, "E8.0.2.113", {"start": v(7.5, 2.2) * mm, "end": v(8, 2.2) * mm});
            skLineSegment(sketch, "E8.0.2.114", {"start": v(8, 2) * mm, "end": v(8, 2.2) * mm});
            skLineSegment(sketch, "E8.0.2.115", {"start": v(17.5, 2) * mm, "end": v(17.5, 2.2) * mm});
            skLineSegment(sketch, "E8.0.2.116", {"start": v(17.5, 2.2) * mm, "end": v(18, 2.2) * mm});
            skLineSegment(sketch, "E8.0.2.117", {"start": v(18, 2) * mm, "end": v(18, 2.2) * mm});
            skLineSegment(sketch, "E8.0.2.118", {"start": v(17.5, 2) * mm, "end": v(18, 2) * mm});
            skLineSegment(sketch, "E8.0.2.119", {"start": v(5.5, 2) * mm, "end": v(5.5, 2.2) * mm});
            skLineSegment(sketch, "E8.0.2.120", {"start": v(13.5, 2) * mm, "end": v(13.5, 2.2) * mm});
            skLineSegment(sketch, "E8.0.2.121", {"start": v(9.5, 2) * mm, "end": v(10, 2) * mm});
            skLineSegment(sketch, "E8.0.2.122", {"start": v(3.5, 2) * mm, "end": v(4, 2) * mm});
            skLineSegment(sketch, "E8.0.2.123", {"start": v(7.5, 2) * mm, "end": v(7.5, 2.2) * mm});
            skLineSegment(sketch, "E8.0.2.124", {"start": v(9.5, 2.2) * mm, "end": v(10, 2.2) * mm});
            skLineSegment(sketch, "E8.0.2.125", {"start": v(15.5, 2) * mm, "end": v(16, 2) * mm});
            skLineSegment(sketch, "E8.0.2.126", {"start": v(15.5, 2) * mm, "end": v(15.5, 2.2) * mm});
            skLineSegment(sketch, "E8.0.2.127", {"start": v(16, 2) * mm, "end": v(16, 2.2) * mm});
            skLineSegment(sketch, "E8.0.2.128", {"start": v(11.5, 2) * mm, "end": v(11.5, 2.2) * mm});
            skLineSegment(sketch, "E8.0.2.129", {"start": v(2, 2) * mm, "end": v(2, 2.2) * mm});
            skLineSegment(sketch, "E8.0.2.130", {"start": v(1.5, 2) * mm, "end": v(2, 2) * mm});
            skLineSegment(sketch, "E8.0.2.131", {"start": v(7.5, 2) * mm, "end": v(8, 2) * mm});
            skLineSegment(sketch, "E8.0.2.132", {"start": v(10, 1.6) * mm, "end": v(10, 1.8) * mm});
            skLineSegment(sketch, "E8.0.2.133", {"start": v(8, 1.6) * mm, "end": v(8, 1.8) * mm});
            skLineSegment(sketch, "E8.0.2.134", {"start": v(19.5, 2) * mm, "end": v(19.5, 2.2) * mm});
            skLineSegment(sketch, "E8.0.2.135", {"start": v(6, 2) * mm, "end": v(6, 2.2) * mm});
            skLineSegment(sketch, "E8.0.2.136", {"start": v(12, 1.6) * mm, "end": v(12, 1.8) * mm});
            skLineSegment(sketch, "E8.0.2.137", {"start": v(9.5, 2) * mm, "end": v(9.5, 2.2) * mm});
            skLineSegment(sketch, "E8.0.2.138", {"start": v(3.5, 2) * mm, "end": v(3.5, 2.2) * mm});
            skLineSegment(sketch, "E8.0.2.139", {"start": v(15.5, 2.2) * mm, "end": v(16, 2.2) * mm});
            skLineSegment(sketch, "E8.0.2.140", {"start": v(4, 1.6) * mm, "end": v(4, 1.8) * mm});
            skLineSegment(sketch, "E8.0.2.141", {"start": v(2, 1.6) * mm, "end": v(2, 1.8) * mm});
            skLineSegment(sketch, "E8.0.2.142", {"start": v(13.5, 2.2) * mm, "end": v(14, 2.2) * mm});
            skLineSegment(sketch, "E8.0.2.143", {"start": v(11.5, 2.2) * mm, "end": v(12, 2.2) * mm});
            skLineSegment(sketch, "E8.0.2.144", {"start": v(5.5, 2.2) * mm, "end": v(6, 2.2) * mm});
            skLineSegment(sketch, "E8.0.2.145", {"start": v(14, 1.6) * mm, "end": v(14, 1.8) * mm});
            skLineSegment(sketch, "E8.0.2.146", {"start": v(15, 1.8) * mm, "end": v(15.5, 1.8) * mm});
            skLineSegment(sketch, "E8.0.2.147", {"start": v(4, 2) * mm, "end": v(4, 2.2) * mm});
            skLineSegment(sketch, "E8.0.2.148", {"start": v(1.5, 2.2) * mm, "end": v(2, 2.2) * mm});
            skLineSegment(sketch, "E8.0.2.149", {"start": v(11.5, 2) * mm, "end": v(12, 2) * mm});
            skLineSegment(sketch, "E8.0.2.150", {"start": v(6, 1.6) * mm, "end": v(6, 1.8) * mm});
            skLineSegment(sketch, "E8.0.2.151", {"start": v(12, 2) * mm, "end": v(12, 2.2) * mm});
            skLineSegment(sketch, "E8.0.2.152", {"start": v(13.5, 2) * mm, "end": v(14, 2) * mm});
            skLineSegment(sketch, "E8.0.2.153", {"start": v(5.5, 2) * mm, "end": v(6, 2) * mm});
            skLineSegment(sketch, "E8.0.2.154", {"start": v(10, 2) * mm, "end": v(10, 2.2) * mm});
            skLineSegment(sketch, "E8.0.2.155", {"start": v(3.5, 2.2) * mm, "end": v(4, 2.2) * mm});
            skLineSegment(sketch, "E8.0.2.156", {"start": v(14, 2) * mm, "end": v(14, 2.2) * mm});
            skLineSegment(sketch, "E8.0.3.0", {"start": v(3, 2.6) * mm, "end": v(3.5, 2.6) * mm});
            skLineSegment(sketch, "E8.0.3.1", {"start": v(1, 2.6) * mm, "end": v(1.5, 2.6) * mm});
            skLineSegment(sketch, "E8.0.3.2", {"start": v(17, 2.8) * mm, "end": v(17, 3) * mm});
            skLineSegment(sketch, "E8.0.3.3", {"start": v(13, 2.8) * mm, "end": v(13, 3) * mm});
            skLineSegment(sketch, "E8.0.3.4", {"start": v(4.5, 2.4) * mm, "end": v(4.5, 2.6) * mm});
            skLineSegment(sketch, "E8.0.3.5", {"start": v(10.5, 2.8) * mm, "end": v(11, 2.8) * mm});
            skLineSegment(sketch, "E8.0.3.6", {"start": v(1, 2.8) * mm, "end": v(1, 3) * mm});
            skLineSegment(sketch, "E8.0.3.7", {"start": v(4.5, 3) * mm, "end": v(5, 3) * mm});
            skLineSegment(sketch, "E8.0.3.8", {"start": v(7, 2.6) * mm, "end": v(7.5, 2.6) * mm});
            skLineSegment(sketch, "E8.0.3.9", {"start": v(0.5, 2.8) * mm, "end": v(1, 2.8) * mm});
            skLineSegment(sketch, "E8.0.3.10", {"start": v(6.5, 2.4) * mm, "end": v(6.5, 2.6) * mm});
            skLineSegment(sketch, "E8.0.3.11", {"start": v(2.5, 2.4) * mm, "end": v(2.5, 2.6) * mm});
            skLineSegment(sketch, "E8.0.3.12", {"start": v(17, 2.4) * mm, "end": v(17.5, 2.4) * mm});
            skLineSegment(sketch, "E8.0.3.13", {"start": v(18, 2.4) * mm, "end": v(18.5, 2.4) * mm});
            skLineSegment(sketch, "E8.0.3.14", {"start": v(8.5, 3) * mm, "end": v(9, 3) * mm});
            skLineSegment(sketch, "E8.0.3.15", {"start": v(7, 2.4) * mm, "end": v(7, 2.6) * mm});
            skLineSegment(sketch, "E8.0.3.16", {"start": v(8, 2.6) * mm, "end": v(8.5, 2.6) * mm});
            skLineSegment(sketch, "E8.0.3.17", {"start": v(12, 2.6) * mm, "end": v(12.5, 2.6) * mm});
            skLineSegment(sketch, "E8.0.3.18", {"start": v(12, 2.4) * mm, "end": v(12.5, 2.4) * mm});
            skLineSegment(sketch, "E8.0.3.19", {"start": v(18, 2.6) * mm, "end": v(18.5, 2.6) * mm});
            skLineSegment(sketch, "E8.0.3.20", {"start": v(10.5, 3) * mm, "end": v(11, 3) * mm});
            skLineSegment(sketch, "E8.0.3.21", {"start": v(8.5, 2.8) * mm, "end": v(8.5, 3) * mm});
            skLineSegment(sketch, "E8.0.3.22", {"start": v(13, 2.4) * mm, "end": v(13.5, 2.4) * mm});
            skLineSegment(sketch, "E8.0.3.23", {"start": v(14.5, 2.8) * mm, "end": v(15, 2.8) * mm});
            skLineSegment(sketch, "E8.0.3.24", {"start": v(7, 2.8) * mm, "end": v(7, 3) * mm});
            skLineSegment(sketch, "E8.0.3.25", {"start": v(1, 2.4) * mm, "end": v(1.5, 2.4) * mm});
            skLineSegment(sketch, "E8.0.3.26", {"start": v(5, 2.6) * mm, "end": v(5.5, 2.6) * mm});
            skLineSegment(sketch, "E8.0.3.27", {"start": v(18.5, 3) * mm, "end": v(19, 3) * mm});
            skLineSegment(sketch, "E8.0.3.28", {"start": v(9, 2.8) * mm, "end": v(9, 3) * mm});
            skLineSegment(sketch, "E8.0.3.29", {"start": v(2, 2.6) * mm, "end": v(2.5, 2.6) * mm});
            skLineSegment(sketch, "E8.0.3.30", {"start": v(10, 2.6) * mm, "end": v(10.5, 2.6) * mm});
            skLineSegment(sketch, "E8.0.3.31", {"start": v(14.5, 3) * mm, "end": v(15, 3) * mm});
            skLineSegment(sketch, "E8.0.3.32", {"start": v(9, 2.4) * mm, "end": v(9.5, 2.4) * mm});
            skLineSegment(sketch, "E8.0.3.33", {"start": v(20, 2.8) * mm, "end": v(20, 3) * mm});
            skLineSegment(sketch, "E8.0.3.34", {"start": v(12.5, 2.8) * mm, "end": v(12.5, 3) * mm});
            skLineSegment(sketch, "E8.0.3.35", {"start": v(4.5, 2.8) * mm, "end": v(5, 2.8) * mm});
            skLineSegment(sketch, "E8.0.3.36", {"start": v(8, 2.4) * mm, "end": v(8.5, 2.4) * mm});
            skLineSegment(sketch, "E8.0.3.37", {"start": v(12.5, 2.4) * mm, "end": v(12.5, 2.6) * mm});
            skLineSegment(sketch, "E8.0.3.38", {"start": v(10, 2.4) * mm, "end": v(10.5, 2.4) * mm});
            skLineSegment(sketch, "E8.0.3.39", {"start": v(18.5, 2.8) * mm, "end": v(18.5, 3) * mm});
            skLineSegment(sketch, "E8.0.3.40", {"start": v(18.5, 2.8) * mm, "end": v(19, 2.8) * mm});
            skLineSegment(sketch, "E8.0.3.41", {"start": v(0.5, 3) * mm, "end": v(1, 3) * mm});
            skLineSegment(sketch, "E8.0.3.42", {"start": v(14, 2.6) * mm, "end": v(14.5, 2.6) * mm});
            skLineSegment(sketch, "E8.0.3.43", {"start": v(8.5, 2.4) * mm, "end": v(8.5, 2.6) * mm});
            skLineSegment(sketch, "E8.0.3.44", {"start": v(2.5, 3) * mm, "end": v(3, 3) * mm});
            skLineSegment(sketch, "E8.0.3.45", {"start": v(16.5, 3) * mm, "end": v(17, 3) * mm});
            skLineSegment(sketch, "E8.0.3.46", {"start": v(2, 2.4) * mm, "end": v(2.5, 2.4) * mm});
            skLineSegment(sketch, "E8.0.3.47", {"start": v(7, 2.4) * mm, "end": v(7.5, 2.4) * mm});
            skLineSegment(sketch, "E8.0.3.48", {"start": v(3, 2.4) * mm, "end": v(3, 2.6) * mm});
            skLineSegment(sketch, "E8.0.3.49", {"start": v(16.5, 2.8) * mm, "end": v(17, 2.8) * mm});
            skLineSegment(sketch, "E8.0.3.50", {"start": v(11, 2.4) * mm, "end": v(11.5, 2.4) * mm});
            skLineSegment(sketch, "E8.0.3.51", {"start": v(4, 2.4) * mm, "end": v(4.5, 2.4) * mm});
            skLineSegment(sketch, "E8.0.3.52", {"start": v(16, 2.4) * mm, "end": v(16.5, 2.4) * mm});
            skLineSegment(sketch, "E8.0.3.53", {"start": v(18.5, 2.4) * mm, "end": v(18.5, 2.6) * mm});
            skLineSegment(sketch, "E8.0.3.54", {"start": v(3, 2.8) * mm, "end": v(3, 3) * mm});
            skLineSegment(sketch, "E8.0.3.55", {"start": v(16.5, 2.8) * mm, "end": v(16.5, 3) * mm});
            skLineSegment(sketch, "E8.0.3.56", {"start": v(14.5, 2.4) * mm, "end": v(14.5, 2.6) * mm});
            skLineSegment(sketch, "E8.0.3.57", {"start": v(4.5, 2.8) * mm, "end": v(4.5, 3) * mm});
            skLineSegment(sketch, "E8.0.3.58", {"start": v(16, 2.6) * mm, "end": v(16.5, 2.6) * mm});
            skLineSegment(sketch, "E8.0.3.59", {"start": v(8.5, 2.8) * mm, "end": v(9, 2.8) * mm});
            skLineSegment(sketch, "E8.0.3.60", {"start": v(5, 2.4) * mm, "end": v(5.5, 2.4) * mm});
            skLineSegment(sketch, "E8.0.3.61", {"start": v(3, 2.4) * mm, "end": v(3.5, 2.4) * mm});
            skLineSegment(sketch, "E8.0.3.62", {"start": v(9, 2.4) * mm, "end": v(9, 2.6) * mm});
            skLineSegment(sketch, "E8.0.3.63", {"start": v(9, 2.6) * mm, "end": v(9.5, 2.6) * mm});
            skLineSegment(sketch, "E8.0.3.64", {"start": v(4, 2.6) * mm, "end": v(4.5, 2.6) * mm});
            skLineSegment(sketch, "E8.0.3.65", {"start": v(19.5, 2.8) * mm, "end": v(20, 2.8) * mm});
            skLineSegment(sketch, "E8.0.3.66", {"start": v(6.5, 2.8) * mm, "end": v(7, 2.8) * mm});
            skLineSegment(sketch, "E8.0.3.67", {"start": v(6, 2.6) * mm, "end": v(6.5, 2.6) * mm});
            skLineSegment(sketch, "E8.0.3.68", {"start": v(6, 2.4) * mm, "end": v(6.5, 2.4) * mm});
            skLineSegment(sketch, "E8.0.3.69", {"start": v(5, 2.4) * mm, "end": v(5, 2.6) * mm});
            skLineSegment(sketch, "E8.0.3.70", {"start": v(19.5, 2.4) * mm, "end": v(19.5, 2.6) * mm});
            skLineSegment(sketch, "E8.0.3.72", {"start": v(16.5, 2.4) * mm, "end": v(16.5, 2.6) * mm});
            skLineSegment(sketch, "E8.0.3.73", {"start": v(12.5, 3) * mm, "end": v(13, 3) * mm});
            skLineSegment(sketch, "E8.0.3.74", {"start": v(6.5, 3) * mm, "end": v(7, 3) * mm});
            skLineSegment(sketch, "E8.0.3.75", {"start": v(2.5, 2.8) * mm, "end": v(3, 2.8) * mm});
            skLineSegment(sketch, "E8.0.3.76", {"start": v(12.5, 2.8) * mm, "end": v(13, 2.8) * mm});
            skLineSegment(sketch, "E8.0.3.77", {"start": v(5, 2.8) * mm, "end": v(5, 3) * mm});
            skLineSegment(sketch, "E8.0.3.78", {"start": v(14, 2.4) * mm, "end": v(14.5, 2.4) * mm});
            skLineSegment(sketch, "E8.0.3.79", {"start": v(0.5, 2.8) * mm, "end": v(0.5, 3) * mm});
            skLineSegment(sketch, "E8.0.3.80", {"start": v(10.5, 2.4) * mm, "end": v(10.5, 2.6) * mm});
            skLineSegment(sketch, "E8.0.3.81", {"start": v(1, 2.4) * mm, "end": v(1, 2.6) * mm});
            skLineSegment(sketch, "E8.0.3.82", {"start": v(17, 2.6) * mm, "end": v(17.5, 2.6) * mm});
            skLineSegment(sketch, "E8.0.3.83", {"start": v(19, 2.8) * mm, "end": v(19, 3) * mm});
            skLineSegment(sketch, "E8.0.3.84", {"start": v(1.5, 2.4) * mm, "end": v(1.5, 2.6) * mm});
            skLineSegment(sketch, "E8.0.3.85", {"start": v(19, 2.6) * mm, "end": v(19.5, 2.6) * mm});
            skLineSegment(sketch, "E8.0.3.86", {"start": v(11, 2.6) * mm, "end": v(11.5, 2.6) * mm});
            skLineSegment(sketch, "E8.0.3.87", {"start": v(15.5, 2.4) * mm, "end": v(15.5, 2.6) * mm});
            skLineSegment(sketch, "E8.0.3.88", {"start": v(3.5, 2.4) * mm, "end": v(3.5, 2.6) * mm});
            skLineSegment(sketch, "E8.0.3.89", {"start": v(19.5, 3) * mm, "end": v(20, 3) * mm});
            skLineSegment(sketch, "E8.0.3.90", {"start": v(15, 2.4) * mm, "end": v(15, 2.6) * mm});
            skLineSegment(sketch, "E8.0.3.91", {"start": v(19, 2.4) * mm, "end": v(19, 2.6) * mm});
            skLineSegment(sketch, "E8.0.3.92", {"start": v(16, 2.4) * mm, "end": v(16, 2.6) * mm});
            skLineSegment(sketch, "E8.0.3.93", {"start": v(6.5, 2.8) * mm, "end": v(6.5, 3) * mm});
            skLineSegment(sketch, "E8.0.3.94", {"start": v(5.5, 2.4) * mm, "end": v(5.5, 2.6) * mm});
            skLineSegment(sketch, "E8.0.3.95", {"start": v(14.5, 2.8) * mm, "end": v(14.5, 3) * mm});
            skLineSegment(sketch, "E8.0.3.96", {"start": v(18, 2.4) * mm, "end": v(18, 2.6) * mm});
            skLineSegment(sketch, "E8.0.3.97", {"start": v(19, 2.4) * mm, "end": v(19.5, 2.4) * mm});
            skLineSegment(sketch, "E8.0.3.98", {"start": v(10.5, 2.8) * mm, "end": v(10.5, 3) * mm});
            skLineSegment(sketch, "E8.0.3.99", {"start": v(7.5, 2.4) * mm, "end": v(7.5, 2.6) * mm});
            skLineSegment(sketch, "E8.0.3.100", {"start": v(9.5, 2.4) * mm, "end": v(9.5, 2.6) * mm});
            skLineSegment(sketch, "E8.0.3.101", {"start": v(17.5, 2.4) * mm, "end": v(17.5, 2.6) * mm});
            skLineSegment(sketch, "E8.0.3.102", {"start": v(17, 2.4) * mm, "end": v(17, 2.6) * mm});
            skLineSegment(sketch, "E8.0.3.103", {"start": v(11, 2.8) * mm, "end": v(11, 3) * mm});
            skLineSegment(sketch, "E8.0.3.104", {"start": v(15, 2.4) * mm, "end": v(15.5, 2.4) * mm});
            skLineSegment(sketch, "E8.0.3.105", {"start": v(11.5, 2.4) * mm, "end": v(11.5, 2.6) * mm});
            skLineSegment(sketch, "E8.0.3.106", {"start": v(1.5, 2.8) * mm, "end": v(1.5, 3) * mm});
            skLineSegment(sketch, "E8.0.3.107", {"start": v(2.5, 2.8) * mm, "end": v(2.5, 3) * mm});
            skLineSegment(sketch, "E8.0.3.108", {"start": v(15, 2.8) * mm, "end": v(15, 3) * mm});
            skLineSegment(sketch, "E8.0.3.109", {"start": v(13, 2.4) * mm, "end": v(13, 2.6) * mm});
            skLineSegment(sketch, "E8.0.3.110", {"start": v(13, 2.6) * mm, "end": v(13.5, 2.6) * mm});
            skLineSegment(sketch, "E8.0.3.111", {"start": v(13.5, 2.4) * mm, "end": v(13.5, 2.6) * mm});
            skLineSegment(sketch, "E8.0.3.112", {"start": v(11, 2.4) * mm, "end": v(11, 2.6) * mm});
            skLineSegment(sketch, "E8.0.3.113", {"start": v(7.5, 3) * mm, "end": v(8, 3) * mm});
            skLineSegment(sketch, "E8.0.3.114", {"start": v(8, 2.8) * mm, "end": v(8, 3) * mm});
            skLineSegment(sketch, "E8.0.3.115", {"start": v(17.5, 2.8) * mm, "end": v(17.5, 3) * mm});
            skLineSegment(sketch, "E8.0.3.116", {"start": v(17.5, 3) * mm, "end": v(18, 3) * mm});
            skLineSegment(sketch, "E8.0.3.117", {"start": v(18, 2.8) * mm, "end": v(18, 3) * mm});
            skLineSegment(sketch, "E8.0.3.118", {"start": v(17.5, 2.8) * mm, "end": v(18, 2.8) * mm});
            skLineSegment(sketch, "E8.0.3.119", {"start": v(5.5, 2.8) * mm, "end": v(5.5, 3) * mm});
            skLineSegment(sketch, "E8.0.3.120", {"start": v(13.5, 2.8) * mm, "end": v(13.5, 3) * mm});
            skLineSegment(sketch, "E8.0.3.121", {"start": v(9.5, 2.8) * mm, "end": v(10, 2.8) * mm});
            skLineSegment(sketch, "E8.0.3.122", {"start": v(3.5, 2.8) * mm, "end": v(4, 2.8) * mm});
            skLineSegment(sketch, "E8.0.3.123", {"start": v(7.5, 2.8) * mm, "end": v(7.5, 3) * mm});
            skLineSegment(sketch, "E8.0.3.124", {"start": v(9.5, 3) * mm, "end": v(10, 3) * mm});
            skLineSegment(sketch, "E8.0.3.125", {"start": v(15.5, 2.8) * mm, "end": v(16, 2.8) * mm});
            skLineSegment(sketch, "E8.0.3.126", {"start": v(15.5, 2.8) * mm, "end": v(15.5, 3) * mm});
            skLineSegment(sketch, "E8.0.3.127", {"start": v(16, 2.8) * mm, "end": v(16, 3) * mm});
            skLineSegment(sketch, "E8.0.3.128", {"start": v(11.5, 2.8) * mm, "end": v(11.5, 3) * mm});
            skLineSegment(sketch, "E8.0.3.129", {"start": v(2, 2.8) * mm, "end": v(2, 3) * mm});
            skLineSegment(sketch, "E8.0.3.130", {"start": v(1.5, 2.8) * mm, "end": v(2, 2.8) * mm});
            skLineSegment(sketch, "E8.0.3.131", {"start": v(7.5, 2.8) * mm, "end": v(8, 2.8) * mm});
            skLineSegment(sketch, "E8.0.3.132", {"start": v(10, 2.4) * mm, "end": v(10, 2.6) * mm});
            skLineSegment(sketch, "E8.0.3.133", {"start": v(8, 2.4) * mm, "end": v(8, 2.6) * mm});
            skLineSegment(sketch, "E8.0.3.134", {"start": v(19.5, 2.8) * mm, "end": v(19.5, 3) * mm});
            skLineSegment(sketch, "E8.0.3.135", {"start": v(6, 2.8) * mm, "end": v(6, 3) * mm});
            skLineSegment(sketch, "E8.0.3.136", {"start": v(12, 2.4) * mm, "end": v(12, 2.6) * mm});
            skLineSegment(sketch, "E8.0.3.137", {"start": v(9.5, 2.8) * mm, "end": v(9.5, 3) * mm});
            skLineSegment(sketch, "E8.0.3.138", {"start": v(3.5, 2.8) * mm, "end": v(3.5, 3) * mm});
            skLineSegment(sketch, "E8.0.3.139", {"start": v(15.5, 3) * mm, "end": v(16, 3) * mm});
            skLineSegment(sketch, "E8.0.3.140", {"start": v(4, 2.4) * mm, "end": v(4, 2.6) * mm});
            skLineSegment(sketch, "E8.0.3.141", {"start": v(2, 2.4) * mm, "end": v(2, 2.6) * mm});
            skLineSegment(sketch, "E8.0.3.142", {"start": v(13.5, 3) * mm, "end": v(14, 3) * mm});
            skLineSegment(sketch, "E8.0.3.143", {"start": v(11.5, 3) * mm, "end": v(12, 3) * mm});
            skLineSegment(sketch, "E8.0.3.144", {"start": v(5.5, 3) * mm, "end": v(6, 3) * mm});
            skLineSegment(sketch, "E8.0.3.145", {"start": v(14, 2.4) * mm, "end": v(14, 2.6) * mm});
            skLineSegment(sketch, "E8.0.3.146", {"start": v(15, 2.6) * mm, "end": v(15.5, 2.6) * mm});
            skLineSegment(sketch, "E8.0.3.147", {"start": v(4, 2.8) * mm, "end": v(4, 3) * mm});
            skLineSegment(sketch, "E8.0.3.148", {"start": v(1.5, 3) * mm, "end": v(2, 3) * mm});
            skLineSegment(sketch, "E8.0.3.149", {"start": v(11.5, 2.8) * mm, "end": v(12, 2.8) * mm});
            skLineSegment(sketch, "E8.0.3.150", {"start": v(6, 2.4) * mm, "end": v(6, 2.6) * mm});
            skLineSegment(sketch, "E8.0.3.151", {"start": v(12, 2.8) * mm, "end": v(12, 3) * mm});
            skLineSegment(sketch, "E8.0.3.152", {"start": v(13.5, 2.8) * mm, "end": v(14, 2.8) * mm});
            skLineSegment(sketch, "E8.0.3.153", {"start": v(5.5, 2.8) * mm, "end": v(6, 2.8) * mm});
            skLineSegment(sketch, "E8.0.3.154", {"start": v(10, 2.8) * mm, "end": v(10, 3) * mm});
            skLineSegment(sketch, "E8.0.3.155", {"start": v(3.5, 3) * mm, "end": v(4, 3) * mm});
            skLineSegment(sketch, "E8.0.3.156", {"start": v(14, 2.8) * mm, "end": v(14, 3) * mm});
            skLineSegment(sketch, "E8.0.4.0", {"start": v(3, 3.4) * mm, "end": v(3.5, 3.4) * mm});
            skLineSegment(sketch, "E8.0.4.1", {"start": v(1, 3.4) * mm, "end": v(1.5, 3.4) * mm});
            skLineSegment(sketch, "E8.0.4.2", {"start": v(17, 3.6) * mm, "end": v(17, 3.8) * mm});
            skLineSegment(sketch, "E8.0.4.3", {"start": v(13, 3.6) * mm, "end": v(13, 3.8) * mm});
            skLineSegment(sketch, "E8.0.4.4", {"start": v(4.5, 3.2) * mm, "end": v(4.5, 3.4) * mm});
            skLineSegment(sketch, "E8.0.4.5", {"start": v(10.5, 3.6) * mm, "end": v(11, 3.6) * mm});
            skLineSegment(sketch, "E8.0.4.6", {"start": v(1, 3.6) * mm, "end": v(1, 3.8) * mm});
            skLineSegment(sketch, "E8.0.4.7", {"start": v(4.5, 3.8) * mm, "end": v(5, 3.8) * mm});
            skLineSegment(sketch, "E8.0.4.8", {"start": v(7, 3.4) * mm, "end": v(7.5, 3.4) * mm});
            skLineSegment(sketch, "E8.0.4.9", {"start": v(0.5, 3.6) * mm, "end": v(1, 3.6) * mm});
            skLineSegment(sketch, "E8.0.4.10", {"start": v(6.5, 3.2) * mm, "end": v(6.5, 3.4) * mm});
            skLineSegment(sketch, "E8.0.4.11", {"start": v(2.5, 3.2) * mm, "end": v(2.5, 3.4) * mm});
            skLineSegment(sketch, "E8.0.4.12", {"start": v(17, 3.2) * mm, "end": v(17.5, 3.2) * mm});
            skLineSegment(sketch, "E8.0.4.13", {"start": v(18, 3.2) * mm, "end": v(18.5, 3.2) * mm});
            skLineSegment(sketch, "E8.0.4.14", {"start": v(8.5, 3.8) * mm, "end": v(9, 3.8) * mm});
            skLineSegment(sketch, "E8.0.4.15", {"start": v(7, 3.2) * mm, "end": v(7, 3.4) * mm});
            skLineSegment(sketch, "E8.0.4.16", {"start": v(8, 3.4) * mm, "end": v(8.5, 3.4) * mm});
            skLineSegment(sketch, "E8.0.4.17", {"start": v(12, 3.4) * mm, "end": v(12.5, 3.4) * mm});
            skLineSegment(sketch, "E8.0.4.18", {"start": v(12, 3.2) * mm, "end": v(12.5, 3.2) * mm});
            skLineSegment(sketch, "E8.0.4.19", {"start": v(18, 3.4) * mm, "end": v(18.5, 3.4) * mm});
            skLineSegment(sketch, "E8.0.4.20", {"start": v(10.5, 3.8) * mm, "end": v(11, 3.8) * mm});
            skLineSegment(sketch, "E8.0.4.21", {"start": v(8.5, 3.6) * mm, "end": v(8.5, 3.8) * mm});
            skLineSegment(sketch, "E8.0.4.22", {"start": v(13, 3.2) * mm, "end": v(13.5, 3.2) * mm});
            skLineSegment(sketch, "E8.0.4.23", {"start": v(14.5, 3.6) * mm, "end": v(15, 3.6) * mm});
            skLineSegment(sketch, "E8.0.4.24", {"start": v(7, 3.6) * mm, "end": v(7, 3.8) * mm});
            skLineSegment(sketch, "E8.0.4.25", {"start": v(1, 3.2) * mm, "end": v(1.5, 3.2) * mm});
            skLineSegment(sketch, "E8.0.4.26", {"start": v(5, 3.4) * mm, "end": v(5.5, 3.4) * mm});
            skLineSegment(sketch, "E8.0.4.27", {"start": v(18.5, 3.8) * mm, "end": v(19, 3.8) * mm});
            skLineSegment(sketch, "E8.0.4.28", {"start": v(9, 3.6) * mm, "end": v(9, 3.8) * mm});
            skLineSegment(sketch, "E8.0.4.29", {"start": v(2, 3.4) * mm, "end": v(2.5, 3.4) * mm});
            skLineSegment(sketch, "E8.0.4.30", {"start": v(10, 3.4) * mm, "end": v(10.5, 3.4) * mm});
            skLineSegment(sketch, "E8.0.4.31", {"start": v(14.5, 3.8) * mm, "end": v(15, 3.8) * mm});
            skLineSegment(sketch, "E8.0.4.32", {"start": v(9, 3.2) * mm, "end": v(9.5, 3.2) * mm});
            skLineSegment(sketch, "E8.0.4.33", {"start": v(20, 3.6) * mm, "end": v(20, 3.8) * mm});
            skLineSegment(sketch, "E8.0.4.34", {"start": v(12.5, 3.6) * mm, "end": v(12.5, 3.8) * mm});
            skLineSegment(sketch, "E8.0.4.35", {"start": v(4.5, 3.6) * mm, "end": v(5, 3.6) * mm});
            skLineSegment(sketch, "E8.0.4.36", {"start": v(8, 3.2) * mm, "end": v(8.5, 3.2) * mm});
            skLineSegment(sketch, "E8.0.4.37", {"start": v(12.5, 3.2) * mm, "end": v(12.5, 3.4) * mm});
            skLineSegment(sketch, "E8.0.4.38", {"start": v(10, 3.2) * mm, "end": v(10.5, 3.2) * mm});
            skLineSegment(sketch, "E8.0.4.39", {"start": v(18.5, 3.6) * mm, "end": v(18.5, 3.8) * mm});
            skLineSegment(sketch, "E8.0.4.40", {"start": v(18.5, 3.6) * mm, "end": v(19, 3.6) * mm});
            skLineSegment(sketch, "E8.0.4.41", {"start": v(0.5, 3.8) * mm, "end": v(1, 3.8) * mm});
            skLineSegment(sketch, "E8.0.4.42", {"start": v(14, 3.4) * mm, "end": v(14.5, 3.4) * mm});
            skLineSegment(sketch, "E8.0.4.43", {"start": v(8.5, 3.2) * mm, "end": v(8.5, 3.4) * mm});
            skLineSegment(sketch, "E8.0.4.44", {"start": v(2.5, 3.8) * mm, "end": v(3, 3.8) * mm});
            skLineSegment(sketch, "E8.0.4.45", {"start": v(16.5, 3.8) * mm, "end": v(17, 3.8) * mm});
            skLineSegment(sketch, "E8.0.4.46", {"start": v(2, 3.2) * mm, "end": v(2.5, 3.2) * mm});
            skLineSegment(sketch, "E8.0.4.47", {"start": v(7, 3.2) * mm, "end": v(7.5, 3.2) * mm});
            skLineSegment(sketch, "E8.0.4.48", {"start": v(3, 3.2) * mm, "end": v(3, 3.4) * mm});
            skLineSegment(sketch, "E8.0.4.49", {"start": v(16.5, 3.6) * mm, "end": v(17, 3.6) * mm});
            skLineSegment(sketch, "E8.0.4.50", {"start": v(11, 3.2) * mm, "end": v(11.5, 3.2) * mm});
            skLineSegment(sketch, "E8.0.4.51", {"start": v(4, 3.2) * mm, "end": v(4.5, 3.2) * mm});
            skLineSegment(sketch, "E8.0.4.52", {"start": v(16, 3.2) * mm, "end": v(16.5, 3.2) * mm});
            skLineSegment(sketch, "E8.0.4.53", {"start": v(18.5, 3.2) * mm, "end": v(18.5, 3.4) * mm});
            skLineSegment(sketch, "E8.0.4.54", {"start": v(3, 3.6) * mm, "end": v(3, 3.8) * mm});
            skLineSegment(sketch, "E8.0.4.55", {"start": v(16.5, 3.6) * mm, "end": v(16.5, 3.8) * mm});
            skLineSegment(sketch, "E8.0.4.56", {"start": v(14.5, 3.2) * mm, "end": v(14.5, 3.4) * mm});
            skLineSegment(sketch, "E8.0.4.57", {"start": v(4.5, 3.6) * mm, "end": v(4.5, 3.8) * mm});
            skLineSegment(sketch, "E8.0.4.58", {"start": v(16, 3.4) * mm, "end": v(16.5, 3.4) * mm});
            skLineSegment(sketch, "E8.0.4.59", {"start": v(8.5, 3.6) * mm, "end": v(9, 3.6) * mm});
            skLineSegment(sketch, "E8.0.4.60", {"start": v(5, 3.2) * mm, "end": v(5.5, 3.2) * mm});
            skLineSegment(sketch, "E8.0.4.61", {"start": v(3, 3.2) * mm, "end": v(3.5, 3.2) * mm});
            skLineSegment(sketch, "E8.0.4.62", {"start": v(9, 3.2) * mm, "end": v(9, 3.4) * mm});
            skLineSegment(sketch, "E8.0.4.63", {"start": v(9, 3.4) * mm, "end": v(9.5, 3.4) * mm});
            skLineSegment(sketch, "E8.0.4.64", {"start": v(4, 3.4) * mm, "end": v(4.5, 3.4) * mm});
            skLineSegment(sketch, "E8.0.4.65", {"start": v(19.5, 3.6) * mm, "end": v(20, 3.6) * mm});
            skLineSegment(sketch, "E8.0.4.66", {"start": v(6.5, 3.6) * mm, "end": v(7, 3.6) * mm});
            skLineSegment(sketch, "E8.0.4.67", {"start": v(6, 3.4) * mm, "end": v(6.5, 3.4) * mm});
            skLineSegment(sketch, "E8.0.4.68", {"start": v(6, 3.2) * mm, "end": v(6.5, 3.2) * mm});
            skLineSegment(sketch, "E8.0.4.69", {"start": v(5, 3.2) * mm, "end": v(5, 3.4) * mm});
            skLineSegment(sketch, "E8.0.4.70", {"start": v(19.5, 3.2) * mm, "end": v(19.5, 3.4) * mm});
            skLineSegment(sketch, "E8.0.4.72", {"start": v(16.5, 3.2) * mm, "end": v(16.5, 3.4) * mm});
            skLineSegment(sketch, "E8.0.4.73", {"start": v(12.5, 3.8) * mm, "end": v(13, 3.8) * mm});
            skLineSegment(sketch, "E8.0.4.74", {"start": v(6.5, 3.8) * mm, "end": v(7, 3.8) * mm});
            skLineSegment(sketch, "E8.0.4.75", {"start": v(2.5, 3.6) * mm, "end": v(3, 3.6) * mm});
            skLineSegment(sketch, "E8.0.4.76", {"start": v(12.5, 3.6) * mm, "end": v(13, 3.6) * mm});
            skLineSegment(sketch, "E8.0.4.77", {"start": v(5, 3.6) * mm, "end": v(5, 3.8) * mm});
            skLineSegment(sketch, "E8.0.4.78", {"start": v(14, 3.2) * mm, "end": v(14.5, 3.2) * mm});
            skLineSegment(sketch, "E8.0.4.79", {"start": v(0.5, 3.6) * mm, "end": v(0.5, 3.8) * mm});
            skLineSegment(sketch, "E8.0.4.80", {"start": v(10.5, 3.2) * mm, "end": v(10.5, 3.4) * mm});
            skLineSegment(sketch, "E8.0.4.81", {"start": v(1, 3.2) * mm, "end": v(1, 3.4) * mm});
            skLineSegment(sketch, "E8.0.4.82", {"start": v(17, 3.4) * mm, "end": v(17.5, 3.4) * mm});
            skLineSegment(sketch, "E8.0.4.83", {"start": v(19, 3.6) * mm, "end": v(19, 3.8) * mm});
            skLineSegment(sketch, "E8.0.4.84", {"start": v(1.5, 3.2) * mm, "end": v(1.5, 3.4) * mm});
            skLineSegment(sketch, "E8.0.4.85", {"start": v(19, 3.4) * mm, "end": v(19.5, 3.4) * mm});
            skLineSegment(sketch, "E8.0.4.86", {"start": v(11, 3.4) * mm, "end": v(11.5, 3.4) * mm});
            skLineSegment(sketch, "E8.0.4.87", {"start": v(15.5, 3.2) * mm, "end": v(15.5, 3.4) * mm});
            skLineSegment(sketch, "E8.0.4.88", {"start": v(3.5, 3.2) * mm, "end": v(3.5, 3.4) * mm});
            skLineSegment(sketch, "E8.0.4.89", {"start": v(19.5, 3.8) * mm, "end": v(20, 3.8) * mm});
            skLineSegment(sketch, "E8.0.4.90", {"start": v(15, 3.2) * mm, "end": v(15, 3.4) * mm});
            skLineSegment(sketch, "E8.0.4.91", {"start": v(19, 3.2) * mm, "end": v(19, 3.4) * mm});
            skLineSegment(sketch, "E8.0.4.92", {"start": v(16, 3.2) * mm, "end": v(16, 3.4) * mm});
            skLineSegment(sketch, "E8.0.4.93", {"start": v(6.5, 3.6) * mm, "end": v(6.5, 3.8) * mm});
            skLineSegment(sketch, "E8.0.4.94", {"start": v(5.5, 3.2) * mm, "end": v(5.5, 3.4) * mm});
            skLineSegment(sketch, "E8.0.4.95", {"start": v(14.5, 3.6) * mm, "end": v(14.5, 3.8) * mm});
            skLineSegment(sketch, "E8.0.4.96", {"start": v(18, 3.2) * mm, "end": v(18, 3.4) * mm});
            skLineSegment(sketch, "E8.0.4.97", {"start": v(19, 3.2) * mm, "end": v(19.5, 3.2) * mm});
            skLineSegment(sketch, "E8.0.4.98", {"start": v(10.5, 3.6) * mm, "end": v(10.5, 3.8) * mm});
            skLineSegment(sketch, "E8.0.4.99", {"start": v(7.5, 3.2) * mm, "end": v(7.5, 3.4) * mm});
            skLineSegment(sketch, "E8.0.4.100", {"start": v(9.5, 3.2) * mm, "end": v(9.5, 3.4) * mm});
            skLineSegment(sketch, "E8.0.4.101", {"start": v(17.5, 3.2) * mm, "end": v(17.5, 3.4) * mm});
            skLineSegment(sketch, "E8.0.4.102", {"start": v(17, 3.2) * mm, "end": v(17, 3.4) * mm});
            skLineSegment(sketch, "E8.0.4.103", {"start": v(11, 3.6) * mm, "end": v(11, 3.8) * mm});
            skLineSegment(sketch, "E8.0.4.104", {"start": v(15, 3.2) * mm, "end": v(15.5, 3.2) * mm});
            skLineSegment(sketch, "E8.0.4.105", {"start": v(11.5, 3.2) * mm, "end": v(11.5, 3.4) * mm});
            skLineSegment(sketch, "E8.0.4.106", {"start": v(1.5, 3.6) * mm, "end": v(1.5, 3.8) * mm});
            skLineSegment(sketch, "E8.0.4.107", {"start": v(2.5, 3.6) * mm, "end": v(2.5, 3.8) * mm});
            skLineSegment(sketch, "E8.0.4.108", {"start": v(15, 3.6) * mm, "end": v(15, 3.8) * mm});
            skLineSegment(sketch, "E8.0.4.109", {"start": v(13, 3.2) * mm, "end": v(13, 3.4) * mm});
            skLineSegment(sketch, "E8.0.4.110", {"start": v(13, 3.4) * mm, "end": v(13.5, 3.4) * mm});
            skLineSegment(sketch, "E8.0.4.111", {"start": v(13.5, 3.2) * mm, "end": v(13.5, 3.4) * mm});
            skLineSegment(sketch, "E8.0.4.112", {"start": v(11, 3.2) * mm, "end": v(11, 3.4) * mm});
            skLineSegment(sketch, "E8.0.4.113", {"start": v(7.5, 3.8) * mm, "end": v(8, 3.8) * mm});
            skLineSegment(sketch, "E8.0.4.114", {"start": v(8, 3.6) * mm, "end": v(8, 3.8) * mm});
            skLineSegment(sketch, "E8.0.4.115", {"start": v(17.5, 3.6) * mm, "end": v(17.5, 3.8) * mm});
            skLineSegment(sketch, "E8.0.4.116", {"start": v(17.5, 3.8) * mm, "end": v(18, 3.8) * mm});
            skLineSegment(sketch, "E8.0.4.117", {"start": v(18, 3.6) * mm, "end": v(18, 3.8) * mm});
            skLineSegment(sketch, "E8.0.4.118", {"start": v(17.5, 3.6) * mm, "end": v(18, 3.6) * mm});
            skLineSegment(sketch, "E8.0.4.119", {"start": v(5.5, 3.6) * mm, "end": v(5.5, 3.8) * mm});
            skLineSegment(sketch, "E8.0.4.120", {"start": v(13.5, 3.6) * mm, "end": v(13.5, 3.8) * mm});
            skLineSegment(sketch, "E8.0.4.121", {"start": v(9.5, 3.6) * mm, "end": v(10, 3.6) * mm});
            skLineSegment(sketch, "E8.0.4.122", {"start": v(3.5, 3.6) * mm, "end": v(4, 3.6) * mm});
            skLineSegment(sketch, "E8.0.4.123", {"start": v(7.5, 3.6) * mm, "end": v(7.5, 3.8) * mm});
            skLineSegment(sketch, "E8.0.4.124", {"start": v(9.5, 3.8) * mm, "end": v(10, 3.8) * mm});
            skLineSegment(sketch, "E8.0.4.125", {"start": v(15.5, 3.6) * mm, "end": v(16, 3.6) * mm});
            skLineSegment(sketch, "E8.0.4.126", {"start": v(15.5, 3.6) * mm, "end": v(15.5, 3.8) * mm});
            skLineSegment(sketch, "E8.0.4.127", {"start": v(16, 3.6) * mm, "end": v(16, 3.8) * mm});
            skLineSegment(sketch, "E8.0.4.128", {"start": v(11.5, 3.6) * mm, "end": v(11.5, 3.8) * mm});
            skLineSegment(sketch, "E8.0.4.129", {"start": v(2, 3.6) * mm, "end": v(2, 3.8) * mm});
            skLineSegment(sketch, "E8.0.4.130", {"start": v(1.5, 3.6) * mm, "end": v(2, 3.6) * mm});
            skLineSegment(sketch, "E8.0.4.131", {"start": v(7.5, 3.6) * mm, "end": v(8, 3.6) * mm});
            skLineSegment(sketch, "E8.0.4.132", {"start": v(10, 3.2) * mm, "end": v(10, 3.4) * mm});
            skLineSegment(sketch, "E8.0.4.133", {"start": v(8, 3.2) * mm, "end": v(8, 3.4) * mm});
            skLineSegment(sketch, "E8.0.4.134", {"start": v(19.5, 3.6) * mm, "end": v(19.5, 3.8) * mm});
            skLineSegment(sketch, "E8.0.4.135", {"start": v(6, 3.6) * mm, "end": v(6, 3.8) * mm});
            skLineSegment(sketch, "E8.0.4.136", {"start": v(12, 3.2) * mm, "end": v(12, 3.4) * mm});
            skLineSegment(sketch, "E8.0.4.137", {"start": v(9.5, 3.6) * mm, "end": v(9.5, 3.8) * mm});
            skLineSegment(sketch, "E8.0.4.138", {"start": v(3.5, 3.6) * mm, "end": v(3.5, 3.8) * mm});
            skLineSegment(sketch, "E8.0.4.139", {"start": v(15.5, 3.8) * mm, "end": v(16, 3.8) * mm});
            skLineSegment(sketch, "E8.0.4.140", {"start": v(4, 3.2) * mm, "end": v(4, 3.4) * mm});
            skLineSegment(sketch, "E8.0.4.141", {"start": v(2, 3.2) * mm, "end": v(2, 3.4) * mm});
            skLineSegment(sketch, "E8.0.4.142", {"start": v(13.5, 3.8) * mm, "end": v(14, 3.8) * mm});
            skLineSegment(sketch, "E8.0.4.143", {"start": v(11.5, 3.8) * mm, "end": v(12, 3.8) * mm});
            skLineSegment(sketch, "E8.0.4.144", {"start": v(5.5, 3.8) * mm, "end": v(6, 3.8) * mm});
            skLineSegment(sketch, "E8.0.4.145", {"start": v(14, 3.2) * mm, "end": v(14, 3.4) * mm});
            skLineSegment(sketch, "E8.0.4.146", {"start": v(15, 3.4) * mm, "end": v(15.5, 3.4) * mm});
            skLineSegment(sketch, "E8.0.4.147", {"start": v(4, 3.6) * mm, "end": v(4, 3.8) * mm});
            skLineSegment(sketch, "E8.0.4.148", {"start": v(1.5, 3.8) * mm, "end": v(2, 3.8) * mm});
            skLineSegment(sketch, "E8.0.4.149", {"start": v(11.5, 3.6) * mm, "end": v(12, 3.6) * mm});
            skLineSegment(sketch, "E8.0.4.150", {"start": v(6, 3.2) * mm, "end": v(6, 3.4) * mm});
            skLineSegment(sketch, "E8.0.4.151", {"start": v(12, 3.6) * mm, "end": v(12, 3.8) * mm});
            skLineSegment(sketch, "E8.0.4.152", {"start": v(13.5, 3.6) * mm, "end": v(14, 3.6) * mm});
            skLineSegment(sketch, "E8.0.4.153", {"start": v(5.5, 3.6) * mm, "end": v(6, 3.6) * mm});
            skLineSegment(sketch, "E8.0.4.154", {"start": v(10, 3.6) * mm, "end": v(10, 3.8) * mm});
            skLineSegment(sketch, "E8.0.4.155", {"start": v(3.5, 3.8) * mm, "end": v(4, 3.8) * mm});
            skLineSegment(sketch, "E8.0.4.156", {"start": v(14, 3.6) * mm, "end": v(14, 3.8) * mm});
            skLineSegment(sketch, "E8.0.5.0", {"start": v(3, 4.2) * mm, "end": v(3.5, 4.2) * mm});
            skLineSegment(sketch, "E8.0.5.1", {"start": v(1, 4.2) * mm, "end": v(1.5, 4.2) * mm});
            skLineSegment(sketch, "E8.0.5.2", {"start": v(17, 4.4) * mm, "end": v(17, 4.6) * mm});
            skLineSegment(sketch, "E8.0.5.3", {"start": v(13, 4.4) * mm, "end": v(13, 4.6) * mm});
            skLineSegment(sketch, "E8.0.5.4", {"start": v(4.5, 4) * mm, "end": v(4.5, 4.2) * mm});
            skLineSegment(sketch, "E8.0.5.5", {"start": v(10.5, 4.4) * mm, "end": v(11, 4.4) * mm});
            skLineSegment(sketch, "E8.0.5.6", {"start": v(1, 4.4) * mm, "end": v(1, 4.6) * mm});
            skLineSegment(sketch, "E8.0.5.7", {"start": v(4.5, 4.6) * mm, "end": v(5, 4.6) * mm});
            skLineSegment(sketch, "E8.0.5.8", {"start": v(7, 4.2) * mm, "end": v(7.5, 4.2) * mm});
            skLineSegment(sketch, "E8.0.5.9", {"start": v(0.5, 4.4) * mm, "end": v(1, 4.4) * mm});
            skLineSegment(sketch, "E8.0.5.10", {"start": v(6.5, 4) * mm, "end": v(6.5, 4.2) * mm});
            skLineSegment(sketch, "E8.0.5.11", {"start": v(2.5, 4) * mm, "end": v(2.5, 4.2) * mm});
            skLineSegment(sketch, "E8.0.5.12", {"start": v(17, 4) * mm, "end": v(17.5, 4) * mm});
            skLineSegment(sketch, "E8.0.5.13", {"start": v(18, 4) * mm, "end": v(18.5, 4) * mm});
            skLineSegment(sketch, "E8.0.5.14", {"start": v(8.5, 4.6) * mm, "end": v(9, 4.6) * mm});
            skLineSegment(sketch, "E8.0.5.15", {"start": v(7, 4) * mm, "end": v(7, 4.2) * mm});
            skLineSegment(sketch, "E8.0.5.16", {"start": v(8, 4.2) * mm, "end": v(8.5, 4.2) * mm});
            skLineSegment(sketch, "E8.0.5.17", {"start": v(12, 4.2) * mm, "end": v(12.5, 4.2) * mm});
            skLineSegment(sketch, "E8.0.5.18", {"start": v(12, 4) * mm, "end": v(12.5, 4) * mm});
            skLineSegment(sketch, "E8.0.5.19", {"start": v(18, 4.2) * mm, "end": v(18.5, 4.2) * mm});
            skLineSegment(sketch, "E8.0.5.20", {"start": v(10.5, 4.6) * mm, "end": v(11, 4.6) * mm});
            skLineSegment(sketch, "E8.0.5.21", {"start": v(8.5, 4.4) * mm, "end": v(8.5, 4.6) * mm});
            skLineSegment(sketch, "E8.0.5.22", {"start": v(13, 4) * mm, "end": v(13.5, 4) * mm});
            skLineSegment(sketch, "E8.0.5.23", {"start": v(14.5, 4.4) * mm, "end": v(15, 4.4) * mm});
            skLineSegment(sketch, "E8.0.5.24", {"start": v(7, 4.4) * mm, "end": v(7, 4.6) * mm});
            skLineSegment(sketch, "E8.0.5.25", {"start": v(1, 4) * mm, "end": v(1.5, 4) * mm});
            skLineSegment(sketch, "E8.0.5.26", {"start": v(5, 4.2) * mm, "end": v(5.5, 4.2) * mm});
            skLineSegment(sketch, "E8.0.5.27", {"start": v(18.5, 4.6) * mm, "end": v(19, 4.6) * mm});
            skLineSegment(sketch, "E8.0.5.28", {"start": v(9, 4.4) * mm, "end": v(9, 4.6) * mm});
            skLineSegment(sketch, "E8.0.5.29", {"start": v(2, 4.2) * mm, "end": v(2.5, 4.2) * mm});
            skLineSegment(sketch, "E8.0.5.30", {"start": v(10, 4.2) * mm, "end": v(10.5, 4.2) * mm});
            skLineSegment(sketch, "E8.0.5.31", {"start": v(14.5, 4.6) * mm, "end": v(15, 4.6) * mm});
            skLineSegment(sketch, "E8.0.5.32", {"start": v(9, 4) * mm, "end": v(9.5, 4) * mm});
            skLineSegment(sketch, "E8.0.5.33", {"start": v(20, 4.4) * mm, "end": v(20, 4.6) * mm});
            skLineSegment(sketch, "E8.0.5.34", {"start": v(12.5, 4.4) * mm, "end": v(12.5, 4.6) * mm});
            skLineSegment(sketch, "E8.0.5.35", {"start": v(4.5, 4.4) * mm, "end": v(5, 4.4) * mm});
            skLineSegment(sketch, "E8.0.5.36", {"start": v(8, 4) * mm, "end": v(8.5, 4) * mm});
            skLineSegment(sketch, "E8.0.5.37", {"start": v(12.5, 4) * mm, "end": v(12.5, 4.2) * mm});
            skLineSegment(sketch, "E8.0.5.38", {"start": v(10, 4) * mm, "end": v(10.5, 4) * mm});
            skLineSegment(sketch, "E8.0.5.39", {"start": v(18.5, 4.4) * mm, "end": v(18.5, 4.6) * mm});
            skLineSegment(sketch, "E8.0.5.40", {"start": v(18.5, 4.4) * mm, "end": v(19, 4.4) * mm});
            skLineSegment(sketch, "E8.0.5.41", {"start": v(0.5, 4.6) * mm, "end": v(1, 4.6) * mm});
            skLineSegment(sketch, "E8.0.5.42", {"start": v(14, 4.2) * mm, "end": v(14.5, 4.2) * mm});
            skLineSegment(sketch, "E8.0.5.43", {"start": v(8.5, 4) * mm, "end": v(8.5, 4.2) * mm});
            skLineSegment(sketch, "E8.0.5.44", {"start": v(2.5, 4.6) * mm, "end": v(3, 4.6) * mm});
            skLineSegment(sketch, "E8.0.5.45", {"start": v(16.5, 4.6) * mm, "end": v(17, 4.6) * mm});
            skLineSegment(sketch, "E8.0.5.46", {"start": v(2, 4) * mm, "end": v(2.5, 4) * mm});
            skLineSegment(sketch, "E8.0.5.47", {"start": v(7, 4) * mm, "end": v(7.5, 4) * mm});
            skLineSegment(sketch, "E8.0.5.48", {"start": v(3, 4) * mm, "end": v(3, 4.2) * mm});
            skLineSegment(sketch, "E8.0.5.49", {"start": v(16.5, 4.4) * mm, "end": v(17, 4.4) * mm});
            skLineSegment(sketch, "E8.0.5.50", {"start": v(11, 4) * mm, "end": v(11.5, 4) * mm});
            skLineSegment(sketch, "E8.0.5.51", {"start": v(4, 4) * mm, "end": v(4.5, 4) * mm});
            skLineSegment(sketch, "E8.0.5.52", {"start": v(16, 4) * mm, "end": v(16.5, 4) * mm});
            skLineSegment(sketch, "E8.0.5.53", {"start": v(18.5, 4) * mm, "end": v(18.5, 4.2) * mm});
            skLineSegment(sketch, "E8.0.5.54", {"start": v(3, 4.4) * mm, "end": v(3, 4.6) * mm});
            skLineSegment(sketch, "E8.0.5.55", {"start": v(16.5, 4.4) * mm, "end": v(16.5, 4.6) * mm});
            skLineSegment(sketch, "E8.0.5.56", {"start": v(14.5, 4) * mm, "end": v(14.5, 4.2) * mm});
            skLineSegment(sketch, "E8.0.5.57", {"start": v(4.5, 4.4) * mm, "end": v(4.5, 4.6) * mm});
            skLineSegment(sketch, "E8.0.5.58", {"start": v(16, 4.2) * mm, "end": v(16.5, 4.2) * mm});
            skLineSegment(sketch, "E8.0.5.59", {"start": v(8.5, 4.4) * mm, "end": v(9, 4.4) * mm});
            skLineSegment(sketch, "E8.0.5.60", {"start": v(5, 4) * mm, "end": v(5.5, 4) * mm});
            skLineSegment(sketch, "E8.0.5.61", {"start": v(3, 4) * mm, "end": v(3.5, 4) * mm});
            skLineSegment(sketch, "E8.0.5.62", {"start": v(9, 4) * mm, "end": v(9, 4.2) * mm});
            skLineSegment(sketch, "E8.0.5.63", {"start": v(9, 4.2) * mm, "end": v(9.5, 4.2) * mm});
            skLineSegment(sketch, "E8.0.5.64", {"start": v(4, 4.2) * mm, "end": v(4.5, 4.2) * mm});
            skLineSegment(sketch, "E8.0.5.65", {"start": v(19.5, 4.4) * mm, "end": v(20, 4.4) * mm});
            skLineSegment(sketch, "E8.0.5.66", {"start": v(6.5, 4.4) * mm, "end": v(7, 4.4) * mm});
            skLineSegment(sketch, "E8.0.5.67", {"start": v(6, 4.2) * mm, "end": v(6.5, 4.2) * mm});
            skLineSegment(sketch, "E8.0.5.68", {"start": v(6, 4) * mm, "end": v(6.5, 4) * mm});
            skLineSegment(sketch, "E8.0.5.69", {"start": v(5, 4) * mm, "end": v(5, 4.2) * mm});
            skLineSegment(sketch, "E8.0.5.70", {"start": v(19.5, 4) * mm, "end": v(19.5, 4.2) * mm});
            skLineSegment(sketch, "E8.0.5.72", {"start": v(16.5, 4) * mm, "end": v(16.5, 4.2) * mm});
            skLineSegment(sketch, "E8.0.5.73", {"start": v(12.5, 4.6) * mm, "end": v(13, 4.6) * mm});
            skLineSegment(sketch, "E8.0.5.74", {"start": v(6.5, 4.6) * mm, "end": v(7, 4.6) * mm});
            skLineSegment(sketch, "E8.0.5.75", {"start": v(2.5, 4.4) * mm, "end": v(3, 4.4) * mm});
            skLineSegment(sketch, "E8.0.5.76", {"start": v(12.5, 4.4) * mm, "end": v(13, 4.4) * mm});
            skLineSegment(sketch, "E8.0.5.77", {"start": v(5, 4.4) * mm, "end": v(5, 4.6) * mm});
            skLineSegment(sketch, "E8.0.5.78", {"start": v(14, 4) * mm, "end": v(14.5, 4) * mm});
            skLineSegment(sketch, "E8.0.5.79", {"start": v(0.5, 4.4) * mm, "end": v(0.5, 4.6) * mm});
            skLineSegment(sketch, "E8.0.5.80", {"start": v(10.5, 4) * mm, "end": v(10.5, 4.2) * mm});
            skLineSegment(sketch, "E8.0.5.81", {"start": v(1, 4) * mm, "end": v(1, 4.2) * mm});
            skLineSegment(sketch, "E8.0.5.82", {"start": v(17, 4.2) * mm, "end": v(17.5, 4.2) * mm});
            skLineSegment(sketch, "E8.0.5.83", {"start": v(19, 4.4) * mm, "end": v(19, 4.6) * mm});
            skLineSegment(sketch, "E8.0.5.84", {"start": v(1.5, 4) * mm, "end": v(1.5, 4.2) * mm});
            skLineSegment(sketch, "E8.0.5.85", {"start": v(19, 4.2) * mm, "end": v(19.5, 4.2) * mm});
            skLineSegment(sketch, "E8.0.5.86", {"start": v(11, 4.2) * mm, "end": v(11.5, 4.2) * mm});
            skLineSegment(sketch, "E8.0.5.87", {"start": v(15.5, 4) * mm, "end": v(15.5, 4.2) * mm});
            skLineSegment(sketch, "E8.0.5.88", {"start": v(3.5, 4) * mm, "end": v(3.5, 4.2) * mm});
            skLineSegment(sketch, "E8.0.5.89", {"start": v(19.5, 4.6) * mm, "end": v(20, 4.6) * mm});
            skLineSegment(sketch, "E8.0.5.90", {"start": v(15, 4) * mm, "end": v(15, 4.2) * mm});
            skLineSegment(sketch, "E8.0.5.91", {"start": v(19, 4) * mm, "end": v(19, 4.2) * mm});
            skLineSegment(sketch, "E8.0.5.92", {"start": v(16, 4) * mm, "end": v(16, 4.2) * mm});
            skLineSegment(sketch, "E8.0.5.93", {"start": v(6.5, 4.4) * mm, "end": v(6.5, 4.6) * mm});
            skLineSegment(sketch, "E8.0.5.94", {"start": v(5.5, 4) * mm, "end": v(5.5, 4.2) * mm});
            skLineSegment(sketch, "E8.0.5.95", {"start": v(14.5, 4.4) * mm, "end": v(14.5, 4.6) * mm});
            skLineSegment(sketch, "E8.0.5.96", {"start": v(18, 4) * mm, "end": v(18, 4.2) * mm});
            skLineSegment(sketch, "E8.0.5.97", {"start": v(19, 4) * mm, "end": v(19.5, 4) * mm});
            skLineSegment(sketch, "E8.0.5.98", {"start": v(10.5, 4.4) * mm, "end": v(10.5, 4.6) * mm});
            skLineSegment(sketch, "E8.0.5.99", {"start": v(7.5, 4) * mm, "end": v(7.5, 4.2) * mm});
            skLineSegment(sketch, "E8.0.5.100", {"start": v(9.5, 4) * mm, "end": v(9.5, 4.2) * mm});
            skLineSegment(sketch, "E8.0.5.101", {"start": v(17.5, 4) * mm, "end": v(17.5, 4.2) * mm});
            skLineSegment(sketch, "E8.0.5.102", {"start": v(17, 4) * mm, "end": v(17, 4.2) * mm});
            skLineSegment(sketch, "E8.0.5.103", {"start": v(11, 4.4) * mm, "end": v(11, 4.6) * mm});
            skLineSegment(sketch, "E8.0.5.104", {"start": v(15, 4) * mm, "end": v(15.5, 4) * mm});
            skLineSegment(sketch, "E8.0.5.105", {"start": v(11.5, 4) * mm, "end": v(11.5, 4.2) * mm});
            skLineSegment(sketch, "E8.0.5.106", {"start": v(1.5, 4.4) * mm, "end": v(1.5, 4.6) * mm});
            skLineSegment(sketch, "E8.0.5.107", {"start": v(2.5, 4.4) * mm, "end": v(2.5, 4.6) * mm});
            skLineSegment(sketch, "E8.0.5.108", {"start": v(15, 4.4) * mm, "end": v(15, 4.6) * mm});
            skLineSegment(sketch, "E8.0.5.109", {"start": v(13, 4) * mm, "end": v(13, 4.2) * mm});
            skLineSegment(sketch, "E8.0.5.110", {"start": v(13, 4.2) * mm, "end": v(13.5, 4.2) * mm});
            skLineSegment(sketch, "E8.0.5.111", {"start": v(13.5, 4) * mm, "end": v(13.5, 4.2) * mm});
            skLineSegment(sketch, "E8.0.5.112", {"start": v(11, 4) * mm, "end": v(11, 4.2) * mm});
            skLineSegment(sketch, "E8.0.5.113", {"start": v(7.5, 4.6) * mm, "end": v(8, 4.6) * mm});
            skLineSegment(sketch, "E8.0.5.114", {"start": v(8, 4.4) * mm, "end": v(8, 4.6) * mm});
            skLineSegment(sketch, "E8.0.5.115", {"start": v(17.5, 4.4) * mm, "end": v(17.5, 4.6) * mm});
            skLineSegment(sketch, "E8.0.5.116", {"start": v(17.5, 4.6) * mm, "end": v(18, 4.6) * mm});
            skLineSegment(sketch, "E8.0.5.117", {"start": v(18, 4.4) * mm, "end": v(18, 4.6) * mm});
            skLineSegment(sketch, "E8.0.5.118", {"start": v(17.5, 4.4) * mm, "end": v(18, 4.4) * mm});
            skLineSegment(sketch, "E8.0.5.119", {"start": v(5.5, 4.4) * mm, "end": v(5.5, 4.6) * mm});
            skLineSegment(sketch, "E8.0.5.120", {"start": v(13.5, 4.4) * mm, "end": v(13.5, 4.6) * mm});
            skLineSegment(sketch, "E8.0.5.121", {"start": v(9.5, 4.4) * mm, "end": v(10, 4.4) * mm});
            skLineSegment(sketch, "E8.0.5.122", {"start": v(3.5, 4.4) * mm, "end": v(4, 4.4) * mm});
            skLineSegment(sketch, "E8.0.5.123", {"start": v(7.5, 4.4) * mm, "end": v(7.5, 4.6) * mm});
            skLineSegment(sketch, "E8.0.5.124", {"start": v(9.5, 4.6) * mm, "end": v(10, 4.6) * mm});
            skLineSegment(sketch, "E8.0.5.125", {"start": v(15.5, 4.4) * mm, "end": v(16, 4.4) * mm});
            skLineSegment(sketch, "E8.0.5.126", {"start": v(15.5, 4.4) * mm, "end": v(15.5, 4.6) * mm});
            skLineSegment(sketch, "E8.0.5.127", {"start": v(16, 4.4) * mm, "end": v(16, 4.6) * mm});
            skLineSegment(sketch, "E8.0.5.128", {"start": v(11.5, 4.4) * mm, "end": v(11.5, 4.6) * mm});
            skLineSegment(sketch, "E8.0.5.129", {"start": v(2, 4.4) * mm, "end": v(2, 4.6) * mm});
            skLineSegment(sketch, "E8.0.5.130", {"start": v(1.5, 4.4) * mm, "end": v(2, 4.4) * mm});
            skLineSegment(sketch, "E8.0.5.131", {"start": v(7.5, 4.4) * mm, "end": v(8, 4.4) * mm});
            skLineSegment(sketch, "E8.0.5.132", {"start": v(10, 4) * mm, "end": v(10, 4.2) * mm});
            skLineSegment(sketch, "E8.0.5.133", {"start": v(8, 4) * mm, "end": v(8, 4.2) * mm});
            skLineSegment(sketch, "E8.0.5.134", {"start": v(19.5, 4.4) * mm, "end": v(19.5, 4.6) * mm});
            skLineSegment(sketch, "E8.0.5.135", {"start": v(6, 4.4) * mm, "end": v(6, 4.6) * mm});
            skLineSegment(sketch, "E8.0.5.136", {"start": v(12, 4) * mm, "end": v(12, 4.2) * mm});
            skLineSegment(sketch, "E8.0.5.137", {"start": v(9.5, 4.4) * mm, "end": v(9.5, 4.6) * mm});
            skLineSegment(sketch, "E8.0.5.138", {"start": v(3.5, 4.4) * mm, "end": v(3.5, 4.6) * mm});
            skLineSegment(sketch, "E8.0.5.139", {"start": v(15.5, 4.6) * mm, "end": v(16, 4.6) * mm});
            skLineSegment(sketch, "E8.0.5.140", {"start": v(4, 4) * mm, "end": v(4, 4.2) * mm});
            skLineSegment(sketch, "E8.0.5.141", {"start": v(2, 4) * mm, "end": v(2, 4.2) * mm});
            skLineSegment(sketch, "E8.0.5.142", {"start": v(13.5, 4.6) * mm, "end": v(14, 4.6) * mm});
            skLineSegment(sketch, "E8.0.5.143", {"start": v(11.5, 4.6) * mm, "end": v(12, 4.6) * mm});
            skLineSegment(sketch, "E8.0.5.144", {"start": v(5.5, 4.6) * mm, "end": v(6, 4.6) * mm});
            skLineSegment(sketch, "E8.0.5.145", {"start": v(14, 4) * mm, "end": v(14, 4.2) * mm});
            skLineSegment(sketch, "E8.0.5.146", {"start": v(15, 4.2) * mm, "end": v(15.5, 4.2) * mm});
            skLineSegment(sketch, "E8.0.5.147", {"start": v(4, 4.4) * mm, "end": v(4, 4.6) * mm});
            skLineSegment(sketch, "E8.0.5.148", {"start": v(1.5, 4.6) * mm, "end": v(2, 4.6) * mm});
            skLineSegment(sketch, "E8.0.5.149", {"start": v(11.5, 4.4) * mm, "end": v(12, 4.4) * mm});
            skLineSegment(sketch, "E8.0.5.150", {"start": v(6, 4) * mm, "end": v(6, 4.2) * mm});
            skLineSegment(sketch, "E8.0.5.151", {"start": v(12, 4.4) * mm, "end": v(12, 4.6) * mm});
            skLineSegment(sketch, "E8.0.5.152", {"start": v(13.5, 4.4) * mm, "end": v(14, 4.4) * mm});
            skLineSegment(sketch, "E8.0.5.153", {"start": v(5.5, 4.4) * mm, "end": v(6, 4.4) * mm});
            skLineSegment(sketch, "E8.0.5.154", {"start": v(10, 4.4) * mm, "end": v(10, 4.6) * mm});
            skLineSegment(sketch, "E8.0.5.155", {"start": v(3.5, 4.6) * mm, "end": v(4, 4.6) * mm});
            skLineSegment(sketch, "E8.0.5.156", {"start": v(14, 4.4) * mm, "end": v(14, 4.6) * mm});
            skLineSegment(sketch, "E8.direction1", {"start": v(0.5, 0) * mm, "end": v(25.5, 0) * mm, "construction": true});
            skLineSegment(sketch, "E8.direction2", {"start": v(0.5, 0) * mm, "end": v(0.5, 0.8) * mm, "construction": true});
            skSolve(sketch);
        }
        {
            var Q0;
            Q0 = qSketchRegion(id + "F2", true);
            extrude(context, id + "F3", {"entities" : qUnion([Q0]), "operationType" : NewBodyOperationType.ADD, "depth" : 25 * mm});
        }
        {
            var Q0;
            Q0=makeQuery(id+"F3.opExtrude","CAP_FACE",FACE,{"disambiguationData":[OSD([sQuery(id+"F2.wireOp",EDGE,"E5.0.4.24"),sQuery(id+"F2.wireOp",EDGE,"E5.0.4.89"),sQuery(id+"F2.wireOp",EDGE,"E5.0.4.95"),sQuery(id+"F2.wireOp",EDGE,"E5.0.4.111")])],"isStart":false});
            var sketch = newSketch(context, id + "F4", { "sketchPlane" : qUnion([Q0])});
            skLineSegment(sketch, "E9.bottom", {"start": v(-20, 4.8) * mm, "end": v(20, 4.8) * mm});
            skLineSegment(sketch, "E9.top", {"start": v(-20, -0.58) * mm, "end": v(20, -0.58) * mm});
            skLineSegment(sketch, "E9.left", {"start": v(-20, 4.8) * mm, "end": v(-20, -0.58) * mm});
            skLineSegment(sketch, "E9.right", {"start": v(20, 4.8) * mm, "end": v(20, -0.58) * mm});
            skSolve(sketch);
        }
        {
            var Q0;
            Q0 = qSketchRegion(id + "F4", true);
            extrude(context, id + "F5", {"entities" : qUnion([Q0]), "operationType" : NewBodyOperationType.ADD, "depth" : 2 * mm});
        }
        {
            var Q0;
            Q0=makeQuery(id+"F1.opExtrude","CAP_FACE",FACE,{"disambiguationData":[OSD([sQuery(id+"F0.wireOp",EDGE,"E0.bottom"),sQuery(id+"F0.wireOp",EDGE,"E0.top"),sQuery(id+"F0.wireOp",EDGE,"E0.left"),sQuery(id+"F0.wireOp",EDGE,"E0.right")])],"isStart":true});
            var sketch = newSketch(context, id + "F6", { "sketchPlane" : qUnion([Q0])});
            skLineSegment(sketch, "E10", {"start": v(-20, 4.8) * mm, "end": v(-20, 0) * mm});
            skLineSegment(sketch, "E11", {"start": v(-20, 0) * mm, "end": v(20, 0) * mm});
            skLineSegment(sketch, "E12", {"start": v(20, 0) * mm, "end": v(20, -6.32) * mm});
            skLineSegment(sketch, "E13", {"start": v(20, -6.32) * mm, "end": v(-30.63, -6.32) * mm});
            skLineSegment(sketch, "E14", {"start": v(-30.63, -6.32) * mm, "end": v(-30.63, 4.8) * mm});
            skLineSegment(sketch, "E15", {"start": v(-30.63, 4.8) * mm, "end": v(-20, 4.8) * mm});
            skSolve(sketch);
        }
        {
            var Q0;
            Q0 = qSketchRegion(id + "F6", true);
            extrude(context, id + "F7", {"entities" : qUnion([Q0]), "operationType" : NewBodyOperationType.REMOVE, "oppositeDirection" : true, "depth" : 43.6 * mm});
        }
    });
